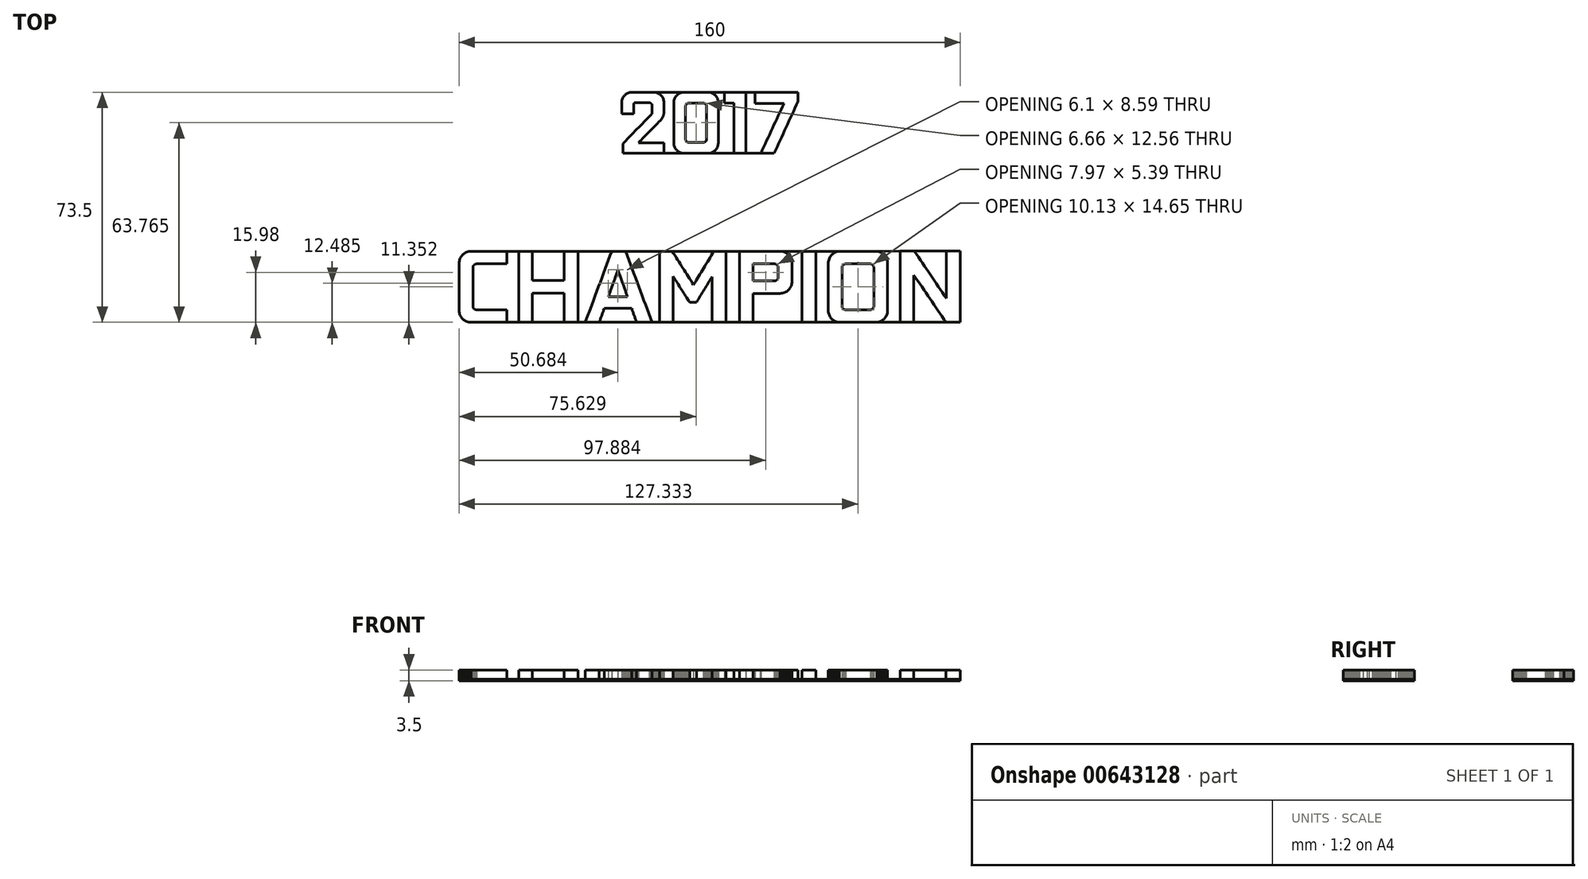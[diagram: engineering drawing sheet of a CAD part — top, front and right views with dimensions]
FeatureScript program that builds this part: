
annotation { "Feature Type Name" : "Feature", "Feature Type Description" : "" }
export const myFeature = defineFeature(function(context is Context, id is Id, definition is map)
    precondition{}
    {
        {
            var Q0;
            Q0=qCreatedBy(makeId("Top.planeOp"),FACE);
            var sketch = newSketch(context, id + "F0", { "sketchPlane" : qUnion([Q0])});
            skLineSegment(sketch, "E0", {"start": v(-76.2, -14.05) * mm, "end": v(-76.59, -14.07) * mm});
            skLineSegment(sketch, "E1", {"start": v(-76.59, -14.07) * mm, "end": v(-76.97, -14.12) * mm});
            skLineSegment(sketch, "E2", {"start": v(-76.97, -14.12) * mm, "end": v(-77.33, -14.22) * mm});
            skLineSegment(sketch, "E3", {"start": v(-77.33, -14.22) * mm, "end": v(-77.68, -14.35) * mm});
            skLineSegment(sketch, "E4", {"start": v(-77.68, -14.35) * mm, "end": v(-78.01, -14.5) * mm});
            skLineSegment(sketch, "E5", {"start": v(-78.01, -14.5) * mm, "end": v(-78.32, -14.7) * mm});
            skLineSegment(sketch, "E6", {"start": v(-78.32, -14.7) * mm, "end": v(-78.62, -14.91) * mm});
            skLineSegment(sketch, "E7", {"start": v(-78.62, -14.91) * mm, "end": v(-78.89, -15.16) * mm});
            skLineSegment(sketch, "E8", {"start": v(-78.89, -15.16) * mm, "end": v(-79.13, -15.43) * mm});
            skLineSegment(sketch, "E9", {"start": v(-79.13, -15.43) * mm, "end": v(-79.35, -15.72) * mm});
            skLineSegment(sketch, "E10", {"start": v(-79.35, -15.72) * mm, "end": v(-79.54, -16.03) * mm});
            skLineSegment(sketch, "E11", {"start": v(-79.54, -16.03) * mm, "end": v(-79.7, -16.36) * mm});
            skLineSegment(sketch, "E12", {"start": v(-79.7, -16.36) * mm, "end": v(-79.83, -16.71) * mm});
            skLineSegment(sketch, "E13", {"start": v(-79.83, -16.71) * mm, "end": v(-79.92, -17.08) * mm});
            skLineSegment(sketch, "E14", {"start": v(-79.92, -17.08) * mm, "end": v(-79.98, -17.45) * mm});
            skLineSegment(sketch, "E15", {"start": v(-79.98, -17.45) * mm, "end": v(-80, -17.84) * mm});
            skLineSegment(sketch, "E16", {"start": v(-80, -17.84) * mm, "end": v(-80, -18.79) * mm});
            skLineSegment(sketch, "E17", {"start": v(-80, -18.79) * mm, "end": v(-80, -19.73) * mm});
            skLineSegment(sketch, "E18", {"start": v(-80, -19.73) * mm, "end": v(-80, -20.68) * mm});
            skLineSegment(sketch, "E19", {"start": v(-80, -20.68) * mm, "end": v(-80, -21.63) * mm});
            skLineSegment(sketch, "E20", {"start": v(-80, -21.63) * mm, "end": v(-80, -22.57) * mm});
            skLineSegment(sketch, "E21", {"start": v(-80, -22.57) * mm, "end": v(-80, -23.52) * mm});
            skLineSegment(sketch, "E22", {"start": v(-80, -23.52) * mm, "end": v(-80, -24.47) * mm});
            skLineSegment(sketch, "E23", {"start": v(-80, -24.47) * mm, "end": v(-80, -25.41) * mm});
            skLineSegment(sketch, "E24", {"start": v(-80, -25.41) * mm, "end": v(-80, -26.36) * mm});
            skLineSegment(sketch, "E25", {"start": v(-80, -26.36) * mm, "end": v(-80, -27.3) * mm});
            skLineSegment(sketch, "E26", {"start": v(-80, -27.3) * mm, "end": v(-80, -28.25) * mm});
            skLineSegment(sketch, "E27", {"start": v(-80, -28.25) * mm, "end": v(-80, -29.2) * mm});
            skLineSegment(sketch, "E28", {"start": v(-80, -29.2) * mm, "end": v(-80, -30.15) * mm});
            skLineSegment(sketch, "E29", {"start": v(-80, -30.15) * mm, "end": v(-80, -31.1) * mm});
            skLineSegment(sketch, "E30", {"start": v(-80, -31.1) * mm, "end": v(-80, -32.04) * mm});
            skLineSegment(sketch, "E31", {"start": v(-80, -32.04) * mm, "end": v(-80, -32.99) * mm});
            skLineSegment(sketch, "E32", {"start": v(-80, -32.99) * mm, "end": v(-79.98, -33.37) * mm});
            skLineSegment(sketch, "E33", {"start": v(-79.98, -33.37) * mm, "end": v(-79.92, -33.74) * mm});
            skLineSegment(sketch, "E34", {"start": v(-79.92, -33.74) * mm, "end": v(-79.83, -34.1) * mm});
            skLineSegment(sketch, "E35", {"start": v(-79.83, -34.1) * mm, "end": v(-79.7, -34.45) * mm});
            skLineSegment(sketch, "E36", {"start": v(-79.7, -34.45) * mm, "end": v(-79.54, -34.77) * mm});
            skLineSegment(sketch, "E37", {"start": v(-79.54, -34.77) * mm, "end": v(-79.35, -35.08) * mm});
            skLineSegment(sketch, "E38", {"start": v(-79.35, -35.08) * mm, "end": v(-79.13, -35.37) * mm});
            skLineSegment(sketch, "E39", {"start": v(-79.13, -35.37) * mm, "end": v(-78.89, -35.64) * mm});
            skLineSegment(sketch, "E40", {"start": v(-78.89, -35.64) * mm, "end": v(-78.62, -35.89) * mm});
            skLineSegment(sketch, "E41", {"start": v(-78.62, -35.89) * mm, "end": v(-78.32, -36.1) * mm});
            skLineSegment(sketch, "E42", {"start": v(-78.32, -36.1) * mm, "end": v(-78.01, -36.3) * mm});
            skLineSegment(sketch, "E43", {"start": v(-78.01, -36.3) * mm, "end": v(-77.68, -36.45) * mm});
            skLineSegment(sketch, "E44", {"start": v(-77.68, -36.45) * mm, "end": v(-77.33, -36.58) * mm});
            skLineSegment(sketch, "E45", {"start": v(-77.33, -36.58) * mm, "end": v(-76.97, -36.67) * mm});
            skLineSegment(sketch, "E46", {"start": v(-76.97, -36.67) * mm, "end": v(-76.59, -36.73) * mm});
            skLineSegment(sketch, "E47", {"start": v(-76.59, -36.73) * mm, "end": v(-76.2, -36.75) * mm});
            skLineSegment(sketch, "E48", {"start": v(-76.2, -36.75) * mm, "end": v(-75.49, -36.75) * mm});
            skLineSegment(sketch, "E49", {"start": v(-75.49, -36.75) * mm, "end": v(-74.78, -36.75) * mm});
            skLineSegment(sketch, "E50", {"start": v(-74.78, -36.75) * mm, "end": v(-74.07, -36.75) * mm});
            skLineSegment(sketch, "E51", {"start": v(-74.07, -36.75) * mm, "end": v(-73.36, -36.75) * mm});
            skLineSegment(sketch, "E52", {"start": v(-73.36, -36.75) * mm, "end": v(-72.65, -36.75) * mm});
            skLineSegment(sketch, "E53", {"start": v(-72.65, -36.75) * mm, "end": v(-71.94, -36.75) * mm});
            skLineSegment(sketch, "E54", {"start": v(-71.94, -36.75) * mm, "end": v(-71.23, -36.75) * mm});
            skLineSegment(sketch, "E55", {"start": v(-71.23, -36.75) * mm, "end": v(-70.52, -36.75) * mm});
            skLineSegment(sketch, "E56", {"start": v(-70.52, -36.75) * mm, "end": v(-69.8, -36.75) * mm});
            skLineSegment(sketch, "E57", {"start": v(-69.8, -36.75) * mm, "end": v(-69.1, -36.75) * mm});
            skLineSegment(sketch, "E58", {"start": v(-69.1, -36.75) * mm, "end": v(-68.39, -36.75) * mm});
            skLineSegment(sketch, "E59", {"start": v(-68.39, -36.75) * mm, "end": v(-67.67, -36.75) * mm});
            skLineSegment(sketch, "E60", {"start": v(-67.67, -36.75) * mm, "end": v(-66.96, -36.75) * mm});
            skLineSegment(sketch, "E61", {"start": v(-66.96, -36.75) * mm, "end": v(-66.25, -36.75) * mm});
            skLineSegment(sketch, "E62", {"start": v(-66.25, -36.75) * mm, "end": v(-65.54, -36.75) * mm});
            skLineSegment(sketch, "E63", {"start": v(-65.54, -36.75) * mm, "end": v(-64.83, -36.75) * mm});
            skLineSegment(sketch, "E64", {"start": v(-64.83, -36.75) * mm, "end": v(-64.83, -36.5) * mm});
            skLineSegment(sketch, "E65", {"start": v(-64.83, -36.5) * mm, "end": v(-64.83, -36.25) * mm});
            skLineSegment(sketch, "E66", {"start": v(-64.83, -36.25) * mm, "end": v(-64.83, -36) * mm});
            skLineSegment(sketch, "E67", {"start": v(-64.83, -36) * mm, "end": v(-64.83, -35.74) * mm});
            skLineSegment(sketch, "E68", {"start": v(-64.83, -35.74) * mm, "end": v(-64.83, -35.5) * mm});
            skLineSegment(sketch, "E69", {"start": v(-64.83, -35.5) * mm, "end": v(-64.83, -35.24) * mm});
            skLineSegment(sketch, "E70", {"start": v(-64.83, -35.24) * mm, "end": v(-64.83, -34.99) * mm});
            skLineSegment(sketch, "E71", {"start": v(-64.83, -34.99) * mm, "end": v(-64.83, -34.74) * mm});
            skLineSegment(sketch, "E72", {"start": v(-64.83, -34.74) * mm, "end": v(-64.83, -34.48) * mm});
            skLineSegment(sketch, "E73", {"start": v(-64.83, -34.48) * mm, "end": v(-64.83, -34.23) * mm});
            skLineSegment(sketch, "E74", {"start": v(-64.83, -34.23) * mm, "end": v(-64.83, -33.98) * mm});
            skLineSegment(sketch, "E75", {"start": v(-64.83, -33.98) * mm, "end": v(-64.83, -33.73) * mm});
            skLineSegment(sketch, "E76", {"start": v(-64.83, -33.73) * mm, "end": v(-64.83, -33.48) * mm});
            skLineSegment(sketch, "E77", {"start": v(-64.83, -33.48) * mm, "end": v(-64.83, -33.22) * mm});
            skLineSegment(sketch, "E78", {"start": v(-64.83, -33.22) * mm, "end": v(-64.83, -32.97) * mm});
            skLineSegment(sketch, "E79", {"start": v(-64.83, -32.97) * mm, "end": v(-64.83, -32.72) * mm});
            skLineSegment(sketch, "E80", {"start": v(-64.83, -32.72) * mm, "end": v(-65.44, -32.72) * mm});
            skLineSegment(sketch, "E81", {"start": v(-65.44, -32.72) * mm, "end": v(-66.04, -32.72) * mm});
            skLineSegment(sketch, "E82", {"start": v(-66.04, -32.72) * mm, "end": v(-66.64, -32.72) * mm});
            skLineSegment(sketch, "E83", {"start": v(-66.64, -32.72) * mm, "end": v(-67.24, -32.72) * mm});
            skLineSegment(sketch, "E84", {"start": v(-67.24, -32.72) * mm, "end": v(-67.84, -32.72) * mm});
            skLineSegment(sketch, "E85", {"start": v(-67.84, -32.72) * mm, "end": v(-68.45, -32.72) * mm});
            skLineSegment(sketch, "E86", {"start": v(-68.45, -32.72) * mm, "end": v(-69.05, -32.72) * mm});
            skLineSegment(sketch, "E87", {"start": v(-69.05, -32.72) * mm, "end": v(-69.65, -32.72) * mm});
            skLineSegment(sketch, "E88", {"start": v(-69.65, -32.72) * mm, "end": v(-70.25, -32.72) * mm});
            skLineSegment(sketch, "E89", {"start": v(-70.25, -32.72) * mm, "end": v(-70.85, -32.72) * mm});
            skLineSegment(sketch, "E90", {"start": v(-70.85, -32.72) * mm, "end": v(-71.46, -32.72) * mm});
            skLineSegment(sketch, "E91", {"start": v(-71.46, -32.72) * mm, "end": v(-72.06, -32.72) * mm});
            skLineSegment(sketch, "E92", {"start": v(-72.06, -32.72) * mm, "end": v(-72.66, -32.72) * mm});
            skLineSegment(sketch, "E93", {"start": v(-72.66, -32.72) * mm, "end": v(-73.26, -32.72) * mm});
            skLineSegment(sketch, "E94", {"start": v(-73.26, -32.72) * mm, "end": v(-73.86, -32.72) * mm});
            skLineSegment(sketch, "E95", {"start": v(-73.86, -32.72) * mm, "end": v(-74.47, -32.72) * mm});
            skLineSegment(sketch, "E96", {"start": v(-74.47, -32.72) * mm, "end": v(-74.58, -32.72) * mm});
            skLineSegment(sketch, "E97", {"start": v(-74.58, -32.72) * mm, "end": v(-74.7, -32.7) * mm});
            skLineSegment(sketch, "E98", {"start": v(-74.7, -32.7) * mm, "end": v(-74.8, -32.67) * mm});
            skLineSegment(sketch, "E99", {"start": v(-74.8, -32.67) * mm, "end": v(-74.91, -32.63) * mm});
            skLineSegment(sketch, "E100", {"start": v(-74.91, -32.63) * mm, "end": v(-75.01, -32.59) * mm});
            skLineSegment(sketch, "E101", {"start": v(-75.01, -32.59) * mm, "end": v(-75.1, -32.53) * mm});
            skLineSegment(sketch, "E102", {"start": v(-75.1, -32.53) * mm, "end": v(-75.2, -32.47) * mm});
            skLineSegment(sketch, "E103", {"start": v(-75.2, -32.47) * mm, "end": v(-75.27, -32.4) * mm});
            skLineSegment(sketch, "E104", {"start": v(-75.27, -32.4) * mm, "end": v(-75.34, -32.31) * mm});
            skLineSegment(sketch, "E105", {"start": v(-75.34, -32.31) * mm, "end": v(-75.4, -32.23) * mm});
            skLineSegment(sketch, "E106", {"start": v(-75.4, -32.23) * mm, "end": v(-75.46, -32.13) * mm});
            skLineSegment(sketch, "E107", {"start": v(-75.46, -32.13) * mm, "end": v(-75.51, -32.03) * mm});
            skLineSegment(sketch, "E108", {"start": v(-75.51, -32.03) * mm, "end": v(-75.55, -31.93) * mm});
            skLineSegment(sketch, "E109", {"start": v(-75.55, -31.93) * mm, "end": v(-75.58, -31.82) * mm});
            skLineSegment(sketch, "E110", {"start": v(-75.58, -31.82) * mm, "end": v(-75.6, -31.7) * mm});
            skLineSegment(sketch, "E111", {"start": v(-75.6, -31.7) * mm, "end": v(-75.6, -31.59) * mm});
            skLineSegment(sketch, "E112", {"start": v(-75.6, -31.59) * mm, "end": v(-75.6, -30.82) * mm});
            skLineSegment(sketch, "E113", {"start": v(-75.6, -30.82) * mm, "end": v(-75.6, -30.04) * mm});
            skLineSegment(sketch, "E114", {"start": v(-75.6, -30.04) * mm, "end": v(-75.6, -29.27) * mm});
            skLineSegment(sketch, "E115", {"start": v(-75.6, -29.27) * mm, "end": v(-75.6, -28.5) * mm});
            skLineSegment(sketch, "E116", {"start": v(-75.6, -28.5) * mm, "end": v(-75.6, -27.72) * mm});
            skLineSegment(sketch, "E117", {"start": v(-75.6, -27.72) * mm, "end": v(-75.6, -26.95) * mm});
            skLineSegment(sketch, "E118", {"start": v(-75.6, -26.95) * mm, "end": v(-75.6, -26.17) * mm});
            skLineSegment(sketch, "E119", {"start": v(-75.6, -26.17) * mm, "end": v(-75.6, -25.4) * mm});
            skLineSegment(sketch, "E120", {"start": v(-75.6, -25.4) * mm, "end": v(-75.6, -24.62) * mm});
            skLineSegment(sketch, "E121", {"start": v(-75.6, -24.62) * mm, "end": v(-75.6, -23.85) * mm});
            skLineSegment(sketch, "E122", {"start": v(-75.6, -23.85) * mm, "end": v(-75.6, -23.08) * mm});
            skLineSegment(sketch, "E123", {"start": v(-75.6, -23.08) * mm, "end": v(-75.6, -22.3) * mm});
            skLineSegment(sketch, "E124", {"start": v(-75.6, -22.3) * mm, "end": v(-75.6, -21.53) * mm});
            skLineSegment(sketch, "E125", {"start": v(-75.6, -21.53) * mm, "end": v(-75.6, -20.75) * mm});
            skLineSegment(sketch, "E126", {"start": v(-75.6, -20.75) * mm, "end": v(-75.6, -19.98) * mm});
            skLineSegment(sketch, "E127", {"start": v(-75.6, -19.98) * mm, "end": v(-75.6, -19.2) * mm});
            skLineSegment(sketch, "E128", {"start": v(-75.6, -19.2) * mm, "end": v(-75.6, -19.1) * mm});
            skLineSegment(sketch, "E129", {"start": v(-75.6, -19.1) * mm, "end": v(-75.58, -18.99) * mm});
            skLineSegment(sketch, "E130", {"start": v(-75.58, -18.99) * mm, "end": v(-75.55, -18.88) * mm});
            skLineSegment(sketch, "E131", {"start": v(-75.55, -18.88) * mm, "end": v(-75.51, -18.78) * mm});
            skLineSegment(sketch, "E132", {"start": v(-75.51, -18.78) * mm, "end": v(-75.46, -18.68) * mm});
            skLineSegment(sketch, "E133", {"start": v(-75.46, -18.68) * mm, "end": v(-75.4, -18.59) * mm});
            skLineSegment(sketch, "E134", {"start": v(-75.4, -18.59) * mm, "end": v(-75.34, -18.5) * mm});
            skLineSegment(sketch, "E135", {"start": v(-75.34, -18.5) * mm, "end": v(-75.27, -18.42) * mm});
            skLineSegment(sketch, "E136", {"start": v(-75.27, -18.42) * mm, "end": v(-75.2, -18.34) * mm});
            skLineSegment(sketch, "E137", {"start": v(-75.2, -18.34) * mm, "end": v(-75.1, -18.27) * mm});
            skLineSegment(sketch, "E138", {"start": v(-75.1, -18.27) * mm, "end": v(-75.01, -18.22) * mm});
            skLineSegment(sketch, "E139", {"start": v(-75.01, -18.22) * mm, "end": v(-74.91, -18.17) * mm});
            skLineSegment(sketch, "E140", {"start": v(-74.91, -18.17) * mm, "end": v(-74.8, -18.13) * mm});
            skLineSegment(sketch, "E141", {"start": v(-74.8, -18.13) * mm, "end": v(-74.7, -18.1) * mm});
            skLineSegment(sketch, "E142", {"start": v(-74.7, -18.1) * mm, "end": v(-74.58, -18.08) * mm});
            skLineSegment(sketch, "E143", {"start": v(-74.58, -18.08) * mm, "end": v(-74.47, -18.07) * mm});
            skLineSegment(sketch, "E144", {"start": v(-74.47, -18.07) * mm, "end": v(-73.86, -18.07) * mm});
            skLineSegment(sketch, "E145", {"start": v(-73.86, -18.07) * mm, "end": v(-73.26, -18.07) * mm});
            skLineSegment(sketch, "E146", {"start": v(-73.26, -18.07) * mm, "end": v(-72.66, -18.07) * mm});
            skLineSegment(sketch, "E147", {"start": v(-72.66, -18.07) * mm, "end": v(-72.06, -18.07) * mm});
            skLineSegment(sketch, "E148", {"start": v(-72.06, -18.07) * mm, "end": v(-71.46, -18.07) * mm});
            skLineSegment(sketch, "E149", {"start": v(-71.46, -18.07) * mm, "end": v(-70.85, -18.07) * mm});
            skLineSegment(sketch, "E150", {"start": v(-70.85, -18.07) * mm, "end": v(-70.25, -18.07) * mm});
            skLineSegment(sketch, "E151", {"start": v(-70.25, -18.07) * mm, "end": v(-69.65, -18.07) * mm});
            skLineSegment(sketch, "E152", {"start": v(-69.65, -18.07) * mm, "end": v(-69.05, -18.07) * mm});
            skLineSegment(sketch, "E153", {"start": v(-69.05, -18.07) * mm, "end": v(-68.45, -18.07) * mm});
            skLineSegment(sketch, "E154", {"start": v(-68.45, -18.07) * mm, "end": v(-67.84, -18.07) * mm});
            skLineSegment(sketch, "E155", {"start": v(-67.84, -18.07) * mm, "end": v(-67.24, -18.07) * mm});
            skLineSegment(sketch, "E156", {"start": v(-67.24, -18.07) * mm, "end": v(-66.64, -18.07) * mm});
            skLineSegment(sketch, "E157", {"start": v(-66.64, -18.07) * mm, "end": v(-66.04, -18.07) * mm});
            skLineSegment(sketch, "E158", {"start": v(-66.04, -18.07) * mm, "end": v(-65.44, -18.07) * mm});
            skLineSegment(sketch, "E159", {"start": v(-65.44, -18.07) * mm, "end": v(-64.83, -18.07) * mm});
            skLineSegment(sketch, "E160", {"start": v(-64.83, -18.07) * mm, "end": v(-64.83, -17.82) * mm});
            skLineSegment(sketch, "E161", {"start": v(-64.83, -17.82) * mm, "end": v(-64.83, -17.57) * mm});
            skLineSegment(sketch, "E162", {"start": v(-64.83, -17.57) * mm, "end": v(-64.83, -17.32) * mm});
            skLineSegment(sketch, "E163", {"start": v(-64.83, -17.32) * mm, "end": v(-64.83, -17.07) * mm});
            skLineSegment(sketch, "E164", {"start": v(-64.83, -17.07) * mm, "end": v(-64.83, -16.82) * mm});
            skLineSegment(sketch, "E165", {"start": v(-64.83, -16.82) * mm, "end": v(-64.83, -16.56) * mm});
            skLineSegment(sketch, "E166", {"start": v(-64.83, -16.56) * mm, "end": v(-64.83, -16.31) * mm});
            skLineSegment(sketch, "E167", {"start": v(-64.83, -16.31) * mm, "end": v(-64.83, -16.06) * mm});
            skLineSegment(sketch, "E168", {"start": v(-64.83, -16.06) * mm, "end": v(-64.83, -15.8) * mm});
            skLineSegment(sketch, "E169", {"start": v(-64.83, -15.8) * mm, "end": v(-64.83, -15.56) * mm});
            skLineSegment(sketch, "E170", {"start": v(-64.83, -15.56) * mm, "end": v(-64.83, -15.3) * mm});
            skLineSegment(sketch, "E171", {"start": v(-64.83, -15.3) * mm, "end": v(-64.83, -15.05) * mm});
            skLineSegment(sketch, "E172", {"start": v(-64.83, -15.05) * mm, "end": v(-64.83, -14.8) * mm});
            skLineSegment(sketch, "E173", {"start": v(-64.83, -14.8) * mm, "end": v(-64.83, -14.55) * mm});
            skLineSegment(sketch, "E174", {"start": v(-64.83, -14.55) * mm, "end": v(-64.83, -14.3) * mm});
            skLineSegment(sketch, "E175", {"start": v(-64.83, -14.3) * mm, "end": v(-64.83, -14.05) * mm});
            skLineSegment(sketch, "E176", {"start": v(-64.83, -14.05) * mm, "end": v(-65.54, -14.05) * mm});
            skLineSegment(sketch, "E177", {"start": v(-65.54, -14.05) * mm, "end": v(-66.25, -14.05) * mm});
            skLineSegment(sketch, "E178", {"start": v(-66.25, -14.05) * mm, "end": v(-66.96, -14.05) * mm});
            skLineSegment(sketch, "E179", {"start": v(-66.96, -14.05) * mm, "end": v(-67.67, -14.05) * mm});
            skLineSegment(sketch, "E180", {"start": v(-67.67, -14.05) * mm, "end": v(-68.39, -14.05) * mm});
            skLineSegment(sketch, "E181", {"start": v(-68.39, -14.05) * mm, "end": v(-69.1, -14.05) * mm});
            skLineSegment(sketch, "E182", {"start": v(-69.1, -14.05) * mm, "end": v(-69.8, -14.05) * mm});
            skLineSegment(sketch, "E183", {"start": v(-69.8, -14.05) * mm, "end": v(-70.52, -14.05) * mm});
            skLineSegment(sketch, "E184", {"start": v(-70.52, -14.05) * mm, "end": v(-71.23, -14.05) * mm});
            skLineSegment(sketch, "E185", {"start": v(-71.23, -14.05) * mm, "end": v(-71.94, -14.05) * mm});
            skLineSegment(sketch, "E186", {"start": v(-71.94, -14.05) * mm, "end": v(-72.65, -14.05) * mm});
            skLineSegment(sketch, "E187", {"start": v(-72.65, -14.05) * mm, "end": v(-73.36, -14.05) * mm});
            skLineSegment(sketch, "E188", {"start": v(-73.36, -14.05) * mm, "end": v(-74.07, -14.05) * mm});
            skLineSegment(sketch, "E189", {"start": v(-74.07, -14.05) * mm, "end": v(-74.78, -14.05) * mm});
            skLineSegment(sketch, "E190", {"start": v(-74.78, -14.05) * mm, "end": v(-75.49, -14.05) * mm});
            skLineSegment(sketch, "E191", {"start": v(-75.49, -14.05) * mm, "end": v(-76.2, -14.05) * mm});
            skLineSegment(sketch, "E192", {"start": v(-46.47, -14.05) * mm, "end": v(-46.47, -14.63) * mm});
            skLineSegment(sketch, "E193", {"start": v(-46.47, -14.63) * mm, "end": v(-46.47, -15.22) * mm});
            skLineSegment(sketch, "E194", {"start": v(-46.47, -15.22) * mm, "end": v(-46.47, -15.8) * mm});
            skLineSegment(sketch, "E195", {"start": v(-46.47, -15.8) * mm, "end": v(-46.47, -16.39) * mm});
            skLineSegment(sketch, "E196", {"start": v(-46.47, -16.39) * mm, "end": v(-46.47, -16.97) * mm});
            skLineSegment(sketch, "E197", {"start": v(-46.47, -16.97) * mm, "end": v(-46.47, -17.55) * mm});
            skLineSegment(sketch, "E198", {"start": v(-46.47, -17.55) * mm, "end": v(-46.47, -18.14) * mm});
            skLineSegment(sketch, "E199", {"start": v(-46.47, -18.14) * mm, "end": v(-46.47, -18.72) * mm});
            skLineSegment(sketch, "E200", {"start": v(-46.47, -18.72) * mm, "end": v(-46.47, -19.3) * mm});
            skLineSegment(sketch, "E201", {"start": v(-46.47, -19.3) * mm, "end": v(-46.47, -19.9) * mm});
            skLineSegment(sketch, "E202", {"start": v(-46.47, -19.9) * mm, "end": v(-46.47, -20.48) * mm});
            skLineSegment(sketch, "E203", {"start": v(-46.47, -20.48) * mm, "end": v(-46.47, -21.06) * mm});
            skLineSegment(sketch, "E204", {"start": v(-46.47, -21.06) * mm, "end": v(-46.47, -21.65) * mm});
            skLineSegment(sketch, "E205", {"start": v(-46.47, -21.65) * mm, "end": v(-46.47, -22.23) * mm});
            skLineSegment(sketch, "E206", {"start": v(-46.47, -22.23) * mm, "end": v(-46.47, -22.82) * mm});
            skLineSegment(sketch, "E207", {"start": v(-46.47, -22.82) * mm, "end": v(-46.47, -23.4) * mm});
            skLineSegment(sketch, "E208", {"start": v(-46.47, -23.4) * mm, "end": v(-47.1, -23.4) * mm});
            skLineSegment(sketch, "E209", {"start": v(-47.1, -23.4) * mm, "end": v(-47.73, -23.4) * mm});
            skLineSegment(sketch, "E210", {"start": v(-47.73, -23.4) * mm, "end": v(-48.37, -23.4) * mm});
            skLineSegment(sketch, "E211", {"start": v(-48.37, -23.4) * mm, "end": v(-49, -23.4) * mm});
            skLineSegment(sketch, "E212", {"start": v(-49, -23.4) * mm, "end": v(-49.63, -23.4) * mm});
            skLineSegment(sketch, "E213", {"start": v(-49.63, -23.4) * mm, "end": v(-50.27, -23.4) * mm});
            skLineSegment(sketch, "E214", {"start": v(-50.27, -23.4) * mm, "end": v(-50.9, -23.4) * mm});
            skLineSegment(sketch, "E215", {"start": v(-50.9, -23.4) * mm, "end": v(-51.53, -23.4) * mm});
            skLineSegment(sketch, "E216", {"start": v(-51.53, -23.4) * mm, "end": v(-52.17, -23.4) * mm});
            skLineSegment(sketch, "E217", {"start": v(-52.17, -23.4) * mm, "end": v(-52.8, -23.4) * mm});
            skLineSegment(sketch, "E218", {"start": v(-52.8, -23.4) * mm, "end": v(-53.43, -23.4) * mm});
            skLineSegment(sketch, "E219", {"start": v(-53.43, -23.4) * mm, "end": v(-54.07, -23.4) * mm});
            skLineSegment(sketch, "E220", {"start": v(-54.07, -23.4) * mm, "end": v(-54.7, -23.4) * mm});
            skLineSegment(sketch, "E221", {"start": v(-54.7, -23.4) * mm, "end": v(-55.33, -23.4) * mm});
            skLineSegment(sketch, "E222", {"start": v(-55.33, -23.4) * mm, "end": v(-55.97, -23.4) * mm});
            skLineSegment(sketch, "E223", {"start": v(-55.97, -23.4) * mm, "end": v(-56.6, -23.4) * mm});
            skLineSegment(sketch, "E224", {"start": v(-56.6, -23.4) * mm, "end": v(-56.6, -22.82) * mm});
            skLineSegment(sketch, "E225", {"start": v(-56.6, -22.82) * mm, "end": v(-56.6, -22.23) * mm});
            skLineSegment(sketch, "E226", {"start": v(-56.6, -22.23) * mm, "end": v(-56.6, -21.65) * mm});
            skLineSegment(sketch, "E227", {"start": v(-56.6, -21.65) * mm, "end": v(-56.6, -21.06) * mm});
            skLineSegment(sketch, "E228", {"start": v(-56.6, -21.06) * mm, "end": v(-56.6, -20.48) * mm});
            skLineSegment(sketch, "E229", {"start": v(-56.6, -20.48) * mm, "end": v(-56.6, -19.9) * mm});
            skLineSegment(sketch, "E230", {"start": v(-56.6, -19.9) * mm, "end": v(-56.6, -19.3) * mm});
            skLineSegment(sketch, "E231", {"start": v(-56.6, -19.3) * mm, "end": v(-56.6, -18.72) * mm});
            skLineSegment(sketch, "E232", {"start": v(-56.6, -18.72) * mm, "end": v(-56.6, -18.14) * mm});
            skLineSegment(sketch, "E233", {"start": v(-56.6, -18.14) * mm, "end": v(-56.6, -17.55) * mm});
            skLineSegment(sketch, "E234", {"start": v(-56.6, -17.55) * mm, "end": v(-56.6, -16.97) * mm});
            skLineSegment(sketch, "E235", {"start": v(-56.6, -16.97) * mm, "end": v(-56.6, -16.39) * mm});
            skLineSegment(sketch, "E236", {"start": v(-56.6, -16.39) * mm, "end": v(-56.6, -15.8) * mm});
            skLineSegment(sketch, "E237", {"start": v(-56.6, -15.8) * mm, "end": v(-56.6, -15.22) * mm});
            skLineSegment(sketch, "E238", {"start": v(-56.6, -15.22) * mm, "end": v(-56.6, -14.63) * mm});
            skLineSegment(sketch, "E239", {"start": v(-56.6, -14.63) * mm, "end": v(-56.6, -14.05) * mm});
            skLineSegment(sketch, "E240", {"start": v(-56.6, -14.05) * mm, "end": v(-56.87, -14.05) * mm});
            skLineSegment(sketch, "E241", {"start": v(-56.87, -14.05) * mm, "end": v(-57.15, -14.05) * mm});
            skLineSegment(sketch, "E242", {"start": v(-57.15, -14.05) * mm, "end": v(-57.42, -14.05) * mm});
            skLineSegment(sketch, "E243", {"start": v(-57.42, -14.05) * mm, "end": v(-57.7, -14.05) * mm});
            skLineSegment(sketch, "E244", {"start": v(-57.7, -14.05) * mm, "end": v(-57.97, -14.05) * mm});
            skLineSegment(sketch, "E245", {"start": v(-57.97, -14.05) * mm, "end": v(-58.25, -14.05) * mm});
            skLineSegment(sketch, "E246", {"start": v(-58.25, -14.05) * mm, "end": v(-58.52, -14.05) * mm});
            skLineSegment(sketch, "E247", {"start": v(-58.52, -14.05) * mm, "end": v(-58.8, -14.05) * mm});
            skLineSegment(sketch, "E248", {"start": v(-58.8, -14.05) * mm, "end": v(-59.07, -14.05) * mm});
            skLineSegment(sketch, "E249", {"start": v(-59.07, -14.05) * mm, "end": v(-59.35, -14.05) * mm});
            skLineSegment(sketch, "E250", {"start": v(-59.35, -14.05) * mm, "end": v(-59.62, -14.05) * mm});
            skLineSegment(sketch, "E251", {"start": v(-59.62, -14.05) * mm, "end": v(-59.9, -14.05) * mm});
            skLineSegment(sketch, "E252", {"start": v(-59.9, -14.05) * mm, "end": v(-60.17, -14.05) * mm});
            skLineSegment(sketch, "E253", {"start": v(-60.17, -14.05) * mm, "end": v(-60.45, -14.05) * mm});
            skLineSegment(sketch, "E254", {"start": v(-60.45, -14.05) * mm, "end": v(-60.72, -14.05) * mm});
            skLineSegment(sketch, "E255", {"start": v(-60.72, -14.05) * mm, "end": v(-61, -14.05) * mm});
            skLineSegment(sketch, "E256", {"start": v(-61, -14.05) * mm, "end": v(-61, -15.47) * mm});
            skLineSegment(sketch, "E257", {"start": v(-61, -15.47) * mm, "end": v(-61, -16.88) * mm});
            skLineSegment(sketch, "E258", {"start": v(-61, -16.88) * mm, "end": v(-61, -18.3) * mm});
            skLineSegment(sketch, "E259", {"start": v(-61, -18.3) * mm, "end": v(-61, -19.72) * mm});
            skLineSegment(sketch, "E260", {"start": v(-61, -19.72) * mm, "end": v(-61, -21.14) * mm});
            skLineSegment(sketch, "E261", {"start": v(-61, -21.14) * mm, "end": v(-61, -22.56) * mm});
            skLineSegment(sketch, "E262", {"start": v(-61, -22.56) * mm, "end": v(-61, -23.98) * mm});
            skLineSegment(sketch, "E263", {"start": v(-61, -23.98) * mm, "end": v(-61, -25.4) * mm});
            skLineSegment(sketch, "E264", {"start": v(-61, -25.4) * mm, "end": v(-61, -26.82) * mm});
            skLineSegment(sketch, "E265", {"start": v(-61, -26.82) * mm, "end": v(-61, -28.24) * mm});
            skLineSegment(sketch, "E266", {"start": v(-61, -28.24) * mm, "end": v(-61, -29.65) * mm});
            skLineSegment(sketch, "E267", {"start": v(-61, -29.65) * mm, "end": v(-61, -31.07) * mm});
            skLineSegment(sketch, "E268", {"start": v(-61, -31.07) * mm, "end": v(-61, -32.5) * mm});
            skLineSegment(sketch, "E269", {"start": v(-61, -32.5) * mm, "end": v(-61, -33.91) * mm});
            skLineSegment(sketch, "E270", {"start": v(-61, -33.91) * mm, "end": v(-61, -35.33) * mm});
            skLineSegment(sketch, "E271", {"start": v(-61, -35.33) * mm, "end": v(-61, -36.75) * mm});
            skLineSegment(sketch, "E272", {"start": v(-61, -36.75) * mm, "end": v(-60.72, -36.75) * mm});
            skLineSegment(sketch, "E273", {"start": v(-60.72, -36.75) * mm, "end": v(-60.45, -36.75) * mm});
            skLineSegment(sketch, "E274", {"start": v(-60.45, -36.75) * mm, "end": v(-60.17, -36.75) * mm});
            skLineSegment(sketch, "E275", {"start": v(-60.17, -36.75) * mm, "end": v(-59.9, -36.75) * mm});
            skLineSegment(sketch, "E276", {"start": v(-59.9, -36.75) * mm, "end": v(-59.62, -36.75) * mm});
            skLineSegment(sketch, "E277", {"start": v(-59.62, -36.75) * mm, "end": v(-59.35, -36.75) * mm});
            skLineSegment(sketch, "E278", {"start": v(-59.35, -36.75) * mm, "end": v(-59.07, -36.75) * mm});
            skLineSegment(sketch, "E279", {"start": v(-59.07, -36.75) * mm, "end": v(-58.8, -36.75) * mm});
            skLineSegment(sketch, "E280", {"start": v(-58.8, -36.75) * mm, "end": v(-58.52, -36.75) * mm});
            skLineSegment(sketch, "E281", {"start": v(-58.52, -36.75) * mm, "end": v(-58.25, -36.75) * mm});
            skLineSegment(sketch, "E282", {"start": v(-58.25, -36.75) * mm, "end": v(-57.97, -36.75) * mm});
            skLineSegment(sketch, "E283", {"start": v(-57.97, -36.75) * mm, "end": v(-57.7, -36.75) * mm});
            skLineSegment(sketch, "E284", {"start": v(-57.7, -36.75) * mm, "end": v(-57.42, -36.75) * mm});
            skLineSegment(sketch, "E285", {"start": v(-57.42, -36.75) * mm, "end": v(-57.15, -36.75) * mm});
            skLineSegment(sketch, "E286", {"start": v(-57.15, -36.75) * mm, "end": v(-56.87, -36.75) * mm});
            skLineSegment(sketch, "E287", {"start": v(-56.87, -36.75) * mm, "end": v(-56.6, -36.75) * mm});
            skLineSegment(sketch, "E288", {"start": v(-56.6, -36.75) * mm, "end": v(-56.6, -36.17) * mm});
            skLineSegment(sketch, "E289", {"start": v(-56.6, -36.17) * mm, "end": v(-56.6, -35.58) * mm});
            skLineSegment(sketch, "E290", {"start": v(-56.6, -35.58) * mm, "end": v(-56.6, -35) * mm});
            skLineSegment(sketch, "E291", {"start": v(-56.6, -35) * mm, "end": v(-56.6, -34.42) * mm});
            skLineSegment(sketch, "E292", {"start": v(-56.6, -34.42) * mm, "end": v(-56.6, -33.84) * mm});
            skLineSegment(sketch, "E293", {"start": v(-56.6, -33.84) * mm, "end": v(-56.6, -33.25) * mm});
            skLineSegment(sketch, "E294", {"start": v(-56.6, -33.25) * mm, "end": v(-56.6, -32.67) * mm});
            skLineSegment(sketch, "E295", {"start": v(-56.6, -32.67) * mm, "end": v(-56.6, -32.09) * mm});
            skLineSegment(sketch, "E296", {"start": v(-56.6, -32.09) * mm, "end": v(-56.6, -31.5) * mm});
            skLineSegment(sketch, "E297", {"start": v(-56.6, -31.5) * mm, "end": v(-56.6, -30.92) * mm});
            skLineSegment(sketch, "E298", {"start": v(-56.6, -30.92) * mm, "end": v(-56.6, -30.34) * mm});
            skLineSegment(sketch, "E299", {"start": v(-56.6, -30.34) * mm, "end": v(-56.6, -29.76) * mm});
            skLineSegment(sketch, "E300", {"start": v(-56.6, -29.76) * mm, "end": v(-56.6, -29.18) * mm});
            skLineSegment(sketch, "E301", {"start": v(-56.6, -29.18) * mm, "end": v(-56.6, -28.6) * mm});
            skLineSegment(sketch, "E302", {"start": v(-56.6, -28.6) * mm, "end": v(-56.6, -28.01) * mm});
            skLineSegment(sketch, "E303", {"start": v(-56.6, -28.01) * mm, "end": v(-56.6, -27.43) * mm});
            skLineSegment(sketch, "E304", {"start": v(-56.6, -27.43) * mm, "end": v(-55.97, -27.43) * mm});
            skLineSegment(sketch, "E305", {"start": v(-55.97, -27.43) * mm, "end": v(-55.33, -27.43) * mm});
            skLineSegment(sketch, "E306", {"start": v(-55.33, -27.43) * mm, "end": v(-54.7, -27.43) * mm});
            skLineSegment(sketch, "E307", {"start": v(-54.7, -27.43) * mm, "end": v(-54.07, -27.43) * mm});
            skLineSegment(sketch, "E308", {"start": v(-54.07, -27.43) * mm, "end": v(-53.43, -27.43) * mm});
            skLineSegment(sketch, "E309", {"start": v(-53.43, -27.43) * mm, "end": v(-52.8, -27.43) * mm});
            skLineSegment(sketch, "E310", {"start": v(-52.8, -27.43) * mm, "end": v(-52.17, -27.43) * mm});
            skLineSegment(sketch, "E311", {"start": v(-52.17, -27.43) * mm, "end": v(-51.53, -27.43) * mm});
            skLineSegment(sketch, "E312", {"start": v(-51.53, -27.43) * mm, "end": v(-50.9, -27.43) * mm});
            skLineSegment(sketch, "E313", {"start": v(-50.9, -27.43) * mm, "end": v(-50.27, -27.43) * mm});
            skLineSegment(sketch, "E314", {"start": v(-50.27, -27.43) * mm, "end": v(-49.63, -27.43) * mm});
            skLineSegment(sketch, "E315", {"start": v(-49.63, -27.43) * mm, "end": v(-49, -27.43) * mm});
            skLineSegment(sketch, "E316", {"start": v(-49, -27.43) * mm, "end": v(-48.37, -27.43) * mm});
            skLineSegment(sketch, "E317", {"start": v(-48.37, -27.43) * mm, "end": v(-47.73, -27.43) * mm});
            skLineSegment(sketch, "E318", {"start": v(-47.73, -27.43) * mm, "end": v(-47.1, -27.43) * mm});
            skLineSegment(sketch, "E319", {"start": v(-47.1, -27.43) * mm, "end": v(-46.47, -27.43) * mm});
            skLineSegment(sketch, "E320", {"start": v(-46.47, -27.43) * mm, "end": v(-46.47, -28.01) * mm});
            skLineSegment(sketch, "E321", {"start": v(-46.47, -28.01) * mm, "end": v(-46.47, -28.6) * mm});
            skLineSegment(sketch, "E322", {"start": v(-46.47, -28.6) * mm, "end": v(-46.47, -29.18) * mm});
            skLineSegment(sketch, "E323", {"start": v(-46.47, -29.18) * mm, "end": v(-46.47, -29.76) * mm});
            skLineSegment(sketch, "E324", {"start": v(-46.47, -29.76) * mm, "end": v(-46.47, -30.34) * mm});
            skLineSegment(sketch, "E325", {"start": v(-46.47, -30.34) * mm, "end": v(-46.47, -30.92) * mm});
            skLineSegment(sketch, "E326", {"start": v(-46.47, -30.92) * mm, "end": v(-46.47, -31.5) * mm});
            skLineSegment(sketch, "E327", {"start": v(-46.47, -31.5) * mm, "end": v(-46.47, -32.09) * mm});
            skLineSegment(sketch, "E328", {"start": v(-46.47, -32.09) * mm, "end": v(-46.47, -32.67) * mm});
            skLineSegment(sketch, "E329", {"start": v(-46.47, -32.67) * mm, "end": v(-46.47, -33.25) * mm});
            skLineSegment(sketch, "E330", {"start": v(-46.47, -33.25) * mm, "end": v(-46.47, -33.84) * mm});
            skLineSegment(sketch, "E331", {"start": v(-46.47, -33.84) * mm, "end": v(-46.47, -34.42) * mm});
            skLineSegment(sketch, "E332", {"start": v(-46.47, -34.42) * mm, "end": v(-46.47, -35) * mm});
            skLineSegment(sketch, "E333", {"start": v(-46.47, -35) * mm, "end": v(-46.47, -35.58) * mm});
            skLineSegment(sketch, "E334", {"start": v(-46.47, -35.58) * mm, "end": v(-46.47, -36.17) * mm});
            skLineSegment(sketch, "E335", {"start": v(-46.47, -36.17) * mm, "end": v(-46.47, -36.75) * mm});
            skLineSegment(sketch, "E336", {"start": v(-46.47, -36.75) * mm, "end": v(-46.2, -36.75) * mm});
            skLineSegment(sketch, "E337", {"start": v(-46.2, -36.75) * mm, "end": v(-45.92, -36.75) * mm});
            skLineSegment(sketch, "E338", {"start": v(-45.92, -36.75) * mm, "end": v(-45.64, -36.75) * mm});
            skLineSegment(sketch, "E339", {"start": v(-45.64, -36.75) * mm, "end": v(-45.37, -36.75) * mm});
            skLineSegment(sketch, "E340", {"start": v(-45.37, -36.75) * mm, "end": v(-45.1, -36.75) * mm});
            skLineSegment(sketch, "E341", {"start": v(-45.1, -36.75) * mm, "end": v(-44.82, -36.75) * mm});
            skLineSegment(sketch, "E342", {"start": v(-44.82, -36.75) * mm, "end": v(-44.54, -36.75) * mm});
            skLineSegment(sketch, "E343", {"start": v(-44.54, -36.75) * mm, "end": v(-44.27, -36.75) * mm});
            skLineSegment(sketch, "E344", {"start": v(-44.27, -36.75) * mm, "end": v(-44, -36.75) * mm});
            skLineSegment(sketch, "E345", {"start": v(-44, -36.75) * mm, "end": v(-43.72, -36.75) * mm});
            skLineSegment(sketch, "E346", {"start": v(-43.72, -36.75) * mm, "end": v(-43.44, -36.75) * mm});
            skLineSegment(sketch, "E347", {"start": v(-43.44, -36.75) * mm, "end": v(-43.17, -36.75) * mm});
            skLineSegment(sketch, "E348", {"start": v(-43.17, -36.75) * mm, "end": v(-42.9, -36.75) * mm});
            skLineSegment(sketch, "E349", {"start": v(-42.9, -36.75) * mm, "end": v(-42.62, -36.75) * mm});
            skLineSegment(sketch, "E350", {"start": v(-42.62, -36.75) * mm, "end": v(-42.34, -36.75) * mm});
            skLineSegment(sketch, "E351", {"start": v(-42.34, -36.75) * mm, "end": v(-42.07, -36.75) * mm});
            skLineSegment(sketch, "E352", {"start": v(-42.07, -36.75) * mm, "end": v(-42.07, -35.33) * mm});
            skLineSegment(sketch, "E353", {"start": v(-42.07, -35.33) * mm, "end": v(-42.07, -33.91) * mm});
            skLineSegment(sketch, "E354", {"start": v(-42.07, -33.91) * mm, "end": v(-42.07, -32.5) * mm});
            skLineSegment(sketch, "E355", {"start": v(-42.07, -32.5) * mm, "end": v(-42.07, -31.07) * mm});
            skLineSegment(sketch, "E356", {"start": v(-42.07, -31.07) * mm, "end": v(-42.07, -29.65) * mm});
            skLineSegment(sketch, "E357", {"start": v(-42.07, -29.65) * mm, "end": v(-42.07, -28.24) * mm});
            skLineSegment(sketch, "E358", {"start": v(-42.07, -28.24) * mm, "end": v(-42.07, -26.82) * mm});
            skLineSegment(sketch, "E359", {"start": v(-42.07, -26.82) * mm, "end": v(-42.07, -25.4) * mm});
            skLineSegment(sketch, "E360", {"start": v(-42.07, -25.4) * mm, "end": v(-42.07, -23.98) * mm});
            skLineSegment(sketch, "E361", {"start": v(-42.07, -23.98) * mm, "end": v(-42.07, -22.56) * mm});
            skLineSegment(sketch, "E362", {"start": v(-42.07, -22.56) * mm, "end": v(-42.07, -21.14) * mm});
            skLineSegment(sketch, "E363", {"start": v(-42.07, -21.14) * mm, "end": v(-42.07, -19.72) * mm});
            skLineSegment(sketch, "E364", {"start": v(-42.07, -19.72) * mm, "end": v(-42.07, -18.3) * mm});
            skLineSegment(sketch, "E365", {"start": v(-42.07, -18.3) * mm, "end": v(-42.07, -16.88) * mm});
            skLineSegment(sketch, "E366", {"start": v(-42.07, -16.88) * mm, "end": v(-42.07, -15.47) * mm});
            skLineSegment(sketch, "E367", {"start": v(-42.07, -15.47) * mm, "end": v(-42.07, -14.05) * mm});
            skLineSegment(sketch, "E368", {"start": v(-42.07, -14.05) * mm, "end": v(-42.34, -14.05) * mm});
            skLineSegment(sketch, "E369", {"start": v(-42.34, -14.05) * mm, "end": v(-42.62, -14.05) * mm});
            skLineSegment(sketch, "E370", {"start": v(-42.62, -14.05) * mm, "end": v(-42.9, -14.05) * mm});
            skLineSegment(sketch, "E371", {"start": v(-42.9, -14.05) * mm, "end": v(-43.17, -14.05) * mm});
            skLineSegment(sketch, "E372", {"start": v(-43.17, -14.05) * mm, "end": v(-43.44, -14.05) * mm});
            skLineSegment(sketch, "E373", {"start": v(-43.44, -14.05) * mm, "end": v(-43.72, -14.05) * mm});
            skLineSegment(sketch, "E374", {"start": v(-43.72, -14.05) * mm, "end": v(-44, -14.05) * mm});
            skLineSegment(sketch, "E375", {"start": v(-44, -14.05) * mm, "end": v(-44.27, -14.05) * mm});
            skLineSegment(sketch, "E376", {"start": v(-44.27, -14.05) * mm, "end": v(-44.54, -14.05) * mm});
            skLineSegment(sketch, "E377", {"start": v(-44.54, -14.05) * mm, "end": v(-44.82, -14.05) * mm});
            skLineSegment(sketch, "E378", {"start": v(-44.82, -14.05) * mm, "end": v(-45.1, -14.05) * mm});
            skLineSegment(sketch, "E379", {"start": v(-45.1, -14.05) * mm, "end": v(-45.37, -14.05) * mm});
            skLineSegment(sketch, "E380", {"start": v(-45.37, -14.05) * mm, "end": v(-45.64, -14.05) * mm});
            skLineSegment(sketch, "E381", {"start": v(-45.64, -14.05) * mm, "end": v(-45.92, -14.05) * mm});
            skLineSegment(sketch, "E382", {"start": v(-45.92, -14.05) * mm, "end": v(-46.2, -14.05) * mm});
            skLineSegment(sketch, "E383", {"start": v(-46.2, -14.05) * mm, "end": v(-46.47, -14.05) * mm});
            skLineSegment(sketch, "E384", {"start": v(1.33, -14.05) * mm, "end": v(0.93, -14.71) * mm});
            skLineSegment(sketch, "E385", {"start": v(0.93, -14.71) * mm, "end": v(0.52, -15.38) * mm});
            skLineSegment(sketch, "E386", {"start": v(0.52, -15.38) * mm, "end": v(0.11, -16.05) * mm});
            skLineSegment(sketch, "E387", {"start": v(0.11, -16.05) * mm, "end": v(-0.3, -16.72) * mm});
            skLineSegment(sketch, "E388", {"start": v(-0.3, -16.72) * mm, "end": v(-0.7, -17.39) * mm});
            skLineSegment(sketch, "E389", {"start": v(-0.7, -17.39) * mm, "end": v(-1.1, -18.05) * mm});
            skLineSegment(sketch, "E390", {"start": v(-1.1, -18.05) * mm, "end": v(-1.51, -18.72) * mm});
            skLineSegment(sketch, "E391", {"start": v(-1.51, -18.72) * mm, "end": v(-1.92, -19.39) * mm});
            skLineSegment(sketch, "E392", {"start": v(-1.92, -19.39) * mm, "end": v(-2.32, -20.06) * mm});
            skLineSegment(sketch, "E393", {"start": v(-2.32, -20.06) * mm, "end": v(-2.73, -20.73) * mm});
            skLineSegment(sketch, "E394", {"start": v(-2.73, -20.73) * mm, "end": v(-3.14, -21.4) * mm});
            skLineSegment(sketch, "E395", {"start": v(-3.14, -21.4) * mm, "end": v(-3.54, -22.06) * mm});
            skLineSegment(sketch, "E396", {"start": v(-3.54, -22.06) * mm, "end": v(-3.95, -22.73) * mm});
            skLineSegment(sketch, "E397", {"start": v(-3.95, -22.73) * mm, "end": v(-4.35, -23.4) * mm});
            skLineSegment(sketch, "E398", {"start": v(-4.35, -23.4) * mm, "end": v(-4.76, -24.06) * mm});
            skLineSegment(sketch, "E399", {"start": v(-4.76, -24.06) * mm, "end": v(-5.17, -24.73) * mm});
            skLineSegment(sketch, "E400", {"start": v(-5.17, -24.73) * mm, "end": v(-5.59, -24.06) * mm});
            skLineSegment(sketch, "E401", {"start": v(-5.59, -24.06) * mm, "end": v(-6.01, -23.4) * mm});
            skLineSegment(sketch, "E402", {"start": v(-6.01, -23.4) * mm, "end": v(-6.43, -22.73) * mm});
            skLineSegment(sketch, "E403", {"start": v(-6.43, -22.73) * mm, "end": v(-6.86, -22.06) * mm});
            skLineSegment(sketch, "E404", {"start": v(-6.86, -22.06) * mm, "end": v(-7.28, -21.4) * mm});
            skLineSegment(sketch, "E405", {"start": v(-7.28, -21.4) * mm, "end": v(-7.7, -20.73) * mm});
            skLineSegment(sketch, "E406", {"start": v(-7.7, -20.73) * mm, "end": v(-8.13, -20.06) * mm});
            skLineSegment(sketch, "E407", {"start": v(-8.13, -20.06) * mm, "end": v(-8.55, -19.39) * mm});
            skLineSegment(sketch, "E408", {"start": v(-8.55, -19.39) * mm, "end": v(-8.97, -18.72) * mm});
            skLineSegment(sketch, "E409", {"start": v(-8.97, -18.72) * mm, "end": v(-9.4, -18.05) * mm});
            skLineSegment(sketch, "E410", {"start": v(-9.4, -18.05) * mm, "end": v(-9.82, -17.39) * mm});
            skLineSegment(sketch, "E411", {"start": v(-9.82, -17.39) * mm, "end": v(-10.24, -16.72) * mm});
            skLineSegment(sketch, "E412", {"start": v(-10.24, -16.72) * mm, "end": v(-10.66, -16.05) * mm});
            skLineSegment(sketch, "E413", {"start": v(-10.66, -16.05) * mm, "end": v(-11.09, -15.38) * mm});
            skLineSegment(sketch, "E414", {"start": v(-11.09, -15.38) * mm, "end": v(-11.5, -14.71) * mm});
            skLineSegment(sketch, "E415", {"start": v(-11.5, -14.71) * mm, "end": v(-11.93, -14.05) * mm});
            skLineSegment(sketch, "E416", {"start": v(-11.93, -14.05) * mm, "end": v(-12.2, -14.05) * mm});
            skLineSegment(sketch, "E417", {"start": v(-12.2, -14.05) * mm, "end": v(-12.45, -14.05) * mm});
            skLineSegment(sketch, "E418", {"start": v(-12.45, -14.05) * mm, "end": v(-12.7, -14.05) * mm});
            skLineSegment(sketch, "E419", {"start": v(-12.7, -14.05) * mm, "end": v(-12.97, -14.05) * mm});
            skLineSegment(sketch, "E420", {"start": v(-12.97, -14.05) * mm, "end": v(-13.22, -14.05) * mm});
            skLineSegment(sketch, "E421", {"start": v(-13.22, -14.05) * mm, "end": v(-13.48, -14.05) * mm});
            skLineSegment(sketch, "E422", {"start": v(-13.48, -14.05) * mm, "end": v(-13.74, -14.05) * mm});
            skLineSegment(sketch, "E423", {"start": v(-13.74, -14.05) * mm, "end": v(-14, -14.05) * mm});
            skLineSegment(sketch, "E424", {"start": v(-14, -14.05) * mm, "end": v(-14.26, -14.05) * mm});
            skLineSegment(sketch, "E425", {"start": v(-14.26, -14.05) * mm, "end": v(-14.52, -14.05) * mm});
            skLineSegment(sketch, "E426", {"start": v(-14.52, -14.05) * mm, "end": v(-14.77, -14.05) * mm});
            skLineSegment(sketch, "E427", {"start": v(-14.77, -14.05) * mm, "end": v(-15.03, -14.05) * mm});
            skLineSegment(sketch, "E428", {"start": v(-15.03, -14.05) * mm, "end": v(-15.3, -14.05) * mm});
            skLineSegment(sketch, "E429", {"start": v(-15.3, -14.05) * mm, "end": v(-15.55, -14.05) * mm});
            skLineSegment(sketch, "E430", {"start": v(-15.55, -14.05) * mm, "end": v(-15.8, -14.05) * mm});
            skLineSegment(sketch, "E431", {"start": v(-15.8, -14.05) * mm, "end": v(-16.07, -14.05) * mm});
            skLineSegment(sketch, "E432", {"start": v(-16.07, -14.05) * mm, "end": v(-16.07, -15.47) * mm});
            skLineSegment(sketch, "E433", {"start": v(-16.07, -15.47) * mm, "end": v(-16.07, -16.88) * mm});
            skLineSegment(sketch, "E434", {"start": v(-16.07, -16.88) * mm, "end": v(-16.07, -18.3) * mm});
            skLineSegment(sketch, "E435", {"start": v(-16.07, -18.3) * mm, "end": v(-16.07, -19.72) * mm});
            skLineSegment(sketch, "E436", {"start": v(-16.07, -19.72) * mm, "end": v(-16.07, -21.14) * mm});
            skLineSegment(sketch, "E437", {"start": v(-16.07, -21.14) * mm, "end": v(-16.07, -22.56) * mm});
            skLineSegment(sketch, "E438", {"start": v(-16.07, -22.56) * mm, "end": v(-16.07, -23.98) * mm});
            skLineSegment(sketch, "E439", {"start": v(-16.07, -23.98) * mm, "end": v(-16.07, -25.4) * mm});
            skLineSegment(sketch, "E440", {"start": v(-16.07, -25.4) * mm, "end": v(-16.07, -26.82) * mm});
            skLineSegment(sketch, "E441", {"start": v(-16.07, -26.82) * mm, "end": v(-16.07, -28.24) * mm});
            skLineSegment(sketch, "E442", {"start": v(-16.07, -28.24) * mm, "end": v(-16.07, -29.65) * mm});
            skLineSegment(sketch, "E443", {"start": v(-16.07, -29.65) * mm, "end": v(-16.07, -31.07) * mm});
            skLineSegment(sketch, "E444", {"start": v(-16.07, -31.07) * mm, "end": v(-16.07, -32.5) * mm});
            skLineSegment(sketch, "E445", {"start": v(-16.07, -32.5) * mm, "end": v(-16.07, -33.91) * mm});
            skLineSegment(sketch, "E446", {"start": v(-16.07, -33.91) * mm, "end": v(-16.07, -35.33) * mm});
            skLineSegment(sketch, "E447", {"start": v(-16.07, -35.33) * mm, "end": v(-16.07, -36.75) * mm});
            skLineSegment(sketch, "E448", {"start": v(-16.07, -36.75) * mm, "end": v(-15.8, -36.75) * mm});
            skLineSegment(sketch, "E449", {"start": v(-15.8, -36.75) * mm, "end": v(-15.52, -36.75) * mm});
            skLineSegment(sketch, "E450", {"start": v(-15.52, -36.75) * mm, "end": v(-15.24, -36.75) * mm});
            skLineSegment(sketch, "E451", {"start": v(-15.24, -36.75) * mm, "end": v(-14.97, -36.75) * mm});
            skLineSegment(sketch, "E452", {"start": v(-14.97, -36.75) * mm, "end": v(-14.7, -36.75) * mm});
            skLineSegment(sketch, "E453", {"start": v(-14.7, -36.75) * mm, "end": v(-14.42, -36.75) * mm});
            skLineSegment(sketch, "E454", {"start": v(-14.42, -36.75) * mm, "end": v(-14.14, -36.75) * mm});
            skLineSegment(sketch, "E455", {"start": v(-14.14, -36.75) * mm, "end": v(-13.87, -36.75) * mm});
            skLineSegment(sketch, "E456", {"start": v(-13.87, -36.75) * mm, "end": v(-13.6, -36.75) * mm});
            skLineSegment(sketch, "E457", {"start": v(-13.6, -36.75) * mm, "end": v(-13.32, -36.75) * mm});
            skLineSegment(sketch, "E458", {"start": v(-13.32, -36.75) * mm, "end": v(-13.04, -36.75) * mm});
            skLineSegment(sketch, "E459", {"start": v(-13.04, -36.75) * mm, "end": v(-12.77, -36.75) * mm});
            skLineSegment(sketch, "E460", {"start": v(-12.77, -36.75) * mm, "end": v(-12.5, -36.75) * mm});
            skLineSegment(sketch, "E461", {"start": v(-12.5, -36.75) * mm, "end": v(-12.22, -36.75) * mm});
            skLineSegment(sketch, "E462", {"start": v(-12.22, -36.75) * mm, "end": v(-11.94, -36.75) * mm});
            skLineSegment(sketch, "E463", {"start": v(-11.94, -36.75) * mm, "end": v(-11.67, -36.75) * mm});
            skLineSegment(sketch, "E464", {"start": v(-11.67, -36.75) * mm, "end": v(-11.67, -35.83) * mm});
            skLineSegment(sketch, "E465", {"start": v(-11.67, -35.83) * mm, "end": v(-11.67, -34.92) * mm});
            skLineSegment(sketch, "E466", {"start": v(-11.67, -34.92) * mm, "end": v(-11.67, -34) * mm});
            skLineSegment(sketch, "E467", {"start": v(-11.67, -34) * mm, "end": v(-11.67, -33.09) * mm});
            skLineSegment(sketch, "E468", {"start": v(-11.67, -33.09) * mm, "end": v(-11.67, -32.17) * mm});
            skLineSegment(sketch, "E469", {"start": v(-11.67, -32.17) * mm, "end": v(-11.67, -31.26) * mm});
            skLineSegment(sketch, "E470", {"start": v(-11.67, -31.26) * mm, "end": v(-11.67, -30.34) * mm});
            skLineSegment(sketch, "E471", {"start": v(-11.67, -30.34) * mm, "end": v(-11.67, -29.42) * mm});
            skLineSegment(sketch, "E472", {"start": v(-11.67, -29.42) * mm, "end": v(-11.67, -28.5) * mm});
            skLineSegment(sketch, "E473", {"start": v(-11.67, -28.5) * mm, "end": v(-11.67, -27.6) * mm});
            skLineSegment(sketch, "E474", {"start": v(-11.67, -27.6) * mm, "end": v(-11.67, -26.68) * mm});
            skLineSegment(sketch, "E475", {"start": v(-11.67, -26.68) * mm, "end": v(-11.67, -25.76) * mm});
            skLineSegment(sketch, "E476", {"start": v(-11.67, -25.76) * mm, "end": v(-11.67, -24.85) * mm});
            skLineSegment(sketch, "E477", {"start": v(-11.67, -24.85) * mm, "end": v(-11.67, -23.93) * mm});
            skLineSegment(sketch, "E478", {"start": v(-11.67, -23.93) * mm, "end": v(-11.67, -23.02) * mm});
            skLineSegment(sketch, "E479", {"start": v(-11.67, -23.02) * mm, "end": v(-11.67, -22.1) * mm});
            skLineSegment(sketch, "E480", {"start": v(-11.67, -22.1) * mm, "end": v(-11.33, -22.62) * mm});
            skLineSegment(sketch, "E481", {"start": v(-11.33, -22.62) * mm, "end": v(-11, -23.13) * mm});
            skLineSegment(sketch, "E482", {"start": v(-11, -23.13) * mm, "end": v(-10.67, -23.65) * mm});
            skLineSegment(sketch, "E483", {"start": v(-10.67, -23.65) * mm, "end": v(-10.34, -24.17) * mm});
            skLineSegment(sketch, "E484", {"start": v(-10.34, -24.17) * mm, "end": v(-10, -24.68) * mm});
            skLineSegment(sketch, "E485", {"start": v(-10, -24.68) * mm, "end": v(-9.68, -25.2) * mm});
            skLineSegment(sketch, "E486", {"start": v(-9.68, -25.2) * mm, "end": v(-9.35, -25.71) * mm});
            skLineSegment(sketch, "E487", {"start": v(-9.35, -25.71) * mm, "end": v(-9.02, -26.23) * mm});
            skLineSegment(sketch, "E488", {"start": v(-9.02, -26.23) * mm, "end": v(-8.68, -26.75) * mm});
            skLineSegment(sketch, "E489", {"start": v(-8.68, -26.75) * mm, "end": v(-8.35, -27.26) * mm});
            skLineSegment(sketch, "E490", {"start": v(-8.35, -27.26) * mm, "end": v(-8.02, -27.78) * mm});
            skLineSegment(sketch, "E491", {"start": v(-8.02, -27.78) * mm, "end": v(-7.7, -28.3) * mm});
            skLineSegment(sketch, "E492", {"start": v(-7.7, -28.3) * mm, "end": v(-7.36, -28.81) * mm});
            skLineSegment(sketch, "E493", {"start": v(-7.36, -28.81) * mm, "end": v(-7.03, -29.33) * mm});
            skLineSegment(sketch, "E494", {"start": v(-7.03, -29.33) * mm, "end": v(-6.7, -29.84) * mm});
            skLineSegment(sketch, "E495", {"start": v(-6.7, -29.84) * mm, "end": v(-6.37, -30.36) * mm});
            skLineSegment(sketch, "E496", {"start": v(-6.37, -30.36) * mm, "end": v(-6.23, -30.36) * mm});
            skLineSegment(sketch, "E497", {"start": v(-6.23, -30.36) * mm, "end": v(-6.1, -30.36) * mm});
            skLineSegment(sketch, "E498", {"start": v(-6.1, -30.36) * mm, "end": v(-5.97, -30.36) * mm});
            skLineSegment(sketch, "E499", {"start": v(-5.97, -30.36) * mm, "end": v(-5.83, -30.36) * mm});
            skLineSegment(sketch, "E500", {"start": v(-5.83, -30.36) * mm, "end": v(-5.7, -30.36) * mm});
            skLineSegment(sketch, "E501", {"start": v(-5.7, -30.36) * mm, "end": v(-5.57, -30.36) * mm});
            skLineSegment(sketch, "E502", {"start": v(-5.57, -30.36) * mm, "end": v(-5.43, -30.36) * mm});
            skLineSegment(sketch, "E503", {"start": v(-5.43, -30.36) * mm, "end": v(-5.3, -30.36) * mm});
            skLineSegment(sketch, "E504", {"start": v(-5.3, -30.36) * mm, "end": v(-5.17, -30.36) * mm});
            skLineSegment(sketch, "E505", {"start": v(-5.17, -30.36) * mm, "end": v(-5.03, -30.36) * mm});
            skLineSegment(sketch, "E506", {"start": v(-5.03, -30.36) * mm, "end": v(-4.9, -30.36) * mm});
            skLineSegment(sketch, "E507", {"start": v(-4.9, -30.36) * mm, "end": v(-4.77, -30.36) * mm});
            skLineSegment(sketch, "E508", {"start": v(-4.77, -30.36) * mm, "end": v(-4.63, -30.36) * mm});
            skLineSegment(sketch, "E509", {"start": v(-4.63, -30.36) * mm, "end": v(-4.5, -30.36) * mm});
            skLineSegment(sketch, "E510", {"start": v(-4.5, -30.36) * mm, "end": v(-4.37, -30.36) * mm});
            skLineSegment(sketch, "E511", {"start": v(-4.37, -30.36) * mm, "end": v(-4.23, -30.36) * mm});
            skLineSegment(sketch, "E512", {"start": v(-4.23, -30.36) * mm, "end": v(-3.92, -29.85) * mm});
            skLineSegment(sketch, "E513", {"start": v(-3.92, -29.85) * mm, "end": v(-3.61, -29.34) * mm});
            skLineSegment(sketch, "E514", {"start": v(-3.61, -29.34) * mm, "end": v(-3.3, -28.83) * mm});
            skLineSegment(sketch, "E515", {"start": v(-3.3, -28.83) * mm, "end": v(-3, -28.32) * mm});
            skLineSegment(sketch, "E516", {"start": v(-3, -28.32) * mm, "end": v(-2.68, -27.8) * mm});
            skLineSegment(sketch, "E517", {"start": v(-2.68, -27.8) * mm, "end": v(-2.37, -27.3) * mm});
            skLineSegment(sketch, "E518", {"start": v(-2.37, -27.3) * mm, "end": v(-2.06, -26.79) * mm});
            skLineSegment(sketch, "E519", {"start": v(-2.06, -26.79) * mm, "end": v(-1.75, -26.28) * mm});
            skLineSegment(sketch, "E520", {"start": v(-1.75, -26.28) * mm, "end": v(-1.44, -25.77) * mm});
            skLineSegment(sketch, "E521", {"start": v(-1.44, -25.77) * mm, "end": v(-1.13, -25.26) * mm});
            skLineSegment(sketch, "E522", {"start": v(-1.13, -25.26) * mm, "end": v(-0.82, -24.75) * mm});
            skLineSegment(sketch, "E523", {"start": v(-0.82, -24.75) * mm, "end": v(-0.5, -24.24) * mm});
            skLineSegment(sketch, "E524", {"start": v(-0.5, -24.24) * mm, "end": v(-0.2, -23.73) * mm});
            skLineSegment(sketch, "E525", {"start": v(-0.2, -23.73) * mm, "end": v(0.11, -23.22) * mm});
            skLineSegment(sketch, "E526", {"start": v(0.11, -23.22) * mm, "end": v(0.42, -22.71) * mm});
            skLineSegment(sketch, "E527", {"start": v(0.42, -22.71) * mm, "end": v(0.73, -22.2) * mm});
            skLineSegment(sketch, "E528", {"start": v(0.73, -22.2) * mm, "end": v(0.73, -23.11) * mm});
            skLineSegment(sketch, "E529", {"start": v(0.73, -23.11) * mm, "end": v(0.73, -24.02) * mm});
            skLineSegment(sketch, "E530", {"start": v(0.73, -24.02) * mm, "end": v(0.73, -24.93) * mm});
            skLineSegment(sketch, "E531", {"start": v(0.73, -24.93) * mm, "end": v(0.73, -25.84) * mm});
            skLineSegment(sketch, "E532", {"start": v(0.73, -25.84) * mm, "end": v(0.73, -26.75) * mm});
            skLineSegment(sketch, "E533", {"start": v(0.73, -26.75) * mm, "end": v(0.73, -27.66) * mm});
            skLineSegment(sketch, "E534", {"start": v(0.73, -27.66) * mm, "end": v(0.73, -28.57) * mm});
            skLineSegment(sketch, "E535", {"start": v(0.73, -28.57) * mm, "end": v(0.73, -29.48) * mm});
            skLineSegment(sketch, "E536", {"start": v(0.73, -29.48) * mm, "end": v(0.73, -30.38) * mm});
            skLineSegment(sketch, "E537", {"start": v(0.73, -30.38) * mm, "end": v(0.73, -31.3) * mm});
            skLineSegment(sketch, "E538", {"start": v(0.73, -31.3) * mm, "end": v(0.73, -32.2) * mm});
            skLineSegment(sketch, "E539", {"start": v(0.73, -32.2) * mm, "end": v(0.73, -33.11) * mm});
            skLineSegment(sketch, "E540", {"start": v(0.73, -33.11) * mm, "end": v(0.73, -34.02) * mm});
            skLineSegment(sketch, "E541", {"start": v(0.73, -34.02) * mm, "end": v(0.73, -34.93) * mm});
            skLineSegment(sketch, "E542", {"start": v(0.73, -34.93) * mm, "end": v(0.73, -35.84) * mm});
            skLineSegment(sketch, "E543", {"start": v(0.73, -35.84) * mm, "end": v(0.73, -36.75) * mm});
            skLineSegment(sketch, "E544", {"start": v(0.73, -36.75) * mm, "end": v(1.01, -36.75) * mm});
            skLineSegment(sketch, "E545", {"start": v(1.01, -36.75) * mm, "end": v(1.29, -36.75) * mm});
            skLineSegment(sketch, "E546", {"start": v(1.29, -36.75) * mm, "end": v(1.57, -36.75) * mm});
            skLineSegment(sketch, "E547", {"start": v(1.57, -36.75) * mm, "end": v(1.84, -36.75) * mm});
            skLineSegment(sketch, "E548", {"start": v(1.84, -36.75) * mm, "end": v(2.12, -36.75) * mm});
            skLineSegment(sketch, "E549", {"start": v(2.12, -36.75) * mm, "end": v(2.4, -36.75) * mm});
            skLineSegment(sketch, "E550", {"start": v(2.4, -36.75) * mm, "end": v(2.67, -36.75) * mm});
            skLineSegment(sketch, "E551", {"start": v(2.67, -36.75) * mm, "end": v(2.95, -36.75) * mm});
            skLineSegment(sketch, "E552", {"start": v(2.95, -36.75) * mm, "end": v(3.23, -36.75) * mm});
            skLineSegment(sketch, "E553", {"start": v(3.23, -36.75) * mm, "end": v(3.5, -36.75) * mm});
            skLineSegment(sketch, "E554", {"start": v(3.5, -36.75) * mm, "end": v(3.78, -36.75) * mm});
            skLineSegment(sketch, "E555", {"start": v(3.78, -36.75) * mm, "end": v(4.06, -36.75) * mm});
            skLineSegment(sketch, "E556", {"start": v(4.06, -36.75) * mm, "end": v(4.34, -36.75) * mm});
            skLineSegment(sketch, "E557", {"start": v(4.34, -36.75) * mm, "end": v(4.61, -36.75) * mm});
            skLineSegment(sketch, "E558", {"start": v(4.61, -36.75) * mm, "end": v(4.89, -36.75) * mm});
            skLineSegment(sketch, "E559", {"start": v(4.89, -36.75) * mm, "end": v(5.17, -36.75) * mm});
            skLineSegment(sketch, "E560", {"start": v(5.17, -36.75) * mm, "end": v(5.17, -35.33) * mm});
            skLineSegment(sketch, "E561", {"start": v(5.17, -35.33) * mm, "end": v(5.17, -33.91) * mm});
            skLineSegment(sketch, "E562", {"start": v(5.17, -33.91) * mm, "end": v(5.17, -32.5) * mm});
            skLineSegment(sketch, "E563", {"start": v(5.17, -32.5) * mm, "end": v(5.17, -31.07) * mm});
            skLineSegment(sketch, "E564", {"start": v(5.17, -31.07) * mm, "end": v(5.17, -29.65) * mm});
            skLineSegment(sketch, "E565", {"start": v(5.17, -29.65) * mm, "end": v(5.17, -28.24) * mm});
            skLineSegment(sketch, "E566", {"start": v(5.17, -28.24) * mm, "end": v(5.17, -26.82) * mm});
            skLineSegment(sketch, "E567", {"start": v(5.17, -26.82) * mm, "end": v(5.17, -25.4) * mm});
            skLineSegment(sketch, "E568", {"start": v(5.17, -25.4) * mm, "end": v(5.17, -23.98) * mm});
            skLineSegment(sketch, "E569", {"start": v(5.17, -23.98) * mm, "end": v(5.17, -22.56) * mm});
            skLineSegment(sketch, "E570", {"start": v(5.17, -22.56) * mm, "end": v(5.17, -21.14) * mm});
            skLineSegment(sketch, "E571", {"start": v(5.17, -21.14) * mm, "end": v(5.17, -19.72) * mm});
            skLineSegment(sketch, "E572", {"start": v(5.17, -19.72) * mm, "end": v(5.17, -18.3) * mm});
            skLineSegment(sketch, "E573", {"start": v(5.17, -18.3) * mm, "end": v(5.17, -16.88) * mm});
            skLineSegment(sketch, "E574", {"start": v(5.17, -16.88) * mm, "end": v(5.17, -15.47) * mm});
            skLineSegment(sketch, "E575", {"start": v(5.17, -15.47) * mm, "end": v(5.17, -14.05) * mm});
            skLineSegment(sketch, "E576", {"start": v(5.17, -14.05) * mm, "end": v(4.93, -14.05) * mm});
            skLineSegment(sketch, "E577", {"start": v(4.93, -14.05) * mm, "end": v(4.69, -14.05) * mm});
            skLineSegment(sketch, "E578", {"start": v(4.69, -14.05) * mm, "end": v(4.45, -14.05) * mm});
            skLineSegment(sketch, "E579", {"start": v(4.45, -14.05) * mm, "end": v(4.2, -14.05) * mm});
            skLineSegment(sketch, "E580", {"start": v(4.2, -14.05) * mm, "end": v(3.97, -14.05) * mm});
            skLineSegment(sketch, "E581", {"start": v(3.97, -14.05) * mm, "end": v(3.73, -14.05) * mm});
            skLineSegment(sketch, "E582", {"start": v(3.73, -14.05) * mm, "end": v(3.49, -14.05) * mm});
            skLineSegment(sketch, "E583", {"start": v(3.49, -14.05) * mm, "end": v(3.25, -14.05) * mm});
            skLineSegment(sketch, "E584", {"start": v(3.25, -14.05) * mm, "end": v(3.01, -14.05) * mm});
            skLineSegment(sketch, "E585", {"start": v(3.01, -14.05) * mm, "end": v(2.77, -14.05) * mm});
            skLineSegment(sketch, "E586", {"start": v(2.77, -14.05) * mm, "end": v(2.53, -14.05) * mm});
            skLineSegment(sketch, "E587", {"start": v(2.53, -14.05) * mm, "end": v(2.3, -14.05) * mm});
            skLineSegment(sketch, "E588", {"start": v(2.3, -14.05) * mm, "end": v(2.05, -14.05) * mm});
            skLineSegment(sketch, "E589", {"start": v(2.05, -14.05) * mm, "end": v(1.81, -14.05) * mm});
            skLineSegment(sketch, "E590", {"start": v(1.81, -14.05) * mm, "end": v(1.57, -14.05) * mm});
            skLineSegment(sketch, "E591", {"start": v(1.57, -14.05) * mm, "end": v(1.33, -14.05) * mm});
            skLineSegment(sketch, "E592", {"start": v(13.9, -18.07) * mm, "end": v(14.33, -18.07) * mm});
            skLineSegment(sketch, "E593", {"start": v(14.33, -18.07) * mm, "end": v(14.75, -18.07) * mm});
            skLineSegment(sketch, "E594", {"start": v(14.75, -18.07) * mm, "end": v(15.18, -18.07) * mm});
            skLineSegment(sketch, "E595", {"start": v(15.18, -18.07) * mm, "end": v(15.6, -18.07) * mm});
            skLineSegment(sketch, "E596", {"start": v(15.6, -18.07) * mm, "end": v(16.04, -18.07) * mm});
            skLineSegment(sketch, "E597", {"start": v(16.04, -18.07) * mm, "end": v(16.46, -18.07) * mm});
            skLineSegment(sketch, "E598", {"start": v(16.46, -18.07) * mm, "end": v(16.89, -18.07) * mm});
            skLineSegment(sketch, "E599", {"start": v(16.89, -18.07) * mm, "end": v(17.32, -18.07) * mm});
            skLineSegment(sketch, "E600", {"start": v(17.32, -18.07) * mm, "end": v(17.74, -18.07) * mm});
            skLineSegment(sketch, "E601", {"start": v(17.74, -18.07) * mm, "end": v(18.17, -18.07) * mm});
            skLineSegment(sketch, "E602", {"start": v(18.17, -18.07) * mm, "end": v(18.6, -18.07) * mm});
            skLineSegment(sketch, "E603", {"start": v(18.6, -18.07) * mm, "end": v(19.03, -18.07) * mm});
            skLineSegment(sketch, "E604", {"start": v(19.03, -18.07) * mm, "end": v(19.45, -18.07) * mm});
            skLineSegment(sketch, "E605", {"start": v(19.45, -18.07) * mm, "end": v(19.88, -18.07) * mm});
            skLineSegment(sketch, "E606", {"start": v(19.88, -18.07) * mm, "end": v(20.3, -18.07) * mm});
            skLineSegment(sketch, "E607", {"start": v(20.3, -18.07) * mm, "end": v(20.73, -18.07) * mm});
            skLineSegment(sketch, "E608", {"start": v(20.73, -18.07) * mm, "end": v(20.85, -18.08) * mm});
            skLineSegment(sketch, "E609", {"start": v(20.85, -18.08) * mm, "end": v(20.96, -18.1) * mm});
            skLineSegment(sketch, "E610", {"start": v(20.96, -18.1) * mm, "end": v(21.07, -18.13) * mm});
            skLineSegment(sketch, "E611", {"start": v(21.07, -18.13) * mm, "end": v(21.18, -18.17) * mm});
            skLineSegment(sketch, "E612", {"start": v(21.18, -18.17) * mm, "end": v(21.28, -18.22) * mm});
            skLineSegment(sketch, "E613", {"start": v(21.28, -18.22) * mm, "end": v(21.37, -18.28) * mm});
            skLineSegment(sketch, "E614", {"start": v(21.37, -18.28) * mm, "end": v(21.46, -18.34) * mm});
            skLineSegment(sketch, "E615", {"start": v(21.46, -18.34) * mm, "end": v(21.54, -18.42) * mm});
            skLineSegment(sketch, "E616", {"start": v(21.54, -18.42) * mm, "end": v(21.61, -18.5) * mm});
            skLineSegment(sketch, "E617", {"start": v(21.61, -18.5) * mm, "end": v(21.68, -18.6) * mm});
            skLineSegment(sketch, "E618", {"start": v(21.68, -18.6) * mm, "end": v(21.73, -18.69) * mm});
            skLineSegment(sketch, "E619", {"start": v(21.73, -18.69) * mm, "end": v(21.78, -18.8) * mm});
            skLineSegment(sketch, "E620", {"start": v(21.78, -18.8) * mm, "end": v(21.82, -18.9) * mm});
            skLineSegment(sketch, "E621", {"start": v(21.82, -18.9) * mm, "end": v(21.84, -19) * mm});
            skLineSegment(sketch, "E622", {"start": v(21.84, -19) * mm, "end": v(21.86, -19.12) * mm});
            skLineSegment(sketch, "E623", {"start": v(21.86, -19.12) * mm, "end": v(21.87, -19.24) * mm});
            skLineSegment(sketch, "E624", {"start": v(21.87, -19.24) * mm, "end": v(21.87, -19.43) * mm});
            skLineSegment(sketch, "E625", {"start": v(21.87, -19.43) * mm, "end": v(21.87, -19.63) * mm});
            skLineSegment(sketch, "E626", {"start": v(21.87, -19.63) * mm, "end": v(21.87, -19.82) * mm});
            skLineSegment(sketch, "E627", {"start": v(21.87, -19.82) * mm, "end": v(21.87, -20.01) * mm});
            skLineSegment(sketch, "E628", {"start": v(21.87, -20.01) * mm, "end": v(21.87, -20.2) * mm});
            skLineSegment(sketch, "E629", {"start": v(21.87, -20.2) * mm, "end": v(21.87, -20.4) * mm});
            skLineSegment(sketch, "E630", {"start": v(21.87, -20.4) * mm, "end": v(21.87, -20.6) * mm});
            skLineSegment(sketch, "E631", {"start": v(21.87, -20.6) * mm, "end": v(21.87, -20.79) * mm});
            skLineSegment(sketch, "E632", {"start": v(21.87, -20.79) * mm, "end": v(21.87, -20.98) * mm});
            skLineSegment(sketch, "E633", {"start": v(21.87, -20.98) * mm, "end": v(21.87, -21.17) * mm});
            skLineSegment(sketch, "E634", {"start": v(21.87, -21.17) * mm, "end": v(21.87, -21.37) * mm});
            skLineSegment(sketch, "E635", {"start": v(21.87, -21.37) * mm, "end": v(21.87, -21.56) * mm});
            skLineSegment(sketch, "E636", {"start": v(21.87, -21.56) * mm, "end": v(21.87, -21.75) * mm});
            skLineSegment(sketch, "E637", {"start": v(21.87, -21.75) * mm, "end": v(21.87, -21.95) * mm});
            skLineSegment(sketch, "E638", {"start": v(21.87, -21.95) * mm, "end": v(21.87, -22.14) * mm});
            skLineSegment(sketch, "E639", {"start": v(21.87, -22.14) * mm, "end": v(21.87, -22.34) * mm});
            skLineSegment(sketch, "E640", {"start": v(21.87, -22.34) * mm, "end": v(21.86, -22.45) * mm});
            skLineSegment(sketch, "E641", {"start": v(21.86, -22.45) * mm, "end": v(21.84, -22.57) * mm});
            skLineSegment(sketch, "E642", {"start": v(21.84, -22.57) * mm, "end": v(21.82, -22.67) * mm});
            skLineSegment(sketch, "E643", {"start": v(21.82, -22.67) * mm, "end": v(21.78, -22.78) * mm});
            skLineSegment(sketch, "E644", {"start": v(21.78, -22.78) * mm, "end": v(21.73, -22.88) * mm});
            skLineSegment(sketch, "E645", {"start": v(21.73, -22.88) * mm, "end": v(21.68, -22.97) * mm});
            skLineSegment(sketch, "E646", {"start": v(21.68, -22.97) * mm, "end": v(21.61, -23.06) * mm});
            skLineSegment(sketch, "E647", {"start": v(21.61, -23.06) * mm, "end": v(21.54, -23.14) * mm});
            skLineSegment(sketch, "E648", {"start": v(21.54, -23.14) * mm, "end": v(21.46, -23.21) * mm});
            skLineSegment(sketch, "E649", {"start": v(21.46, -23.21) * mm, "end": v(21.37, -23.28) * mm});
            skLineSegment(sketch, "E650", {"start": v(21.37, -23.28) * mm, "end": v(21.28, -23.33) * mm});
            skLineSegment(sketch, "E651", {"start": v(21.28, -23.33) * mm, "end": v(21.18, -23.38) * mm});
            skLineSegment(sketch, "E652", {"start": v(21.18, -23.38) * mm, "end": v(21.07, -23.42) * mm});
            skLineSegment(sketch, "E653", {"start": v(21.07, -23.42) * mm, "end": v(20.96, -23.44) * mm});
            skLineSegment(sketch, "E654", {"start": v(20.96, -23.44) * mm, "end": v(20.85, -23.46) * mm});
            skLineSegment(sketch, "E655", {"start": v(20.85, -23.46) * mm, "end": v(20.73, -23.47) * mm});
            skLineSegment(sketch, "E656", {"start": v(20.73, -23.47) * mm, "end": v(20.3, -23.47) * mm});
            skLineSegment(sketch, "E657", {"start": v(20.3, -23.47) * mm, "end": v(19.88, -23.47) * mm});
            skLineSegment(sketch, "E658", {"start": v(19.88, -23.47) * mm, "end": v(19.45, -23.47) * mm});
            skLineSegment(sketch, "E659", {"start": v(19.45, -23.47) * mm, "end": v(19.03, -23.47) * mm});
            skLineSegment(sketch, "E660", {"start": v(19.03, -23.47) * mm, "end": v(18.6, -23.47) * mm});
            skLineSegment(sketch, "E661", {"start": v(18.6, -23.47) * mm, "end": v(18.17, -23.47) * mm});
            skLineSegment(sketch, "E662", {"start": v(18.17, -23.47) * mm, "end": v(17.74, -23.47) * mm});
            skLineSegment(sketch, "E663", {"start": v(17.74, -23.47) * mm, "end": v(17.32, -23.47) * mm});
            skLineSegment(sketch, "E664", {"start": v(17.32, -23.47) * mm, "end": v(16.89, -23.47) * mm});
            skLineSegment(sketch, "E665", {"start": v(16.89, -23.47) * mm, "end": v(16.46, -23.47) * mm});
            skLineSegment(sketch, "E666", {"start": v(16.46, -23.47) * mm, "end": v(16.04, -23.47) * mm});
            skLineSegment(sketch, "E667", {"start": v(16.04, -23.47) * mm, "end": v(15.6, -23.47) * mm});
            skLineSegment(sketch, "E668", {"start": v(15.6, -23.47) * mm, "end": v(15.18, -23.47) * mm});
            skLineSegment(sketch, "E669", {"start": v(15.18, -23.47) * mm, "end": v(14.75, -23.47) * mm});
            skLineSegment(sketch, "E670", {"start": v(14.75, -23.47) * mm, "end": v(14.33, -23.47) * mm});
            skLineSegment(sketch, "E671", {"start": v(14.33, -23.47) * mm, "end": v(13.9, -23.47) * mm});
            skLineSegment(sketch, "E672", {"start": v(13.9, -23.47) * mm, "end": v(13.9, -23.13) * mm});
            skLineSegment(sketch, "E673", {"start": v(13.9, -23.13) * mm, "end": v(13.9, -22.8) * mm});
            skLineSegment(sketch, "E674", {"start": v(13.9, -22.8) * mm, "end": v(13.9, -22.46) * mm});
            skLineSegment(sketch, "E675", {"start": v(13.9, -22.46) * mm, "end": v(13.9, -22.12) * mm});
            skLineSegment(sketch, "E676", {"start": v(13.9, -22.12) * mm, "end": v(13.9, -21.78) * mm});
            skLineSegment(sketch, "E677", {"start": v(13.9, -21.78) * mm, "end": v(13.9, -21.44) * mm});
            skLineSegment(sketch, "E678", {"start": v(13.9, -21.44) * mm, "end": v(13.9, -21.1) * mm});
            skLineSegment(sketch, "E679", {"start": v(13.9, -21.1) * mm, "end": v(13.9, -20.77) * mm});
            skLineSegment(sketch, "E680", {"start": v(13.9, -20.77) * mm, "end": v(13.9, -20.43) * mm});
            skLineSegment(sketch, "E681", {"start": v(13.9, -20.43) * mm, "end": v(13.9, -20.1) * mm});
            skLineSegment(sketch, "E682", {"start": v(13.9, -20.1) * mm, "end": v(13.9, -19.76) * mm});
            skLineSegment(sketch, "E683", {"start": v(13.9, -19.76) * mm, "end": v(13.9, -19.42) * mm});
            skLineSegment(sketch, "E684", {"start": v(13.9, -19.42) * mm, "end": v(13.9, -19.09) * mm});
            skLineSegment(sketch, "E685", {"start": v(13.9, -19.09) * mm, "end": v(13.9, -18.75) * mm});
            skLineSegment(sketch, "E686", {"start": v(13.9, -18.75) * mm, "end": v(13.9, -18.41) * mm});
            skLineSegment(sketch, "E687", {"start": v(13.9, -18.41) * mm, "end": v(13.9, -18.07) * mm});
            skLineSegment(sketch, "E688", {"start": v(9.5, -14.05) * mm, "end": v(9.5, -15.47) * mm});
            skLineSegment(sketch, "E689", {"start": v(9.5, -15.47) * mm, "end": v(9.5, -16.88) * mm});
            skLineSegment(sketch, "E690", {"start": v(9.5, -16.88) * mm, "end": v(9.5, -18.3) * mm});
            skLineSegment(sketch, "E691", {"start": v(9.5, -18.3) * mm, "end": v(9.5, -19.72) * mm});
            skLineSegment(sketch, "E692", {"start": v(9.5, -19.72) * mm, "end": v(9.5, -21.14) * mm});
            skLineSegment(sketch, "E693", {"start": v(9.5, -21.14) * mm, "end": v(9.5, -22.56) * mm});
            skLineSegment(sketch, "E694", {"start": v(9.5, -22.56) * mm, "end": v(9.5, -23.98) * mm});
            skLineSegment(sketch, "E695", {"start": v(9.5, -23.98) * mm, "end": v(9.5, -25.4) * mm});
            skLineSegment(sketch, "E696", {"start": v(9.5, -25.4) * mm, "end": v(9.5, -26.82) * mm});
            skLineSegment(sketch, "E697", {"start": v(9.5, -26.82) * mm, "end": v(9.5, -28.24) * mm});
            skLineSegment(sketch, "E698", {"start": v(9.5, -28.24) * mm, "end": v(9.5, -29.65) * mm});
            skLineSegment(sketch, "E699", {"start": v(9.5, -29.65) * mm, "end": v(9.5, -31.07) * mm});
            skLineSegment(sketch, "E700", {"start": v(9.5, -31.07) * mm, "end": v(9.5, -32.5) * mm});
            skLineSegment(sketch, "E701", {"start": v(9.5, -32.5) * mm, "end": v(9.5, -33.91) * mm});
            skLineSegment(sketch, "E702", {"start": v(9.5, -33.91) * mm, "end": v(9.5, -35.33) * mm});
            skLineSegment(sketch, "E703", {"start": v(9.5, -35.33) * mm, "end": v(9.5, -36.75) * mm});
            skLineSegment(sketch, "E704", {"start": v(9.5, -36.75) * mm, "end": v(9.78, -36.75) * mm});
            skLineSegment(sketch, "E705", {"start": v(9.78, -36.75) * mm, "end": v(10.05, -36.75) * mm});
            skLineSegment(sketch, "E706", {"start": v(10.05, -36.75) * mm, "end": v(10.33, -36.75) * mm});
            skLineSegment(sketch, "E707", {"start": v(10.33, -36.75) * mm, "end": v(10.6, -36.75) * mm});
            skLineSegment(sketch, "E708", {"start": v(10.6, -36.75) * mm, "end": v(10.88, -36.75) * mm});
            skLineSegment(sketch, "E709", {"start": v(10.88, -36.75) * mm, "end": v(11.15, -36.75) * mm});
            skLineSegment(sketch, "E710", {"start": v(11.15, -36.75) * mm, "end": v(11.43, -36.75) * mm});
            skLineSegment(sketch, "E711", {"start": v(11.43, -36.75) * mm, "end": v(11.7, -36.75) * mm});
            skLineSegment(sketch, "E712", {"start": v(11.7, -36.75) * mm, "end": v(11.98, -36.75) * mm});
            skLineSegment(sketch, "E713", {"start": v(11.98, -36.75) * mm, "end": v(12.25, -36.75) * mm});
            skLineSegment(sketch, "E714", {"start": v(12.25, -36.75) * mm, "end": v(12.53, -36.75) * mm});
            skLineSegment(sketch, "E715", {"start": v(12.53, -36.75) * mm, "end": v(12.8, -36.75) * mm});
            skLineSegment(sketch, "E716", {"start": v(12.8, -36.75) * mm, "end": v(13.08, -36.75) * mm});
            skLineSegment(sketch, "E717", {"start": v(13.08, -36.75) * mm, "end": v(13.35, -36.75) * mm});
            skLineSegment(sketch, "E718", {"start": v(13.35, -36.75) * mm, "end": v(13.63, -36.75) * mm});
            skLineSegment(sketch, "E719", {"start": v(13.63, -36.75) * mm, "end": v(13.9, -36.75) * mm});
            skLineSegment(sketch, "E720", {"start": v(13.9, -36.75) * mm, "end": v(13.9, -36.17) * mm});
            skLineSegment(sketch, "E721", {"start": v(13.9, -36.17) * mm, "end": v(13.9, -35.6) * mm});
            skLineSegment(sketch, "E722", {"start": v(13.9, -35.6) * mm, "end": v(13.9, -35.01) * mm});
            skLineSegment(sketch, "E723", {"start": v(13.9, -35.01) * mm, "end": v(13.9, -34.44) * mm});
            skLineSegment(sketch, "E724", {"start": v(13.9, -34.44) * mm, "end": v(13.9, -33.86) * mm});
            skLineSegment(sketch, "E725", {"start": v(13.9, -33.86) * mm, "end": v(13.9, -33.28) * mm});
            skLineSegment(sketch, "E726", {"start": v(13.9, -33.28) * mm, "end": v(13.9, -32.7) * mm});
            skLineSegment(sketch, "E727", {"start": v(13.9, -32.7) * mm, "end": v(13.9, -32.12) * mm});
            skLineSegment(sketch, "E728", {"start": v(13.9, -32.12) * mm, "end": v(13.9, -31.54) * mm});
            skLineSegment(sketch, "E729", {"start": v(13.9, -31.54) * mm, "end": v(13.9, -30.96) * mm});
            skLineSegment(sketch, "E730", {"start": v(13.9, -30.96) * mm, "end": v(13.9, -30.39) * mm});
            skLineSegment(sketch, "E731", {"start": v(13.9, -30.39) * mm, "end": v(13.9, -29.8) * mm});
            skLineSegment(sketch, "E732", {"start": v(13.9, -29.8) * mm, "end": v(13.9, -29.23) * mm});
            skLineSegment(sketch, "E733", {"start": v(13.9, -29.23) * mm, "end": v(13.9, -28.65) * mm});
            skLineSegment(sketch, "E734", {"start": v(13.9, -28.65) * mm, "end": v(13.9, -28.07) * mm});
            skLineSegment(sketch, "E735", {"start": v(13.9, -28.07) * mm, "end": v(13.9, -27.5) * mm});
            skLineSegment(sketch, "E736", {"start": v(13.9, -27.5) * mm, "end": v(14.44, -27.5) * mm});
            skLineSegment(sketch, "E737", {"start": v(14.44, -27.5) * mm, "end": v(14.97, -27.5) * mm});
            skLineSegment(sketch, "E738", {"start": v(14.97, -27.5) * mm, "end": v(15.5, -27.5) * mm});
            skLineSegment(sketch, "E739", {"start": v(15.5, -27.5) * mm, "end": v(16.04, -27.5) * mm});
            skLineSegment(sketch, "E740", {"start": v(16.04, -27.5) * mm, "end": v(16.58, -27.5) * mm});
            skLineSegment(sketch, "E741", {"start": v(16.58, -27.5) * mm, "end": v(17.11, -27.5) * mm});
            skLineSegment(sketch, "E742", {"start": v(17.11, -27.5) * mm, "end": v(17.65, -27.5) * mm});
            skLineSegment(sketch, "E743", {"start": v(17.65, -27.5) * mm, "end": v(18.18, -27.5) * mm});
            skLineSegment(sketch, "E744", {"start": v(18.18, -27.5) * mm, "end": v(18.72, -27.5) * mm});
            skLineSegment(sketch, "E745", {"start": v(18.72, -27.5) * mm, "end": v(19.26, -27.5) * mm});
            skLineSegment(sketch, "E746", {"start": v(19.26, -27.5) * mm, "end": v(19.8, -27.5) * mm});
            skLineSegment(sketch, "E747", {"start": v(19.8, -27.5) * mm, "end": v(20.33, -27.5) * mm});
            skLineSegment(sketch, "E748", {"start": v(20.33, -27.5) * mm, "end": v(20.86, -27.5) * mm});
            skLineSegment(sketch, "E749", {"start": v(20.86, -27.5) * mm, "end": v(21.4, -27.5) * mm});
            skLineSegment(sketch, "E750", {"start": v(21.4, -27.5) * mm, "end": v(21.93, -27.5) * mm});
            skLineSegment(sketch, "E751", {"start": v(21.93, -27.5) * mm, "end": v(22.47, -27.5) * mm});
            skLineSegment(sketch, "E752", {"start": v(22.47, -27.5) * mm, "end": v(22.86, -27.48) * mm});
            skLineSegment(sketch, "E753", {"start": v(22.86, -27.48) * mm, "end": v(23.23, -27.42) * mm});
            skLineSegment(sketch, "E754", {"start": v(23.23, -27.42) * mm, "end": v(23.6, -27.32) * mm});
            skLineSegment(sketch, "E755", {"start": v(23.6, -27.32) * mm, "end": v(23.95, -27.2) * mm});
            skLineSegment(sketch, "E756", {"start": v(23.95, -27.2) * mm, "end": v(24.28, -27.04) * mm});
            skLineSegment(sketch, "E757", {"start": v(24.28, -27.04) * mm, "end": v(24.6, -26.85) * mm});
            skLineSegment(sketch, "E758", {"start": v(24.6, -26.85) * mm, "end": v(24.88, -26.63) * mm});
            skLineSegment(sketch, "E759", {"start": v(24.88, -26.63) * mm, "end": v(25.15, -26.38) * mm});
            skLineSegment(sketch, "E760", {"start": v(25.15, -26.38) * mm, "end": v(25.4, -26.11) * mm});
            skLineSegment(sketch, "E761", {"start": v(25.4, -26.11) * mm, "end": v(25.62, -25.82) * mm});
            skLineSegment(sketch, "E762", {"start": v(25.62, -25.82) * mm, "end": v(25.8, -25.5) * mm});
            skLineSegment(sketch, "E763", {"start": v(25.8, -25.5) * mm, "end": v(25.97, -25.18) * mm});
            skLineSegment(sketch, "E764", {"start": v(25.97, -25.18) * mm, "end": v(26.1, -24.83) * mm});
            skLineSegment(sketch, "E765", {"start": v(26.1, -24.83) * mm, "end": v(26.19, -24.47) * mm});
            skLineSegment(sketch, "E766", {"start": v(26.19, -24.47) * mm, "end": v(26.25, -24.09) * mm});
            skLineSegment(sketch, "E767", {"start": v(26.25, -24.09) * mm, "end": v(26.27, -23.7) * mm});
            skLineSegment(sketch, "E768", {"start": v(26.27, -23.7) * mm, "end": v(26.27, -23.33) * mm});
            skLineSegment(sketch, "E769", {"start": v(26.27, -23.33) * mm, "end": v(26.27, -22.97) * mm});
            skLineSegment(sketch, "E770", {"start": v(26.27, -22.97) * mm, "end": v(26.27, -22.6) * mm});
            skLineSegment(sketch, "E771", {"start": v(26.27, -22.6) * mm, "end": v(26.27, -22.24) * mm});
            skLineSegment(sketch, "E772", {"start": v(26.27, -22.24) * mm, "end": v(26.27, -21.87) * mm});
            skLineSegment(sketch, "E773", {"start": v(26.27, -21.87) * mm, "end": v(26.27, -21.5) * mm});
            skLineSegment(sketch, "E774", {"start": v(26.27, -21.5) * mm, "end": v(26.27, -21.14) * mm});
            skLineSegment(sketch, "E775", {"start": v(26.27, -21.14) * mm, "end": v(26.27, -20.77) * mm});
            skLineSegment(sketch, "E776", {"start": v(26.27, -20.77) * mm, "end": v(26.27, -20.4) * mm});
            skLineSegment(sketch, "E777", {"start": v(26.27, -20.4) * mm, "end": v(26.27, -20.04) * mm});
            skLineSegment(sketch, "E778", {"start": v(26.27, -20.04) * mm, "end": v(26.27, -19.67) * mm});
            skLineSegment(sketch, "E779", {"start": v(26.27, -19.67) * mm, "end": v(26.27, -19.3) * mm});
            skLineSegment(sketch, "E780", {"start": v(26.27, -19.3) * mm, "end": v(26.27, -18.94) * mm});
            skLineSegment(sketch, "E781", {"start": v(26.27, -18.94) * mm, "end": v(26.27, -18.57) * mm});
            skLineSegment(sketch, "E782", {"start": v(26.27, -18.57) * mm, "end": v(26.27, -18.2) * mm});
            skLineSegment(sketch, "E783", {"start": v(26.27, -18.2) * mm, "end": v(26.27, -17.84) * mm});
            skLineSegment(sketch, "E784", {"start": v(26.27, -17.84) * mm, "end": v(26.25, -17.45) * mm});
            skLineSegment(sketch, "E785", {"start": v(26.25, -17.45) * mm, "end": v(26.19, -17.08) * mm});
            skLineSegment(sketch, "E786", {"start": v(26.19, -17.08) * mm, "end": v(26.1, -16.71) * mm});
            skLineSegment(sketch, "E787", {"start": v(26.1, -16.71) * mm, "end": v(25.97, -16.36) * mm});
            skLineSegment(sketch, "E788", {"start": v(25.97, -16.36) * mm, "end": v(25.8, -16.03) * mm});
            skLineSegment(sketch, "E789", {"start": v(25.8, -16.03) * mm, "end": v(25.62, -15.72) * mm});
            skLineSegment(sketch, "E790", {"start": v(25.62, -15.72) * mm, "end": v(25.4, -15.43) * mm});
            skLineSegment(sketch, "E791", {"start": v(25.4, -15.43) * mm, "end": v(25.15, -15.16) * mm});
            skLineSegment(sketch, "E792", {"start": v(25.15, -15.16) * mm, "end": v(24.88, -14.91) * mm});
            skLineSegment(sketch, "E793", {"start": v(24.88, -14.91) * mm, "end": v(24.6, -14.7) * mm});
            skLineSegment(sketch, "E794", {"start": v(24.6, -14.7) * mm, "end": v(24.28, -14.5) * mm});
            skLineSegment(sketch, "E795", {"start": v(24.28, -14.5) * mm, "end": v(23.95, -14.35) * mm});
            skLineSegment(sketch, "E796", {"start": v(23.95, -14.35) * mm, "end": v(23.6, -14.22) * mm});
            skLineSegment(sketch, "E797", {"start": v(23.6, -14.22) * mm, "end": v(23.23, -14.12) * mm});
            skLineSegment(sketch, "E798", {"start": v(23.23, -14.12) * mm, "end": v(22.86, -14.07) * mm});
            skLineSegment(sketch, "E799", {"start": v(22.86, -14.07) * mm, "end": v(22.47, -14.05) * mm});
            skLineSegment(sketch, "E800", {"start": v(22.47, -14.05) * mm, "end": v(21.66, -14.05) * mm});
            skLineSegment(sketch, "E801", {"start": v(21.66, -14.05) * mm, "end": v(20.85, -14.05) * mm});
            skLineSegment(sketch, "E802", {"start": v(20.85, -14.05) * mm, "end": v(20.04, -14.05) * mm});
            skLineSegment(sketch, "E803", {"start": v(20.04, -14.05) * mm, "end": v(19.23, -14.05) * mm});
            skLineSegment(sketch, "E804", {"start": v(19.23, -14.05) * mm, "end": v(18.42, -14.05) * mm});
            skLineSegment(sketch, "E805", {"start": v(18.42, -14.05) * mm, "end": v(17.6, -14.05) * mm});
            skLineSegment(sketch, "E806", {"start": v(17.6, -14.05) * mm, "end": v(16.8, -14.05) * mm});
            skLineSegment(sketch, "E807", {"start": v(16.8, -14.05) * mm, "end": v(15.98, -14.05) * mm});
            skLineSegment(sketch, "E808", {"start": v(15.98, -14.05) * mm, "end": v(15.17, -14.05) * mm});
            skLineSegment(sketch, "E809", {"start": v(15.17, -14.05) * mm, "end": v(14.36, -14.05) * mm});
            skLineSegment(sketch, "E810", {"start": v(14.36, -14.05) * mm, "end": v(13.55, -14.05) * mm});
            skLineSegment(sketch, "E811", {"start": v(13.55, -14.05) * mm, "end": v(12.74, -14.05) * mm});
            skLineSegment(sketch, "E812", {"start": v(12.74, -14.05) * mm, "end": v(11.93, -14.05) * mm});
            skLineSegment(sketch, "E813", {"start": v(11.93, -14.05) * mm, "end": v(11.12, -14.05) * mm});
            skLineSegment(sketch, "E814", {"start": v(11.12, -14.05) * mm, "end": v(10.31, -14.05) * mm});
            skLineSegment(sketch, "E815", {"start": v(10.31, -14.05) * mm, "end": v(9.5, -14.05) * mm});
            skLineSegment(sketch, "E816", {"start": v(29.43, -36.75) * mm, "end": v(29.71, -36.75) * mm});
            skLineSegment(sketch, "E817", {"start": v(29.71, -36.75) * mm, "end": v(29.99, -36.75) * mm});
            skLineSegment(sketch, "E818", {"start": v(29.99, -36.75) * mm, "end": v(30.27, -36.75) * mm});
            skLineSegment(sketch, "E819", {"start": v(30.27, -36.75) * mm, "end": v(30.54, -36.75) * mm});
            skLineSegment(sketch, "E820", {"start": v(30.54, -36.75) * mm, "end": v(30.82, -36.75) * mm});
            skLineSegment(sketch, "E821", {"start": v(30.82, -36.75) * mm, "end": v(31.1, -36.75) * mm});
            skLineSegment(sketch, "E822", {"start": v(31.1, -36.75) * mm, "end": v(31.37, -36.75) * mm});
            skLineSegment(sketch, "E823", {"start": v(31.37, -36.75) * mm, "end": v(31.65, -36.75) * mm});
            skLineSegment(sketch, "E824", {"start": v(31.65, -36.75) * mm, "end": v(31.93, -36.75) * mm});
            skLineSegment(sketch, "E825", {"start": v(31.93, -36.75) * mm, "end": v(32.2, -36.75) * mm});
            skLineSegment(sketch, "E826", {"start": v(32.2, -36.75) * mm, "end": v(32.48, -36.75) * mm});
            skLineSegment(sketch, "E827", {"start": v(32.48, -36.75) * mm, "end": v(32.76, -36.75) * mm});
            skLineSegment(sketch, "E828", {"start": v(32.76, -36.75) * mm, "end": v(33.04, -36.75) * mm});
            skLineSegment(sketch, "E829", {"start": v(33.04, -36.75) * mm, "end": v(33.31, -36.75) * mm});
            skLineSegment(sketch, "E830", {"start": v(33.31, -36.75) * mm, "end": v(33.6, -36.75) * mm});
            skLineSegment(sketch, "E831", {"start": v(33.6, -36.75) * mm, "end": v(33.87, -36.75) * mm});
            skLineSegment(sketch, "E832", {"start": v(33.87, -36.75) * mm, "end": v(33.87, -35.33) * mm});
            skLineSegment(sketch, "E833", {"start": v(33.87, -35.33) * mm, "end": v(33.87, -33.91) * mm});
            skLineSegment(sketch, "E834", {"start": v(33.87, -33.91) * mm, "end": v(33.87, -32.5) * mm});
            skLineSegment(sketch, "E835", {"start": v(33.87, -32.5) * mm, "end": v(33.87, -31.07) * mm});
            skLineSegment(sketch, "E836", {"start": v(33.87, -31.07) * mm, "end": v(33.87, -29.65) * mm});
            skLineSegment(sketch, "E837", {"start": v(33.87, -29.65) * mm, "end": v(33.87, -28.24) * mm});
            skLineSegment(sketch, "E838", {"start": v(33.87, -28.24) * mm, "end": v(33.87, -26.82) * mm});
            skLineSegment(sketch, "E839", {"start": v(33.87, -26.82) * mm, "end": v(33.87, -25.4) * mm});
            skLineSegment(sketch, "E840", {"start": v(33.87, -25.4) * mm, "end": v(33.87, -23.98) * mm});
            skLineSegment(sketch, "E841", {"start": v(33.87, -23.98) * mm, "end": v(33.87, -22.56) * mm});
            skLineSegment(sketch, "E842", {"start": v(33.87, -22.56) * mm, "end": v(33.87, -21.14) * mm});
            skLineSegment(sketch, "E843", {"start": v(33.87, -21.14) * mm, "end": v(33.87, -19.72) * mm});
            skLineSegment(sketch, "E844", {"start": v(33.87, -19.72) * mm, "end": v(33.87, -18.3) * mm});
            skLineSegment(sketch, "E845", {"start": v(33.87, -18.3) * mm, "end": v(33.87, -16.88) * mm});
            skLineSegment(sketch, "E846", {"start": v(33.87, -16.88) * mm, "end": v(33.87, -15.47) * mm});
            skLineSegment(sketch, "E847", {"start": v(33.87, -15.47) * mm, "end": v(33.87, -14.05) * mm});
            skLineSegment(sketch, "E848", {"start": v(33.87, -14.05) * mm, "end": v(33.6, -14.05) * mm});
            skLineSegment(sketch, "E849", {"start": v(33.6, -14.05) * mm, "end": v(33.31, -14.05) * mm});
            skLineSegment(sketch, "E850", {"start": v(33.31, -14.05) * mm, "end": v(33.04, -14.05) * mm});
            skLineSegment(sketch, "E851", {"start": v(33.04, -14.05) * mm, "end": v(32.76, -14.05) * mm});
            skLineSegment(sketch, "E852", {"start": v(32.76, -14.05) * mm, "end": v(32.48, -14.05) * mm});
            skLineSegment(sketch, "E853", {"start": v(32.48, -14.05) * mm, "end": v(32.2, -14.05) * mm});
            skLineSegment(sketch, "E854", {"start": v(32.2, -14.05) * mm, "end": v(31.93, -14.05) * mm});
            skLineSegment(sketch, "E855", {"start": v(31.93, -14.05) * mm, "end": v(31.65, -14.05) * mm});
            skLineSegment(sketch, "E856", {"start": v(31.65, -14.05) * mm, "end": v(31.37, -14.05) * mm});
            skLineSegment(sketch, "E857", {"start": v(31.37, -14.05) * mm, "end": v(31.1, -14.05) * mm});
            skLineSegment(sketch, "E858", {"start": v(31.1, -14.05) * mm, "end": v(30.82, -14.05) * mm});
            skLineSegment(sketch, "E859", {"start": v(30.82, -14.05) * mm, "end": v(30.54, -14.05) * mm});
            skLineSegment(sketch, "E860", {"start": v(30.54, -14.05) * mm, "end": v(30.27, -14.05) * mm});
            skLineSegment(sketch, "E861", {"start": v(30.27, -14.05) * mm, "end": v(29.99, -14.05) * mm});
            skLineSegment(sketch, "E862", {"start": v(29.99, -14.05) * mm, "end": v(29.71, -14.05) * mm});
            skLineSegment(sketch, "E863", {"start": v(29.71, -14.05) * mm, "end": v(29.43, -14.05) * mm});
            skLineSegment(sketch, "E864", {"start": v(29.43, -14.05) * mm, "end": v(29.43, -15.47) * mm});
            skLineSegment(sketch, "E865", {"start": v(29.43, -15.47) * mm, "end": v(29.43, -16.88) * mm});
            skLineSegment(sketch, "E866", {"start": v(29.43, -16.88) * mm, "end": v(29.43, -18.3) * mm});
            skLineSegment(sketch, "E867", {"start": v(29.43, -18.3) * mm, "end": v(29.43, -19.72) * mm});
            skLineSegment(sketch, "E868", {"start": v(29.43, -19.72) * mm, "end": v(29.43, -21.14) * mm});
            skLineSegment(sketch, "E869", {"start": v(29.43, -21.14) * mm, "end": v(29.43, -22.56) * mm});
            skLineSegment(sketch, "E870", {"start": v(29.43, -22.56) * mm, "end": v(29.43, -23.98) * mm});
            skLineSegment(sketch, "E871", {"start": v(29.43, -23.98) * mm, "end": v(29.43, -25.4) * mm});
            skLineSegment(sketch, "E872", {"start": v(29.43, -25.4) * mm, "end": v(29.43, -26.82) * mm});
            skLineSegment(sketch, "E873", {"start": v(29.43, -26.82) * mm, "end": v(29.43, -28.24) * mm});
            skLineSegment(sketch, "E874", {"start": v(29.43, -28.24) * mm, "end": v(29.43, -29.65) * mm});
            skLineSegment(sketch, "E875", {"start": v(29.43, -29.65) * mm, "end": v(29.43, -31.07) * mm});
            skLineSegment(sketch, "E876", {"start": v(29.43, -31.07) * mm, "end": v(29.43, -32.5) * mm});
            skLineSegment(sketch, "E877", {"start": v(29.43, -32.5) * mm, "end": v(29.43, -33.91) * mm});
            skLineSegment(sketch, "E878", {"start": v(29.43, -33.91) * mm, "end": v(29.43, -35.33) * mm});
            skLineSegment(sketch, "E879", {"start": v(29.43, -35.33) * mm, "end": v(29.43, -36.75) * mm});
            skLineSegment(sketch, "E880", {"start": v(42.27, -31.59) * mm, "end": v(42.27, -30.82) * mm});
            skLineSegment(sketch, "E881", {"start": v(42.27, -30.82) * mm, "end": v(42.27, -30.05) * mm});
            skLineSegment(sketch, "E882", {"start": v(42.27, -30.05) * mm, "end": v(42.27, -29.27) * mm});
            skLineSegment(sketch, "E883", {"start": v(42.27, -29.27) * mm, "end": v(42.27, -28.5) * mm});
            skLineSegment(sketch, "E884", {"start": v(42.27, -28.5) * mm, "end": v(42.27, -27.73) * mm});
            skLineSegment(sketch, "E885", {"start": v(42.27, -27.73) * mm, "end": v(42.27, -26.96) * mm});
            skLineSegment(sketch, "E886", {"start": v(42.27, -26.96) * mm, "end": v(42.27, -26.19) * mm});
            skLineSegment(sketch, "E887", {"start": v(42.27, -26.19) * mm, "end": v(42.27, -25.41) * mm});
            skLineSegment(sketch, "E888", {"start": v(42.27, -25.41) * mm, "end": v(42.27, -24.64) * mm});
            skLineSegment(sketch, "E889", {"start": v(42.27, -24.64) * mm, "end": v(42.27, -23.87) * mm});
            skLineSegment(sketch, "E890", {"start": v(42.27, -23.87) * mm, "end": v(42.27, -23.1) * mm});
            skLineSegment(sketch, "E891", {"start": v(42.27, -23.1) * mm, "end": v(42.27, -22.33) * mm});
            skLineSegment(sketch, "E892", {"start": v(42.27, -22.33) * mm, "end": v(42.27, -21.55) * mm});
            skLineSegment(sketch, "E893", {"start": v(42.27, -21.55) * mm, "end": v(42.27, -20.78) * mm});
            skLineSegment(sketch, "E894", {"start": v(42.27, -20.78) * mm, "end": v(42.27, -20.01) * mm});
            skLineSegment(sketch, "E895", {"start": v(42.27, -20.01) * mm, "end": v(42.27, -19.24) * mm});
            skLineSegment(sketch, "E896", {"start": v(42.27, -19.24) * mm, "end": v(42.27, -19.12) * mm});
            skLineSegment(sketch, "E897", {"start": v(42.27, -19.12) * mm, "end": v(42.29, -19) * mm});
            skLineSegment(sketch, "E898", {"start": v(42.29, -19) * mm, "end": v(42.32, -18.9) * mm});
            skLineSegment(sketch, "E899", {"start": v(42.32, -18.9) * mm, "end": v(42.35, -18.8) * mm});
            skLineSegment(sketch, "E900", {"start": v(42.35, -18.8) * mm, "end": v(42.4, -18.69) * mm});
            skLineSegment(sketch, "E901", {"start": v(42.4, -18.69) * mm, "end": v(42.46, -18.6) * mm});
            skLineSegment(sketch, "E902", {"start": v(42.46, -18.6) * mm, "end": v(42.52, -18.5) * mm});
            skLineSegment(sketch, "E903", {"start": v(42.52, -18.5) * mm, "end": v(42.6, -18.42) * mm});
            skLineSegment(sketch, "E904", {"start": v(42.6, -18.42) * mm, "end": v(42.68, -18.34) * mm});
            skLineSegment(sketch, "E905", {"start": v(42.68, -18.34) * mm, "end": v(42.76, -18.28) * mm});
            skLineSegment(sketch, "E906", {"start": v(42.76, -18.28) * mm, "end": v(42.86, -18.22) * mm});
            skLineSegment(sketch, "E907", {"start": v(42.86, -18.22) * mm, "end": v(42.96, -18.17) * mm});
            skLineSegment(sketch, "E908", {"start": v(42.96, -18.17) * mm, "end": v(43.06, -18.13) * mm});
            skLineSegment(sketch, "E909", {"start": v(43.06, -18.13) * mm, "end": v(43.17, -18.1) * mm});
            skLineSegment(sketch, "E910", {"start": v(43.17, -18.1) * mm, "end": v(43.28, -18.08) * mm});
            skLineSegment(sketch, "E911", {"start": v(43.28, -18.08) * mm, "end": v(43.4, -18.07) * mm});
            skLineSegment(sketch, "E912", {"start": v(43.4, -18.07) * mm, "end": v(43.9, -18.07) * mm});
            skLineSegment(sketch, "E913", {"start": v(43.9, -18.07) * mm, "end": v(44.38, -18.07) * mm});
            skLineSegment(sketch, "E914", {"start": v(44.38, -18.07) * mm, "end": v(44.88, -18.07) * mm});
            skLineSegment(sketch, "E915", {"start": v(44.88, -18.07) * mm, "end": v(45.37, -18.07) * mm});
            skLineSegment(sketch, "E916", {"start": v(45.37, -18.07) * mm, "end": v(45.86, -18.07) * mm});
            skLineSegment(sketch, "E917", {"start": v(45.86, -18.07) * mm, "end": v(46.35, -18.07) * mm});
            skLineSegment(sketch, "E918", {"start": v(46.35, -18.07) * mm, "end": v(46.84, -18.07) * mm});
            skLineSegment(sketch, "E919", {"start": v(46.84, -18.07) * mm, "end": v(47.33, -18.07) * mm});
            skLineSegment(sketch, "E920", {"start": v(47.33, -18.07) * mm, "end": v(47.82, -18.07) * mm});
            skLineSegment(sketch, "E921", {"start": v(47.82, -18.07) * mm, "end": v(48.32, -18.07) * mm});
            skLineSegment(sketch, "E922", {"start": v(48.32, -18.07) * mm, "end": v(48.8, -18.07) * mm});
            skLineSegment(sketch, "E923", {"start": v(48.8, -18.07) * mm, "end": v(49.3, -18.07) * mm});
            skLineSegment(sketch, "E924", {"start": v(49.3, -18.07) * mm, "end": v(49.8, -18.07) * mm});
            skLineSegment(sketch, "E925", {"start": v(49.8, -18.07) * mm, "end": v(50.28, -18.07) * mm});
            skLineSegment(sketch, "E926", {"start": v(50.28, -18.07) * mm, "end": v(50.77, -18.07) * mm});
            skLineSegment(sketch, "E927", {"start": v(50.77, -18.07) * mm, "end": v(51.27, -18.07) * mm});
            skLineSegment(sketch, "E928", {"start": v(51.27, -18.07) * mm, "end": v(51.38, -18.08) * mm});
            skLineSegment(sketch, "E929", {"start": v(51.38, -18.08) * mm, "end": v(51.5, -18.1) * mm});
            skLineSegment(sketch, "E930", {"start": v(51.5, -18.1) * mm, "end": v(51.6, -18.13) * mm});
            skLineSegment(sketch, "E931", {"start": v(51.6, -18.13) * mm, "end": v(51.71, -18.17) * mm});
            skLineSegment(sketch, "E932", {"start": v(51.71, -18.17) * mm, "end": v(51.81, -18.22) * mm});
            skLineSegment(sketch, "E933", {"start": v(51.81, -18.22) * mm, "end": v(51.9, -18.28) * mm});
            skLineSegment(sketch, "E934", {"start": v(51.9, -18.28) * mm, "end": v(52, -18.34) * mm});
            skLineSegment(sketch, "E935", {"start": v(52, -18.34) * mm, "end": v(52.07, -18.42) * mm});
            skLineSegment(sketch, "E936", {"start": v(52.07, -18.42) * mm, "end": v(52.14, -18.5) * mm});
            skLineSegment(sketch, "E937", {"start": v(52.14, -18.5) * mm, "end": v(52.2, -18.6) * mm});
            skLineSegment(sketch, "E938", {"start": v(52.2, -18.6) * mm, "end": v(52.26, -18.69) * mm});
            skLineSegment(sketch, "E939", {"start": v(52.26, -18.69) * mm, "end": v(52.31, -18.8) * mm});
            skLineSegment(sketch, "E940", {"start": v(52.31, -18.8) * mm, "end": v(52.35, -18.9) * mm});
            skLineSegment(sketch, "E941", {"start": v(52.35, -18.9) * mm, "end": v(52.38, -19) * mm});
            skLineSegment(sketch, "E942", {"start": v(52.38, -19) * mm, "end": v(52.4, -19.12) * mm});
            skLineSegment(sketch, "E943", {"start": v(52.4, -19.12) * mm, "end": v(52.4, -19.24) * mm});
            skLineSegment(sketch, "E944", {"start": v(52.4, -19.24) * mm, "end": v(52.4, -20.01) * mm});
            skLineSegment(sketch, "E945", {"start": v(52.4, -20.01) * mm, "end": v(52.4, -20.78) * mm});
            skLineSegment(sketch, "E946", {"start": v(52.4, -20.78) * mm, "end": v(52.4, -21.55) * mm});
            skLineSegment(sketch, "E947", {"start": v(52.4, -21.55) * mm, "end": v(52.4, -22.33) * mm});
            skLineSegment(sketch, "E948", {"start": v(52.4, -22.33) * mm, "end": v(52.4, -23.1) * mm});
            skLineSegment(sketch, "E949", {"start": v(52.4, -23.1) * mm, "end": v(52.4, -23.87) * mm});
            skLineSegment(sketch, "E950", {"start": v(52.4, -23.87) * mm, "end": v(52.4, -24.64) * mm});
            skLineSegment(sketch, "E951", {"start": v(52.4, -24.64) * mm, "end": v(52.4, -25.41) * mm});
            skLineSegment(sketch, "E952", {"start": v(52.4, -25.41) * mm, "end": v(52.4, -26.19) * mm});
            skLineSegment(sketch, "E953", {"start": v(52.4, -26.19) * mm, "end": v(52.4, -26.96) * mm});
            skLineSegment(sketch, "E954", {"start": v(52.4, -26.96) * mm, "end": v(52.4, -27.73) * mm});
            skLineSegment(sketch, "E955", {"start": v(52.4, -27.73) * mm, "end": v(52.4, -28.5) * mm});
            skLineSegment(sketch, "E956", {"start": v(52.4, -28.5) * mm, "end": v(52.4, -29.27) * mm});
            skLineSegment(sketch, "E957", {"start": v(52.4, -29.27) * mm, "end": v(52.4, -30.05) * mm});
            skLineSegment(sketch, "E958", {"start": v(52.4, -30.05) * mm, "end": v(52.4, -30.82) * mm});
            skLineSegment(sketch, "E959", {"start": v(52.4, -30.82) * mm, "end": v(52.4, -31.59) * mm});
            skLineSegment(sketch, "E960", {"start": v(52.4, -31.59) * mm, "end": v(52.4, -31.7) * mm});
            skLineSegment(sketch, "E961", {"start": v(52.4, -31.7) * mm, "end": v(52.38, -31.82) * mm});
            skLineSegment(sketch, "E962", {"start": v(52.38, -31.82) * mm, "end": v(52.35, -31.93) * mm});
            skLineSegment(sketch, "E963", {"start": v(52.35, -31.93) * mm, "end": v(52.31, -32.03) * mm});
            skLineSegment(sketch, "E964", {"start": v(52.31, -32.03) * mm, "end": v(52.26, -32.13) * mm});
            skLineSegment(sketch, "E965", {"start": v(52.26, -32.13) * mm, "end": v(52.2, -32.23) * mm});
            skLineSegment(sketch, "E966", {"start": v(52.2, -32.23) * mm, "end": v(52.14, -32.31) * mm});
            skLineSegment(sketch, "E967", {"start": v(52.14, -32.31) * mm, "end": v(52.07, -32.4) * mm});
            skLineSegment(sketch, "E968", {"start": v(52.07, -32.4) * mm, "end": v(52, -32.47) * mm});
            skLineSegment(sketch, "E969", {"start": v(52, -32.47) * mm, "end": v(51.9, -32.53) * mm});
            skLineSegment(sketch, "E970", {"start": v(51.9, -32.53) * mm, "end": v(51.81, -32.59) * mm});
            skLineSegment(sketch, "E971", {"start": v(51.81, -32.59) * mm, "end": v(51.71, -32.63) * mm});
            skLineSegment(sketch, "E972", {"start": v(51.71, -32.63) * mm, "end": v(51.6, -32.67) * mm});
            skLineSegment(sketch, "E973", {"start": v(51.6, -32.67) * mm, "end": v(51.5, -32.7) * mm});
            skLineSegment(sketch, "E974", {"start": v(51.5, -32.7) * mm, "end": v(51.38, -32.72) * mm});
            skLineSegment(sketch, "E975", {"start": v(51.38, -32.72) * mm, "end": v(51.27, -32.72) * mm});
            skLineSegment(sketch, "E976", {"start": v(51.27, -32.72) * mm, "end": v(50.77, -32.72) * mm});
            skLineSegment(sketch, "E977", {"start": v(50.77, -32.72) * mm, "end": v(50.28, -32.72) * mm});
            skLineSegment(sketch, "E978", {"start": v(50.28, -32.72) * mm, "end": v(49.8, -32.72) * mm});
            skLineSegment(sketch, "E979", {"start": v(49.8, -32.72) * mm, "end": v(49.3, -32.72) * mm});
            skLineSegment(sketch, "E980", {"start": v(49.3, -32.72) * mm, "end": v(48.8, -32.72) * mm});
            skLineSegment(sketch, "E981", {"start": v(48.8, -32.72) * mm, "end": v(48.32, -32.72) * mm});
            skLineSegment(sketch, "E982", {"start": v(48.32, -32.72) * mm, "end": v(47.82, -32.72) * mm});
            skLineSegment(sketch, "E983", {"start": v(47.82, -32.72) * mm, "end": v(47.33, -32.72) * mm});
            skLineSegment(sketch, "E984", {"start": v(47.33, -32.72) * mm, "end": v(46.84, -32.72) * mm});
            skLineSegment(sketch, "E985", {"start": v(46.84, -32.72) * mm, "end": v(46.35, -32.72) * mm});
            skLineSegment(sketch, "E986", {"start": v(46.35, -32.72) * mm, "end": v(45.86, -32.72) * mm});
            skLineSegment(sketch, "E987", {"start": v(45.86, -32.72) * mm, "end": v(45.37, -32.72) * mm});
            skLineSegment(sketch, "E988", {"start": v(45.37, -32.72) * mm, "end": v(44.88, -32.72) * mm});
            skLineSegment(sketch, "E989", {"start": v(44.88, -32.72) * mm, "end": v(44.38, -32.72) * mm});
            skLineSegment(sketch, "E990", {"start": v(44.38, -32.72) * mm, "end": v(43.9, -32.72) * mm});
            skLineSegment(sketch, "E991", {"start": v(43.9, -32.72) * mm, "end": v(43.4, -32.72) * mm});
            skLineSegment(sketch, "E992", {"start": v(43.4, -32.72) * mm, "end": v(43.28, -32.72) * mm});
            skLineSegment(sketch, "E993", {"start": v(43.28, -32.72) * mm, "end": v(43.17, -32.7) * mm});
            skLineSegment(sketch, "E994", {"start": v(43.17, -32.7) * mm, "end": v(43.06, -32.67) * mm});
            skLineSegment(sketch, "E995", {"start": v(43.06, -32.67) * mm, "end": v(42.96, -32.63) * mm});
            skLineSegment(sketch, "E996", {"start": v(42.96, -32.63) * mm, "end": v(42.86, -32.59) * mm});
            skLineSegment(sketch, "E997", {"start": v(42.86, -32.59) * mm, "end": v(42.76, -32.53) * mm});
            skLineSegment(sketch, "E998", {"start": v(42.76, -32.53) * mm, "end": v(42.68, -32.47) * mm});
            skLineSegment(sketch, "E999", {"start": v(42.68, -32.47) * mm, "end": v(42.6, -32.4) * mm});
            skLineSegment(sketch, "E1000", {"start": v(42.6, -32.4) * mm, "end": v(42.52, -32.31) * mm});
            skLineSegment(sketch, "E1001", {"start": v(42.52, -32.31) * mm, "end": v(42.46, -32.23) * mm});
            skLineSegment(sketch, "E1002", {"start": v(42.46, -32.23) * mm, "end": v(42.4, -32.13) * mm});
            skLineSegment(sketch, "E1003", {"start": v(42.4, -32.13) * mm, "end": v(42.35, -32.03) * mm});
            skLineSegment(sketch, "E1004", {"start": v(42.35, -32.03) * mm, "end": v(42.32, -31.93) * mm});
            skLineSegment(sketch, "E1005", {"start": v(42.32, -31.93) * mm, "end": v(42.29, -31.82) * mm});
            skLineSegment(sketch, "E1006", {"start": v(42.29, -31.82) * mm, "end": v(42.27, -31.7) * mm});
            skLineSegment(sketch, "E1007", {"start": v(42.27, -31.7) * mm, "end": v(42.27, -31.59) * mm});
            skLineSegment(sketch, "E1008", {"start": v(41.63, -14.05) * mm, "end": v(41.25, -14.07) * mm});
            skLineSegment(sketch, "E1009", {"start": v(41.25, -14.07) * mm, "end": v(40.88, -14.12) * mm});
            skLineSegment(sketch, "E1010", {"start": v(40.88, -14.12) * mm, "end": v(40.52, -14.22) * mm});
            skLineSegment(sketch, "E1011", {"start": v(40.52, -14.22) * mm, "end": v(40.17, -14.35) * mm});
            skLineSegment(sketch, "E1012", {"start": v(40.17, -14.35) * mm, "end": v(39.84, -14.5) * mm});
            skLineSegment(sketch, "E1013", {"start": v(39.84, -14.5) * mm, "end": v(39.53, -14.7) * mm});
            skLineSegment(sketch, "E1014", {"start": v(39.53, -14.7) * mm, "end": v(39.24, -14.91) * mm});
            skLineSegment(sketch, "E1015", {"start": v(39.24, -14.91) * mm, "end": v(38.98, -15.16) * mm});
            skLineSegment(sketch, "E1016", {"start": v(38.98, -15.16) * mm, "end": v(38.73, -15.43) * mm});
            skLineSegment(sketch, "E1017", {"start": v(38.73, -15.43) * mm, "end": v(38.51, -15.72) * mm});
            skLineSegment(sketch, "E1018", {"start": v(38.51, -15.72) * mm, "end": v(38.32, -16.03) * mm});
            skLineSegment(sketch, "E1019", {"start": v(38.32, -16.03) * mm, "end": v(38.16, -16.36) * mm});
            skLineSegment(sketch, "E1020", {"start": v(38.16, -16.36) * mm, "end": v(38.04, -16.71) * mm});
            skLineSegment(sketch, "E1021", {"start": v(38.04, -16.71) * mm, "end": v(37.94, -17.08) * mm});
            skLineSegment(sketch, "E1022", {"start": v(37.94, -17.08) * mm, "end": v(37.89, -17.45) * mm});
            skLineSegment(sketch, "E1023", {"start": v(37.89, -17.45) * mm, "end": v(37.87, -17.84) * mm});
            skLineSegment(sketch, "E1024", {"start": v(37.87, -17.84) * mm, "end": v(37.87, -18.79) * mm});
            skLineSegment(sketch, "E1025", {"start": v(37.87, -18.79) * mm, "end": v(37.87, -19.73) * mm});
            skLineSegment(sketch, "E1026", {"start": v(37.87, -19.73) * mm, "end": v(37.87, -20.68) * mm});
            skLineSegment(sketch, "E1027", {"start": v(37.87, -20.68) * mm, "end": v(37.87, -21.63) * mm});
            skLineSegment(sketch, "E1028", {"start": v(37.87, -21.63) * mm, "end": v(37.87, -22.57) * mm});
            skLineSegment(sketch, "E1029", {"start": v(37.87, -22.57) * mm, "end": v(37.87, -23.52) * mm});
            skLineSegment(sketch, "E1030", {"start": v(37.87, -23.52) * mm, "end": v(37.87, -24.47) * mm});
            skLineSegment(sketch, "E1031", {"start": v(37.87, -24.47) * mm, "end": v(37.87, -25.41) * mm});
            skLineSegment(sketch, "E1032", {"start": v(37.87, -25.41) * mm, "end": v(37.87, -26.36) * mm});
            skLineSegment(sketch, "E1033", {"start": v(37.87, -26.36) * mm, "end": v(37.87, -27.3) * mm});
            skLineSegment(sketch, "E1034", {"start": v(37.87, -27.3) * mm, "end": v(37.87, -28.25) * mm});
            skLineSegment(sketch, "E1035", {"start": v(37.87, -28.25) * mm, "end": v(37.87, -29.2) * mm});
            skLineSegment(sketch, "E1036", {"start": v(37.87, -29.2) * mm, "end": v(37.87, -30.15) * mm});
            skLineSegment(sketch, "E1037", {"start": v(37.87, -30.15) * mm, "end": v(37.87, -31.1) * mm});
            skLineSegment(sketch, "E1038", {"start": v(37.87, -31.1) * mm, "end": v(37.87, -32.04) * mm});
            skLineSegment(sketch, "E1039", {"start": v(37.87, -32.04) * mm, "end": v(37.87, -32.99) * mm});
            skLineSegment(sketch, "E1040", {"start": v(37.87, -32.99) * mm, "end": v(37.89, -33.38) * mm});
            skLineSegment(sketch, "E1041", {"start": v(37.89, -33.38) * mm, "end": v(37.94, -33.75) * mm});
            skLineSegment(sketch, "E1042", {"start": v(37.94, -33.75) * mm, "end": v(38.04, -34.11) * mm});
            skLineSegment(sketch, "E1043", {"start": v(38.04, -34.11) * mm, "end": v(38.16, -34.46) * mm});
            skLineSegment(sketch, "E1044", {"start": v(38.16, -34.46) * mm, "end": v(38.32, -34.79) * mm});
            skLineSegment(sketch, "E1045", {"start": v(38.32, -34.79) * mm, "end": v(38.51, -35.1) * mm});
            skLineSegment(sketch, "E1046", {"start": v(38.51, -35.1) * mm, "end": v(38.73, -35.39) * mm});
            skLineSegment(sketch, "E1047", {"start": v(38.73, -35.39) * mm, "end": v(38.98, -35.65) * mm});
            skLineSegment(sketch, "E1048", {"start": v(38.98, -35.65) * mm, "end": v(39.24, -35.9) * mm});
            skLineSegment(sketch, "E1049", {"start": v(39.24, -35.9) * mm, "end": v(39.53, -36.11) * mm});
            skLineSegment(sketch, "E1050", {"start": v(39.53, -36.11) * mm, "end": v(39.84, -36.3) * mm});
            skLineSegment(sketch, "E1051", {"start": v(39.84, -36.3) * mm, "end": v(40.17, -36.46) * mm});
            skLineSegment(sketch, "E1052", {"start": v(40.17, -36.46) * mm, "end": v(40.52, -36.58) * mm});
            skLineSegment(sketch, "E1053", {"start": v(40.52, -36.58) * mm, "end": v(40.88, -36.67) * mm});
            skLineSegment(sketch, "E1054", {"start": v(40.88, -36.67) * mm, "end": v(41.25, -36.73) * mm});
            skLineSegment(sketch, "E1055", {"start": v(41.25, -36.73) * mm, "end": v(41.63, -36.75) * mm});
            skLineSegment(sketch, "E1056", {"start": v(41.63, -36.75) * mm, "end": v(42.35, -36.75) * mm});
            skLineSegment(sketch, "E1057", {"start": v(42.35, -36.75) * mm, "end": v(43.06, -36.75) * mm});
            skLineSegment(sketch, "E1058", {"start": v(43.06, -36.75) * mm, "end": v(43.77, -36.75) * mm});
            skLineSegment(sketch, "E1059", {"start": v(43.77, -36.75) * mm, "end": v(44.48, -36.75) * mm});
            skLineSegment(sketch, "E1060", {"start": v(44.48, -36.75) * mm, "end": v(45.2, -36.75) * mm});
            skLineSegment(sketch, "E1061", {"start": v(45.2, -36.75) * mm, "end": v(45.9, -36.75) * mm});
            skLineSegment(sketch, "E1062", {"start": v(45.9, -36.75) * mm, "end": v(46.62, -36.75) * mm});
            skLineSegment(sketch, "E1063", {"start": v(46.62, -36.75) * mm, "end": v(47.33, -36.75) * mm});
            skLineSegment(sketch, "E1064", {"start": v(47.33, -36.75) * mm, "end": v(48.05, -36.75) * mm});
            skLineSegment(sketch, "E1065", {"start": v(48.05, -36.75) * mm, "end": v(48.76, -36.75) * mm});
            skLineSegment(sketch, "E1066", {"start": v(48.76, -36.75) * mm, "end": v(49.47, -36.75) * mm});
            skLineSegment(sketch, "E1067", {"start": v(49.47, -36.75) * mm, "end": v(50.18, -36.75) * mm});
            skLineSegment(sketch, "E1068", {"start": v(50.18, -36.75) * mm, "end": v(50.9, -36.75) * mm});
            skLineSegment(sketch, "E1069", {"start": v(50.9, -36.75) * mm, "end": v(51.6, -36.75) * mm});
            skLineSegment(sketch, "E1070", {"start": v(51.6, -36.75) * mm, "end": v(52.32, -36.75) * mm});
            skLineSegment(sketch, "E1071", {"start": v(52.32, -36.75) * mm, "end": v(53.03, -36.75) * mm});
            skLineSegment(sketch, "E1072", {"start": v(53.03, -36.75) * mm, "end": v(53.42, -36.73) * mm});
            skLineSegment(sketch, "E1073", {"start": v(53.42, -36.73) * mm, "end": v(53.79, -36.67) * mm});
            skLineSegment(sketch, "E1074", {"start": v(53.79, -36.67) * mm, "end": v(54.15, -36.58) * mm});
            skLineSegment(sketch, "E1075", {"start": v(54.15, -36.58) * mm, "end": v(54.5, -36.46) * mm});
            skLineSegment(sketch, "E1076", {"start": v(54.5, -36.46) * mm, "end": v(54.82, -36.3) * mm});
            skLineSegment(sketch, "E1077", {"start": v(54.82, -36.3) * mm, "end": v(55.13, -36.11) * mm});
            skLineSegment(sketch, "E1078", {"start": v(55.13, -36.11) * mm, "end": v(55.42, -35.9) * mm});
            skLineSegment(sketch, "E1079", {"start": v(55.42, -35.9) * mm, "end": v(55.7, -35.65) * mm});
            skLineSegment(sketch, "E1080", {"start": v(55.7, -35.65) * mm, "end": v(55.93, -35.39) * mm});
            skLineSegment(sketch, "E1081", {"start": v(55.93, -35.39) * mm, "end": v(56.15, -35.1) * mm});
            skLineSegment(sketch, "E1082", {"start": v(56.15, -35.1) * mm, "end": v(56.34, -34.79) * mm});
            skLineSegment(sketch, "E1083", {"start": v(56.34, -34.79) * mm, "end": v(56.5, -34.46) * mm});
            skLineSegment(sketch, "E1084", {"start": v(56.5, -34.46) * mm, "end": v(56.63, -34.11) * mm});
            skLineSegment(sketch, "E1085", {"start": v(56.63, -34.11) * mm, "end": v(56.72, -33.75) * mm});
            skLineSegment(sketch, "E1086", {"start": v(56.72, -33.75) * mm, "end": v(56.78, -33.38) * mm});
            skLineSegment(sketch, "E1087", {"start": v(56.78, -33.38) * mm, "end": v(56.8, -32.99) * mm});
            skLineSegment(sketch, "E1088", {"start": v(56.8, -32.99) * mm, "end": v(56.8, -32.04) * mm});
            skLineSegment(sketch, "E1089", {"start": v(56.8, -32.04) * mm, "end": v(56.8, -31.1) * mm});
            skLineSegment(sketch, "E1090", {"start": v(56.8, -31.1) * mm, "end": v(56.8, -30.15) * mm});
            skLineSegment(sketch, "E1091", {"start": v(56.8, -30.15) * mm, "end": v(56.8, -29.2) * mm});
            skLineSegment(sketch, "E1092", {"start": v(56.8, -29.2) * mm, "end": v(56.8, -28.25) * mm});
            skLineSegment(sketch, "E1093", {"start": v(56.8, -28.25) * mm, "end": v(56.8, -27.3) * mm});
            skLineSegment(sketch, "E1094", {"start": v(56.8, -27.3) * mm, "end": v(56.8, -26.36) * mm});
            skLineSegment(sketch, "E1095", {"start": v(56.8, -26.36) * mm, "end": v(56.8, -25.41) * mm});
            skLineSegment(sketch, "E1096", {"start": v(56.8, -25.41) * mm, "end": v(56.8, -24.47) * mm});
            skLineSegment(sketch, "E1097", {"start": v(56.8, -24.47) * mm, "end": v(56.8, -23.52) * mm});
            skLineSegment(sketch, "E1098", {"start": v(56.8, -23.52) * mm, "end": v(56.8, -22.57) * mm});
            skLineSegment(sketch, "E1099", {"start": v(56.8, -22.57) * mm, "end": v(56.8, -21.63) * mm});
            skLineSegment(sketch, "E1100", {"start": v(56.8, -21.63) * mm, "end": v(56.8, -20.68) * mm});
            skLineSegment(sketch, "E1101", {"start": v(56.8, -20.68) * mm, "end": v(56.8, -19.73) * mm});
            skLineSegment(sketch, "E1102", {"start": v(56.8, -19.73) * mm, "end": v(56.8, -18.79) * mm});
            skLineSegment(sketch, "E1103", {"start": v(56.8, -18.79) * mm, "end": v(56.8, -17.84) * mm});
            skLineSegment(sketch, "E1104", {"start": v(56.8, -17.84) * mm, "end": v(56.78, -17.45) * mm});
            skLineSegment(sketch, "E1105", {"start": v(56.78, -17.45) * mm, "end": v(56.72, -17.08) * mm});
            skLineSegment(sketch, "E1106", {"start": v(56.72, -17.08) * mm, "end": v(56.63, -16.71) * mm});
            skLineSegment(sketch, "E1107", {"start": v(56.63, -16.71) * mm, "end": v(56.5, -16.36) * mm});
            skLineSegment(sketch, "E1108", {"start": v(56.5, -16.36) * mm, "end": v(56.34, -16.03) * mm});
            skLineSegment(sketch, "E1109", {"start": v(56.34, -16.03) * mm, "end": v(56.15, -15.72) * mm});
            skLineSegment(sketch, "E1110", {"start": v(56.15, -15.72) * mm, "end": v(55.93, -15.43) * mm});
            skLineSegment(sketch, "E1111", {"start": v(55.93, -15.43) * mm, "end": v(55.7, -15.16) * mm});
            skLineSegment(sketch, "E1112", {"start": v(55.7, -15.16) * mm, "end": v(55.42, -14.91) * mm});
            skLineSegment(sketch, "E1113", {"start": v(55.42, -14.91) * mm, "end": v(55.13, -14.7) * mm});
            skLineSegment(sketch, "E1114", {"start": v(55.13, -14.7) * mm, "end": v(54.82, -14.5) * mm});
            skLineSegment(sketch, "E1115", {"start": v(54.82, -14.5) * mm, "end": v(54.5, -14.35) * mm});
            skLineSegment(sketch, "E1116", {"start": v(54.5, -14.35) * mm, "end": v(54.15, -14.22) * mm});
            skLineSegment(sketch, "E1117", {"start": v(54.15, -14.22) * mm, "end": v(53.79, -14.12) * mm});
            skLineSegment(sketch, "E1118", {"start": v(53.79, -14.12) * mm, "end": v(53.42, -14.07) * mm});
            skLineSegment(sketch, "E1119", {"start": v(53.42, -14.07) * mm, "end": v(53.03, -14.05) * mm});
            skLineSegment(sketch, "E1120", {"start": v(53.03, -14.05) * mm, "end": v(52.32, -14.05) * mm});
            skLineSegment(sketch, "E1121", {"start": v(52.32, -14.05) * mm, "end": v(51.6, -14.05) * mm});
            skLineSegment(sketch, "E1122", {"start": v(51.6, -14.05) * mm, "end": v(50.9, -14.05) * mm});
            skLineSegment(sketch, "E1123", {"start": v(50.9, -14.05) * mm, "end": v(50.18, -14.05) * mm});
            skLineSegment(sketch, "E1124", {"start": v(50.18, -14.05) * mm, "end": v(49.47, -14.05) * mm});
            skLineSegment(sketch, "E1125", {"start": v(49.47, -14.05) * mm, "end": v(48.76, -14.05) * mm});
            skLineSegment(sketch, "E1126", {"start": v(48.76, -14.05) * mm, "end": v(48.05, -14.05) * mm});
            skLineSegment(sketch, "E1127", {"start": v(48.05, -14.05) * mm, "end": v(47.33, -14.05) * mm});
            skLineSegment(sketch, "E1128", {"start": v(47.33, -14.05) * mm, "end": v(46.62, -14.05) * mm});
            skLineSegment(sketch, "E1129", {"start": v(46.62, -14.05) * mm, "end": v(45.9, -14.05) * mm});
            skLineSegment(sketch, "E1130", {"start": v(45.9, -14.05) * mm, "end": v(45.2, -14.05) * mm});
            skLineSegment(sketch, "E1131", {"start": v(45.2, -14.05) * mm, "end": v(44.48, -14.05) * mm});
            skLineSegment(sketch, "E1132", {"start": v(44.48, -14.05) * mm, "end": v(43.77, -14.05) * mm});
            skLineSegment(sketch, "E1133", {"start": v(43.77, -14.05) * mm, "end": v(43.06, -14.05) * mm});
            skLineSegment(sketch, "E1134", {"start": v(43.06, -14.05) * mm, "end": v(42.35, -14.05) * mm});
            skLineSegment(sketch, "E1135", {"start": v(42.35, -14.05) * mm, "end": v(41.63, -14.05) * mm});
            skLineSegment(sketch, "E1136", {"start": v(-29.33, -19.97) * mm, "end": v(-29.14, -20.5) * mm});
            skLineSegment(sketch, "E1137", {"start": v(-29.14, -20.5) * mm, "end": v(-28.95, -21.05) * mm});
            skLineSegment(sketch, "E1138", {"start": v(-28.95, -21.05) * mm, "end": v(-28.76, -21.58) * mm});
            skLineSegment(sketch, "E1139", {"start": v(-28.76, -21.58) * mm, "end": v(-28.57, -22.12) * mm});
            skLineSegment(sketch, "E1140", {"start": v(-28.57, -22.12) * mm, "end": v(-28.37, -22.66) * mm});
            skLineSegment(sketch, "E1141", {"start": v(-28.37, -22.66) * mm, "end": v(-28.18, -23.2) * mm});
            skLineSegment(sketch, "E1142", {"start": v(-28.18, -23.2) * mm, "end": v(-28, -23.73) * mm});
            skLineSegment(sketch, "E1143", {"start": v(-28, -23.73) * mm, "end": v(-27.8, -24.27) * mm});
            skLineSegment(sketch, "E1144", {"start": v(-27.8, -24.27) * mm, "end": v(-27.6, -24.8) * mm});
            skLineSegment(sketch, "E1145", {"start": v(-27.6, -24.8) * mm, "end": v(-27.42, -25.34) * mm});
            skLineSegment(sketch, "E1146", {"start": v(-27.42, -25.34) * mm, "end": v(-27.22, -25.88) * mm});
            skLineSegment(sketch, "E1147", {"start": v(-27.22, -25.88) * mm, "end": v(-27.03, -26.41) * mm});
            skLineSegment(sketch, "E1148", {"start": v(-27.03, -26.41) * mm, "end": v(-26.84, -26.95) * mm});
            skLineSegment(sketch, "E1149", {"start": v(-26.84, -26.95) * mm, "end": v(-26.65, -27.49) * mm});
            skLineSegment(sketch, "E1150", {"start": v(-26.65, -27.49) * mm, "end": v(-26.46, -28.02) * mm});
            skLineSegment(sketch, "E1151", {"start": v(-26.46, -28.02) * mm, "end": v(-26.27, -28.56) * mm});
            skLineSegment(sketch, "E1152", {"start": v(-26.27, -28.56) * mm, "end": v(-26.65, -28.56) * mm});
            skLineSegment(sketch, "E1153", {"start": v(-26.65, -28.56) * mm, "end": v(-27.03, -28.56) * mm});
            skLineSegment(sketch, "E1154", {"start": v(-27.03, -28.56) * mm, "end": v(-27.41, -28.56) * mm});
            skLineSegment(sketch, "E1155", {"start": v(-27.41, -28.56) * mm, "end": v(-27.8, -28.56) * mm});
            skLineSegment(sketch, "E1156", {"start": v(-27.8, -28.56) * mm, "end": v(-28.17, -28.56) * mm});
            skLineSegment(sketch, "E1157", {"start": v(-28.17, -28.56) * mm, "end": v(-28.55, -28.56) * mm});
            skLineSegment(sketch, "E1158", {"start": v(-28.55, -28.56) * mm, "end": v(-28.94, -28.56) * mm});
            skLineSegment(sketch, "E1159", {"start": v(-28.94, -28.56) * mm, "end": v(-29.32, -28.56) * mm});
            skLineSegment(sketch, "E1160", {"start": v(-29.32, -28.56) * mm, "end": v(-29.7, -28.56) * mm});
            skLineSegment(sketch, "E1161", {"start": v(-29.7, -28.56) * mm, "end": v(-30.08, -28.56) * mm});
            skLineSegment(sketch, "E1162", {"start": v(-30.08, -28.56) * mm, "end": v(-30.46, -28.56) * mm});
            skLineSegment(sketch, "E1163", {"start": v(-30.46, -28.56) * mm, "end": v(-30.84, -28.56) * mm});
            skLineSegment(sketch, "E1164", {"start": v(-30.84, -28.56) * mm, "end": v(-31.22, -28.56) * mm});
            skLineSegment(sketch, "E1165", {"start": v(-31.22, -28.56) * mm, "end": v(-31.6, -28.56) * mm});
            skLineSegment(sketch, "E1166", {"start": v(-31.6, -28.56) * mm, "end": v(-31.99, -28.56) * mm});
            skLineSegment(sketch, "E1167", {"start": v(-31.99, -28.56) * mm, "end": v(-32.37, -28.56) * mm});
            skLineSegment(sketch, "E1168", {"start": v(-32.37, -28.56) * mm, "end": v(-32.18, -28.02) * mm});
            skLineSegment(sketch, "E1169", {"start": v(-32.18, -28.02) * mm, "end": v(-31.99, -27.49) * mm});
            skLineSegment(sketch, "E1170", {"start": v(-31.99, -27.49) * mm, "end": v(-31.8, -26.95) * mm});
            skLineSegment(sketch, "E1171", {"start": v(-31.8, -26.95) * mm, "end": v(-31.6, -26.41) * mm});
            skLineSegment(sketch, "E1172", {"start": v(-31.6, -26.41) * mm, "end": v(-31.42, -25.88) * mm});
            skLineSegment(sketch, "E1173", {"start": v(-31.42, -25.88) * mm, "end": v(-31.23, -25.34) * mm});
            skLineSegment(sketch, "E1174", {"start": v(-31.23, -25.34) * mm, "end": v(-31.04, -24.8) * mm});
            skLineSegment(sketch, "E1175", {"start": v(-31.04, -24.8) * mm, "end": v(-30.85, -24.27) * mm});
            skLineSegment(sketch, "E1176", {"start": v(-30.85, -24.27) * mm, "end": v(-30.66, -23.73) * mm});
            skLineSegment(sketch, "E1177", {"start": v(-30.66, -23.73) * mm, "end": v(-30.47, -23.2) * mm});
            skLineSegment(sketch, "E1178", {"start": v(-30.47, -23.2) * mm, "end": v(-30.28, -22.66) * mm});
            skLineSegment(sketch, "E1179", {"start": v(-30.28, -22.66) * mm, "end": v(-30.1, -22.12) * mm});
            skLineSegment(sketch, "E1180", {"start": v(-30.1, -22.12) * mm, "end": v(-29.9, -21.58) * mm});
            skLineSegment(sketch, "E1181", {"start": v(-29.9, -21.58) * mm, "end": v(-29.71, -21.05) * mm});
            skLineSegment(sketch, "E1182", {"start": v(-29.71, -21.05) * mm, "end": v(-29.52, -20.5) * mm});
            skLineSegment(sketch, "E1183", {"start": v(-29.52, -20.5) * mm, "end": v(-29.33, -19.97) * mm});
            skLineSegment(sketch, "E1184", {"start": v(-31.3, -14.01) * mm, "end": v(-31.83, -15.43) * mm});
            skLineSegment(sketch, "E1185", {"start": v(-31.83, -15.43) * mm, "end": v(-32.35, -16.85) * mm});
            skLineSegment(sketch, "E1186", {"start": v(-32.35, -16.85) * mm, "end": v(-32.88, -18.27) * mm});
            skLineSegment(sketch, "E1187", {"start": v(-32.88, -18.27) * mm, "end": v(-33.4, -19.7) * mm});
            skLineSegment(sketch, "E1188", {"start": v(-33.4, -19.7) * mm, "end": v(-33.93, -21.12) * mm});
            skLineSegment(sketch, "E1189", {"start": v(-33.93, -21.12) * mm, "end": v(-34.46, -22.54) * mm});
            skLineSegment(sketch, "E1190", {"start": v(-34.46, -22.54) * mm, "end": v(-34.99, -23.96) * mm});
            skLineSegment(sketch, "E1191", {"start": v(-34.99, -23.96) * mm, "end": v(-35.52, -25.38) * mm});
            skLineSegment(sketch, "E1192", {"start": v(-35.52, -25.38) * mm, "end": v(-36.04, -26.8) * mm});
            skLineSegment(sketch, "E1193", {"start": v(-36.04, -26.8) * mm, "end": v(-36.57, -28.22) * mm});
            skLineSegment(sketch, "E1194", {"start": v(-36.57, -28.22) * mm, "end": v(-37.1, -29.64) * mm});
            skLineSegment(sketch, "E1195", {"start": v(-37.1, -29.64) * mm, "end": v(-37.62, -31.06) * mm});
            skLineSegment(sketch, "E1196", {"start": v(-37.62, -31.06) * mm, "end": v(-38.15, -32.49) * mm});
            skLineSegment(sketch, "E1197", {"start": v(-38.15, -32.49) * mm, "end": v(-38.68, -33.9) * mm});
            skLineSegment(sketch, "E1198", {"start": v(-38.68, -33.9) * mm, "end": v(-39.2, -35.33) * mm});
            skLineSegment(sketch, "E1199", {"start": v(-39.2, -35.33) * mm, "end": v(-39.73, -36.75) * mm});
            skLineSegment(sketch, "E1200", {"start": v(-39.73, -36.75) * mm, "end": v(-39.45, -36.75) * mm});
            skLineSegment(sketch, "E1201", {"start": v(-39.45, -36.75) * mm, "end": v(-39.17, -36.75) * mm});
            skLineSegment(sketch, "E1202", {"start": v(-39.17, -36.75) * mm, "end": v(-38.9, -36.75) * mm});
            skLineSegment(sketch, "E1203", {"start": v(-38.9, -36.75) * mm, "end": v(-38.62, -36.75) * mm});
            skLineSegment(sketch, "E1204", {"start": v(-38.62, -36.75) * mm, "end": v(-38.34, -36.75) * mm});
            skLineSegment(sketch, "E1205", {"start": v(-38.34, -36.75) * mm, "end": v(-38.06, -36.75) * mm});
            skLineSegment(sketch, "E1206", {"start": v(-38.06, -36.75) * mm, "end": v(-37.78, -36.75) * mm});
            skLineSegment(sketch, "E1207", {"start": v(-37.78, -36.75) * mm, "end": v(-37.5, -36.75) * mm});
            skLineSegment(sketch, "E1208", {"start": v(-37.5, -36.75) * mm, "end": v(-37.22, -36.75) * mm});
            skLineSegment(sketch, "E1209", {"start": v(-37.22, -36.75) * mm, "end": v(-36.94, -36.75) * mm});
            skLineSegment(sketch, "E1210", {"start": v(-36.94, -36.75) * mm, "end": v(-36.66, -36.75) * mm});
            skLineSegment(sketch, "E1211", {"start": v(-36.66, -36.75) * mm, "end": v(-36.38, -36.75) * mm});
            skLineSegment(sketch, "E1212", {"start": v(-36.38, -36.75) * mm, "end": v(-36.1, -36.75) * mm});
            skLineSegment(sketch, "E1213", {"start": v(-36.1, -36.75) * mm, "end": v(-35.82, -36.75) * mm});
            skLineSegment(sketch, "E1214", {"start": v(-35.82, -36.75) * mm, "end": v(-35.55, -36.75) * mm});
            skLineSegment(sketch, "E1215", {"start": v(-35.55, -36.75) * mm, "end": v(-35.27, -36.75) * mm});
            skLineSegment(sketch, "E1216", {"start": v(-35.27, -36.75) * mm, "end": v(-35.17, -36.47) * mm});
            skLineSegment(sketch, "E1217", {"start": v(-35.17, -36.47) * mm, "end": v(-35.07, -36.19) * mm});
            skLineSegment(sketch, "E1218", {"start": v(-35.07, -36.19) * mm, "end": v(-34.97, -35.9) * mm});
            skLineSegment(sketch, "E1219", {"start": v(-34.97, -35.9) * mm, "end": v(-34.87, -35.63) * mm});
            skLineSegment(sketch, "E1220", {"start": v(-34.87, -35.63) * mm, "end": v(-34.77, -35.34) * mm});
            skLineSegment(sketch, "E1221", {"start": v(-34.77, -35.34) * mm, "end": v(-34.67, -35.06) * mm});
            skLineSegment(sketch, "E1222", {"start": v(-34.67, -35.06) * mm, "end": v(-34.57, -34.78) * mm});
            skLineSegment(sketch, "E1223", {"start": v(-34.57, -34.78) * mm, "end": v(-34.47, -34.5) * mm});
            skLineSegment(sketch, "E1224", {"start": v(-34.47, -34.5) * mm, "end": v(-34.37, -34.22) * mm});
            skLineSegment(sketch, "E1225", {"start": v(-34.37, -34.22) * mm, "end": v(-34.27, -33.94) * mm});
            skLineSegment(sketch, "E1226", {"start": v(-34.27, -33.94) * mm, "end": v(-34.17, -33.66) * mm});
            skLineSegment(sketch, "E1227", {"start": v(-34.17, -33.66) * mm, "end": v(-34.07, -33.38) * mm});
            skLineSegment(sketch, "E1228", {"start": v(-34.07, -33.38) * mm, "end": v(-33.97, -33.1) * mm});
            skLineSegment(sketch, "E1229", {"start": v(-33.97, -33.1) * mm, "end": v(-33.87, -32.82) * mm});
            skLineSegment(sketch, "E1230", {"start": v(-33.87, -32.82) * mm, "end": v(-33.77, -32.54) * mm});
            skLineSegment(sketch, "E1231", {"start": v(-33.77, -32.54) * mm, "end": v(-33.67, -32.25) * mm});
            skLineSegment(sketch, "E1232", {"start": v(-33.67, -32.25) * mm, "end": v(-33.12, -32.25) * mm});
            skLineSegment(sketch, "E1233", {"start": v(-33.12, -32.25) * mm, "end": v(-32.57, -32.25) * mm});
            skLineSegment(sketch, "E1234", {"start": v(-32.57, -32.25) * mm, "end": v(-32.03, -32.25) * mm});
            skLineSegment(sketch, "E1235", {"start": v(-32.03, -32.25) * mm, "end": v(-31.48, -32.25) * mm});
            skLineSegment(sketch, "E1236", {"start": v(-31.48, -32.25) * mm, "end": v(-30.94, -32.25) * mm});
            skLineSegment(sketch, "E1237", {"start": v(-30.94, -32.25) * mm, "end": v(-30.4, -32.25) * mm});
            skLineSegment(sketch, "E1238", {"start": v(-30.4, -32.25) * mm, "end": v(-29.85, -32.25) * mm});
            skLineSegment(sketch, "E1239", {"start": v(-29.85, -32.25) * mm, "end": v(-29.3, -32.25) * mm});
            skLineSegment(sketch, "E1240", {"start": v(-29.3, -32.25) * mm, "end": v(-28.75, -32.25) * mm});
            skLineSegment(sketch, "E1241", {"start": v(-28.75, -32.25) * mm, "end": v(-28.2, -32.25) * mm});
            skLineSegment(sketch, "E1242", {"start": v(-28.2, -32.25) * mm, "end": v(-27.66, -32.25) * mm});
            skLineSegment(sketch, "E1243", {"start": v(-27.66, -32.25) * mm, "end": v(-27.12, -32.25) * mm});
            skLineSegment(sketch, "E1244", {"start": v(-27.12, -32.25) * mm, "end": v(-26.57, -32.25) * mm});
            skLineSegment(sketch, "E1245", {"start": v(-26.57, -32.25) * mm, "end": v(-26.02, -32.25) * mm});
            skLineSegment(sketch, "E1246", {"start": v(-26.02, -32.25) * mm, "end": v(-25.48, -32.25) * mm});
            skLineSegment(sketch, "E1247", {"start": v(-25.48, -32.25) * mm, "end": v(-24.93, -32.25) * mm});
            skLineSegment(sketch, "E1248", {"start": v(-24.93, -32.25) * mm, "end": v(-24.83, -32.54) * mm});
            skLineSegment(sketch, "E1249", {"start": v(-24.83, -32.54) * mm, "end": v(-24.73, -32.82) * mm});
            skLineSegment(sketch, "E1250", {"start": v(-24.73, -32.82) * mm, "end": v(-24.63, -33.1) * mm});
            skLineSegment(sketch, "E1251", {"start": v(-24.63, -33.1) * mm, "end": v(-24.53, -33.38) * mm});
            skLineSegment(sketch, "E1252", {"start": v(-24.53, -33.38) * mm, "end": v(-24.43, -33.66) * mm});
            skLineSegment(sketch, "E1253", {"start": v(-24.43, -33.66) * mm, "end": v(-24.33, -33.94) * mm});
            skLineSegment(sketch, "E1254", {"start": v(-24.33, -33.94) * mm, "end": v(-24.23, -34.22) * mm});
            skLineSegment(sketch, "E1255", {"start": v(-24.23, -34.22) * mm, "end": v(-24.13, -34.5) * mm});
            skLineSegment(sketch, "E1256", {"start": v(-24.13, -34.5) * mm, "end": v(-24.03, -34.78) * mm});
            skLineSegment(sketch, "E1257", {"start": v(-24.03, -34.78) * mm, "end": v(-23.93, -35.06) * mm});
            skLineSegment(sketch, "E1258", {"start": v(-23.93, -35.06) * mm, "end": v(-23.83, -35.34) * mm});
            skLineSegment(sketch, "E1259", {"start": v(-23.83, -35.34) * mm, "end": v(-23.73, -35.63) * mm});
            skLineSegment(sketch, "E1260", {"start": v(-23.73, -35.63) * mm, "end": v(-23.63, -35.9) * mm});
            skLineSegment(sketch, "E1261", {"start": v(-23.63, -35.9) * mm, "end": v(-23.53, -36.19) * mm});
            skLineSegment(sketch, "E1262", {"start": v(-23.53, -36.19) * mm, "end": v(-23.43, -36.47) * mm});
            skLineSegment(sketch, "E1263", {"start": v(-23.43, -36.47) * mm, "end": v(-23.33, -36.75) * mm});
            skLineSegment(sketch, "E1264", {"start": v(-23.33, -36.75) * mm, "end": v(-23.03, -36.75) * mm});
            skLineSegment(sketch, "E1265", {"start": v(-23.03, -36.75) * mm, "end": v(-22.72, -36.75) * mm});
            skLineSegment(sketch, "E1266", {"start": v(-22.72, -36.75) * mm, "end": v(-22.4, -36.75) * mm});
            skLineSegment(sketch, "E1267", {"start": v(-22.4, -36.75) * mm, "end": v(-22.1, -36.75) * mm});
            skLineSegment(sketch, "E1268", {"start": v(-22.1, -36.75) * mm, "end": v(-21.8, -36.75) * mm});
            skLineSegment(sketch, "E1269", {"start": v(-21.8, -36.75) * mm, "end": v(-21.48, -36.75) * mm});
            skLineSegment(sketch, "E1270", {"start": v(-21.48, -36.75) * mm, "end": v(-21.17, -36.75) * mm});
            skLineSegment(sketch, "E1271", {"start": v(-21.17, -36.75) * mm, "end": v(-20.87, -36.75) * mm});
            skLineSegment(sketch, "E1272", {"start": v(-20.87, -36.75) * mm, "end": v(-20.56, -36.75) * mm});
            skLineSegment(sketch, "E1273", {"start": v(-20.56, -36.75) * mm, "end": v(-20.25, -36.75) * mm});
            skLineSegment(sketch, "E1274", {"start": v(-20.25, -36.75) * mm, "end": v(-19.94, -36.75) * mm});
            skLineSegment(sketch, "E1275", {"start": v(-19.94, -36.75) * mm, "end": v(-19.63, -36.75) * mm});
            skLineSegment(sketch, "E1276", {"start": v(-19.63, -36.75) * mm, "end": v(-19.32, -36.75) * mm});
            skLineSegment(sketch, "E1277", {"start": v(-19.32, -36.75) * mm, "end": v(-19.02, -36.75) * mm});
            skLineSegment(sketch, "E1278", {"start": v(-19.02, -36.75) * mm, "end": v(-18.7, -36.75) * mm});
            skLineSegment(sketch, "E1279", {"start": v(-18.7, -36.75) * mm, "end": v(-18.4, -36.75) * mm});
            skLineSegment(sketch, "E1280", {"start": v(-18.4, -36.75) * mm, "end": v(-18.93, -35.33) * mm});
            skLineSegment(sketch, "E1281", {"start": v(-18.93, -35.33) * mm, "end": v(-19.45, -33.9) * mm});
            skLineSegment(sketch, "E1282", {"start": v(-19.45, -33.9) * mm, "end": v(-19.98, -32.49) * mm});
            skLineSegment(sketch, "E1283", {"start": v(-19.98, -32.49) * mm, "end": v(-20.5, -31.06) * mm});
            skLineSegment(sketch, "E1284", {"start": v(-20.5, -31.06) * mm, "end": v(-21.03, -29.64) * mm});
            skLineSegment(sketch, "E1285", {"start": v(-21.03, -29.64) * mm, "end": v(-21.56, -28.22) * mm});
            skLineSegment(sketch, "E1286", {"start": v(-21.56, -28.22) * mm, "end": v(-22.09, -26.8) * mm});
            skLineSegment(sketch, "E1287", {"start": v(-22.09, -26.8) * mm, "end": v(-22.62, -25.38) * mm});
            skLineSegment(sketch, "E1288", {"start": v(-22.62, -25.38) * mm, "end": v(-23.14, -23.96) * mm});
            skLineSegment(sketch, "E1289", {"start": v(-23.14, -23.96) * mm, "end": v(-23.67, -22.54) * mm});
            skLineSegment(sketch, "E1290", {"start": v(-23.67, -22.54) * mm, "end": v(-24.2, -21.12) * mm});
            skLineSegment(sketch, "E1291", {"start": v(-24.2, -21.12) * mm, "end": v(-24.72, -19.7) * mm});
            skLineSegment(sketch, "E1292", {"start": v(-24.72, -19.7) * mm, "end": v(-25.25, -18.27) * mm});
            skLineSegment(sketch, "E1293", {"start": v(-25.25, -18.27) * mm, "end": v(-25.78, -16.85) * mm});
            skLineSegment(sketch, "E1294", {"start": v(-25.78, -16.85) * mm, "end": v(-26.3, -15.43) * mm});
            skLineSegment(sketch, "E1295", {"start": v(-26.3, -15.43) * mm, "end": v(-26.83, -14.01) * mm});
            skLineSegment(sketch, "E1296", {"start": v(-26.83, -14.01) * mm, "end": v(-27.11, -14.01) * mm});
            skLineSegment(sketch, "E1297", {"start": v(-27.11, -14.01) * mm, "end": v(-27.4, -14.01) * mm});
            skLineSegment(sketch, "E1298", {"start": v(-27.4, -14.01) * mm, "end": v(-27.67, -14.01) * mm});
            skLineSegment(sketch, "E1299", {"start": v(-27.67, -14.01) * mm, "end": v(-27.95, -14.01) * mm});
            skLineSegment(sketch, "E1300", {"start": v(-27.95, -14.01) * mm, "end": v(-28.23, -14.01) * mm});
            skLineSegment(sketch, "E1301", {"start": v(-28.23, -14.01) * mm, "end": v(-28.5, -14.01) * mm});
            skLineSegment(sketch, "E1302", {"start": v(-28.5, -14.01) * mm, "end": v(-28.79, -14.01) * mm});
            skLineSegment(sketch, "E1303", {"start": v(-28.79, -14.01) * mm, "end": v(-29.07, -14.01) * mm});
            skLineSegment(sketch, "E1304", {"start": v(-29.07, -14.01) * mm, "end": v(-29.35, -14.01) * mm});
            skLineSegment(sketch, "E1305", {"start": v(-29.35, -14.01) * mm, "end": v(-29.62, -14.01) * mm});
            skLineSegment(sketch, "E1306", {"start": v(-29.62, -14.01) * mm, "end": v(-29.9, -14.01) * mm});
            skLineSegment(sketch, "E1307", {"start": v(-29.9, -14.01) * mm, "end": v(-30.18, -14.01) * mm});
            skLineSegment(sketch, "E1308", {"start": v(-30.18, -14.01) * mm, "end": v(-30.46, -14.01) * mm});
            skLineSegment(sketch, "E1309", {"start": v(-30.46, -14.01) * mm, "end": v(-30.74, -14.01) * mm});
            skLineSegment(sketch, "E1310", {"start": v(-30.74, -14.01) * mm, "end": v(-31.02, -14.01) * mm});
            skLineSegment(sketch, "E1311", {"start": v(-31.02, -14.01) * mm, "end": v(-31.3, -14.01) * mm});
            skLineSegment(sketch, "E1312", {"start": v(75.6, -14.01) * mm, "end": v(75.6, -14.95) * mm});
            skLineSegment(sketch, "E1313", {"start": v(75.6, -14.95) * mm, "end": v(75.6, -15.9) * mm});
            skLineSegment(sketch, "E1314", {"start": v(75.6, -15.9) * mm, "end": v(75.6, -16.84) * mm});
            skLineSegment(sketch, "E1315", {"start": v(75.6, -16.84) * mm, "end": v(75.6, -17.78) * mm});
            skLineSegment(sketch, "E1316", {"start": v(75.6, -17.78) * mm, "end": v(75.6, -18.72) * mm});
            skLineSegment(sketch, "E1317", {"start": v(75.6, -18.72) * mm, "end": v(75.6, -19.67) * mm});
            skLineSegment(sketch, "E1318", {"start": v(75.6, -19.67) * mm, "end": v(75.6, -20.6) * mm});
            skLineSegment(sketch, "E1319", {"start": v(75.6, -20.6) * mm, "end": v(75.6, -21.55) * mm});
            skLineSegment(sketch, "E1320", {"start": v(75.6, -21.55) * mm, "end": v(75.6, -22.5) * mm});
            skLineSegment(sketch, "E1321", {"start": v(75.6, -22.5) * mm, "end": v(75.6, -23.44) * mm});
            skLineSegment(sketch, "E1322", {"start": v(75.6, -23.44) * mm, "end": v(75.6, -24.38) * mm});
            skLineSegment(sketch, "E1323", {"start": v(75.6, -24.38) * mm, "end": v(75.6, -25.32) * mm});
            skLineSegment(sketch, "E1324", {"start": v(75.6, -25.32) * mm, "end": v(75.6, -26.26) * mm});
            skLineSegment(sketch, "E1325", {"start": v(75.6, -26.26) * mm, "end": v(75.6, -27.2) * mm});
            skLineSegment(sketch, "E1326", {"start": v(75.6, -27.2) * mm, "end": v(75.6, -28.15) * mm});
            skLineSegment(sketch, "E1327", {"start": v(75.6, -28.15) * mm, "end": v(75.6, -29.1) * mm});
            skLineSegment(sketch, "E1328", {"start": v(75.6, -29.1) * mm, "end": v(74.96, -28.15) * mm});
            skLineSegment(sketch, "E1329", {"start": v(74.96, -28.15) * mm, "end": v(74.32, -27.2) * mm});
            skLineSegment(sketch, "E1330", {"start": v(74.32, -27.2) * mm, "end": v(73.67, -26.26) * mm});
            skLineSegment(sketch, "E1331", {"start": v(73.67, -26.26) * mm, "end": v(73.03, -25.32) * mm});
            skLineSegment(sketch, "E1332", {"start": v(73.03, -25.32) * mm, "end": v(72.4, -24.38) * mm});
            skLineSegment(sketch, "E1333", {"start": v(72.4, -24.38) * mm, "end": v(71.75, -23.44) * mm});
            skLineSegment(sketch, "E1334", {"start": v(71.75, -23.44) * mm, "end": v(71.1, -22.5) * mm});
            skLineSegment(sketch, "E1335", {"start": v(71.1, -22.5) * mm, "end": v(70.47, -21.55) * mm});
            skLineSegment(sketch, "E1336", {"start": v(70.47, -21.55) * mm, "end": v(69.82, -20.6) * mm});
            skLineSegment(sketch, "E1337", {"start": v(69.82, -20.6) * mm, "end": v(69.18, -19.67) * mm});
            skLineSegment(sketch, "E1338", {"start": v(69.18, -19.67) * mm, "end": v(68.54, -18.72) * mm});
            skLineSegment(sketch, "E1339", {"start": v(68.54, -18.72) * mm, "end": v(67.9, -17.78) * mm});
            skLineSegment(sketch, "E1340", {"start": v(67.9, -17.78) * mm, "end": v(67.26, -16.84) * mm});
            skLineSegment(sketch, "E1341", {"start": v(67.26, -16.84) * mm, "end": v(66.62, -15.9) * mm});
            skLineSegment(sketch, "E1342", {"start": v(66.62, -15.9) * mm, "end": v(65.97, -14.95) * mm});
            skLineSegment(sketch, "E1343", {"start": v(65.97, -14.95) * mm, "end": v(65.33, -14.01) * mm});
            skLineSegment(sketch, "E1344", {"start": v(65.33, -14.01) * mm, "end": v(65.05, -14.01) * mm});
            skLineSegment(sketch, "E1345", {"start": v(65.05, -14.01) * mm, "end": v(64.77, -14.01) * mm});
            skLineSegment(sketch, "E1346", {"start": v(64.77, -14.01) * mm, "end": v(64.48, -14.01) * mm});
            skLineSegment(sketch, "E1347", {"start": v(64.48, -14.01) * mm, "end": v(64.2, -14.01) * mm});
            skLineSegment(sketch, "E1348", {"start": v(64.2, -14.01) * mm, "end": v(63.92, -14.01) * mm});
            skLineSegment(sketch, "E1349", {"start": v(63.92, -14.01) * mm, "end": v(63.63, -14.01) * mm});
            skLineSegment(sketch, "E1350", {"start": v(63.63, -14.01) * mm, "end": v(63.35, -14.01) * mm});
            skLineSegment(sketch, "E1351", {"start": v(63.35, -14.01) * mm, "end": v(63.07, -14.01) * mm});
            skLineSegment(sketch, "E1352", {"start": v(63.07, -14.01) * mm, "end": v(62.78, -14.01) * mm});
            skLineSegment(sketch, "E1353", {"start": v(62.78, -14.01) * mm, "end": v(62.5, -14.01) * mm});
            skLineSegment(sketch, "E1354", {"start": v(62.5, -14.01) * mm, "end": v(62.22, -14.01) * mm});
            skLineSegment(sketch, "E1355", {"start": v(62.22, -14.01) * mm, "end": v(61.93, -14.01) * mm});
            skLineSegment(sketch, "E1356", {"start": v(61.93, -14.01) * mm, "end": v(61.65, -14.01) * mm});
            skLineSegment(sketch, "E1357", {"start": v(61.65, -14.01) * mm, "end": v(61.37, -14.01) * mm});
            skLineSegment(sketch, "E1358", {"start": v(61.37, -14.01) * mm, "end": v(61.08, -14.01) * mm});
            skLineSegment(sketch, "E1359", {"start": v(61.08, -14.01) * mm, "end": v(60.8, -14.01) * mm});
            skLineSegment(sketch, "E1360", {"start": v(60.8, -14.01) * mm, "end": v(60.8, -15.43) * mm});
            skLineSegment(sketch, "E1361", {"start": v(60.8, -15.43) * mm, "end": v(60.8, -16.85) * mm});
            skLineSegment(sketch, "E1362", {"start": v(60.8, -16.85) * mm, "end": v(60.8, -18.27) * mm});
            skLineSegment(sketch, "E1363", {"start": v(60.8, -18.27) * mm, "end": v(60.8, -19.69) * mm});
            skLineSegment(sketch, "E1364", {"start": v(60.8, -19.69) * mm, "end": v(60.8, -21.1) * mm});
            skLineSegment(sketch, "E1365", {"start": v(60.8, -21.1) * mm, "end": v(60.8, -22.53) * mm});
            skLineSegment(sketch, "E1366", {"start": v(60.8, -22.53) * mm, "end": v(60.8, -23.94) * mm});
            skLineSegment(sketch, "E1367", {"start": v(60.8, -23.94) * mm, "end": v(60.8, -25.36) * mm});
            skLineSegment(sketch, "E1368", {"start": v(60.8, -25.36) * mm, "end": v(60.8, -26.78) * mm});
            skLineSegment(sketch, "E1369", {"start": v(60.8, -26.78) * mm, "end": v(60.8, -28.2) * mm});
            skLineSegment(sketch, "E1370", {"start": v(60.8, -28.2) * mm, "end": v(60.8, -29.62) * mm});
            skLineSegment(sketch, "E1371", {"start": v(60.8, -29.62) * mm, "end": v(60.8, -31.04) * mm});
            skLineSegment(sketch, "E1372", {"start": v(60.8, -31.04) * mm, "end": v(60.8, -32.46) * mm});
            skLineSegment(sketch, "E1373", {"start": v(60.8, -32.46) * mm, "end": v(60.8, -33.88) * mm});
            skLineSegment(sketch, "E1374", {"start": v(60.8, -33.88) * mm, "end": v(60.8, -35.3) * mm});
            skLineSegment(sketch, "E1375", {"start": v(60.8, -35.3) * mm, "end": v(60.8, -36.72) * mm});
            skLineSegment(sketch, "E1376", {"start": v(60.8, -36.72) * mm, "end": v(61.08, -36.72) * mm});
            skLineSegment(sketch, "E1377", {"start": v(61.08, -36.72) * mm, "end": v(61.35, -36.72) * mm});
            skLineSegment(sketch, "E1378", {"start": v(61.35, -36.72) * mm, "end": v(61.63, -36.72) * mm});
            skLineSegment(sketch, "E1379", {"start": v(61.63, -36.72) * mm, "end": v(61.9, -36.72) * mm});
            skLineSegment(sketch, "E1380", {"start": v(61.9, -36.72) * mm, "end": v(62.18, -36.72) * mm});
            skLineSegment(sketch, "E1381", {"start": v(62.18, -36.72) * mm, "end": v(62.45, -36.72) * mm});
            skLineSegment(sketch, "E1382", {"start": v(62.45, -36.72) * mm, "end": v(62.73, -36.72) * mm});
            skLineSegment(sketch, "E1383", {"start": v(62.73, -36.72) * mm, "end": v(63, -36.72) * mm});
            skLineSegment(sketch, "E1384", {"start": v(63, -36.72) * mm, "end": v(63.28, -36.72) * mm});
            skLineSegment(sketch, "E1385", {"start": v(63.28, -36.72) * mm, "end": v(63.55, -36.72) * mm});
            skLineSegment(sketch, "E1386", {"start": v(63.55, -36.72) * mm, "end": v(63.83, -36.72) * mm});
            skLineSegment(sketch, "E1387", {"start": v(63.83, -36.72) * mm, "end": v(64.1, -36.72) * mm});
            skLineSegment(sketch, "E1388", {"start": v(64.1, -36.72) * mm, "end": v(64.38, -36.72) * mm});
            skLineSegment(sketch, "E1389", {"start": v(64.38, -36.72) * mm, "end": v(64.65, -36.72) * mm});
            skLineSegment(sketch, "E1390", {"start": v(64.65, -36.72) * mm, "end": v(64.93, -36.72) * mm});
            skLineSegment(sketch, "E1391", {"start": v(64.93, -36.72) * mm, "end": v(65.2, -36.72) * mm});
            skLineSegment(sketch, "E1392", {"start": v(65.2, -36.72) * mm, "end": v(65.2, -35.78) * mm});
            skLineSegment(sketch, "E1393", {"start": v(65.2, -35.78) * mm, "end": v(65.2, -34.84) * mm});
            skLineSegment(sketch, "E1394", {"start": v(65.2, -34.84) * mm, "end": v(65.2, -33.9) * mm});
            skLineSegment(sketch, "E1395", {"start": v(65.2, -33.9) * mm, "end": v(65.2, -32.95) * mm});
            skLineSegment(sketch, "E1396", {"start": v(65.2, -32.95) * mm, "end": v(65.2, -32.01) * mm});
            skLineSegment(sketch, "E1397", {"start": v(65.2, -32.01) * mm, "end": v(65.2, -31.07) * mm});
            skLineSegment(sketch, "E1398", {"start": v(65.2, -31.07) * mm, "end": v(65.2, -30.13) * mm});
            skLineSegment(sketch, "E1399", {"start": v(65.2, -30.13) * mm, "end": v(65.2, -29.2) * mm});
            skLineSegment(sketch, "E1400", {"start": v(65.2, -29.2) * mm, "end": v(65.2, -28.25) * mm});
            skLineSegment(sketch, "E1401", {"start": v(65.2, -28.25) * mm, "end": v(65.2, -27.31) * mm});
            skLineSegment(sketch, "E1402", {"start": v(65.2, -27.31) * mm, "end": v(65.2, -26.37) * mm});
            skLineSegment(sketch, "E1403", {"start": v(65.2, -26.37) * mm, "end": v(65.2, -25.43) * mm});
            skLineSegment(sketch, "E1404", {"start": v(65.2, -25.43) * mm, "end": v(65.2, -24.5) * mm});
            skLineSegment(sketch, "E1405", {"start": v(65.2, -24.5) * mm, "end": v(65.2, -23.55) * mm});
            skLineSegment(sketch, "E1406", {"start": v(65.2, -23.55) * mm, "end": v(65.2, -22.61) * mm});
            skLineSegment(sketch, "E1407", {"start": v(65.2, -22.61) * mm, "end": v(65.2, -21.67) * mm});
            skLineSegment(sketch, "E1408", {"start": v(65.2, -21.67) * mm, "end": v(65.84, -22.61) * mm});
            skLineSegment(sketch, "E1409", {"start": v(65.84, -22.61) * mm, "end": v(66.48, -23.55) * mm});
            skLineSegment(sketch, "E1410", {"start": v(66.48, -23.55) * mm, "end": v(67.12, -24.5) * mm});
            skLineSegment(sketch, "E1411", {"start": v(67.12, -24.5) * mm, "end": v(67.77, -25.43) * mm});
            skLineSegment(sketch, "E1412", {"start": v(67.77, -25.43) * mm, "end": v(68.4, -26.37) * mm});
            skLineSegment(sketch, "E1413", {"start": v(68.4, -26.37) * mm, "end": v(69.05, -27.31) * mm});
            skLineSegment(sketch, "E1414", {"start": v(69.05, -27.31) * mm, "end": v(69.7, -28.25) * mm});
            skLineSegment(sketch, "E1415", {"start": v(69.7, -28.25) * mm, "end": v(70.33, -29.2) * mm});
            skLineSegment(sketch, "E1416", {"start": v(70.33, -29.2) * mm, "end": v(70.97, -30.13) * mm});
            skLineSegment(sketch, "E1417", {"start": v(70.97, -30.13) * mm, "end": v(71.62, -31.07) * mm});
            skLineSegment(sketch, "E1418", {"start": v(71.62, -31.07) * mm, "end": v(72.26, -32.01) * mm});
            skLineSegment(sketch, "E1419", {"start": v(72.26, -32.01) * mm, "end": v(72.9, -32.95) * mm});
            skLineSegment(sketch, "E1420", {"start": v(72.9, -32.95) * mm, "end": v(73.54, -33.9) * mm});
            skLineSegment(sketch, "E1421", {"start": v(73.54, -33.9) * mm, "end": v(74.18, -34.84) * mm});
            skLineSegment(sketch, "E1422", {"start": v(74.18, -34.84) * mm, "end": v(74.82, -35.78) * mm});
            skLineSegment(sketch, "E1423", {"start": v(74.82, -35.78) * mm, "end": v(75.47, -36.72) * mm});
            skLineSegment(sketch, "E1424", {"start": v(75.47, -36.72) * mm, "end": v(75.75, -36.72) * mm});
            skLineSegment(sketch, "E1425", {"start": v(75.75, -36.72) * mm, "end": v(76.03, -36.72) * mm});
            skLineSegment(sketch, "E1426", {"start": v(76.03, -36.72) * mm, "end": v(76.32, -36.72) * mm});
            skLineSegment(sketch, "E1427", {"start": v(76.32, -36.72) * mm, "end": v(76.6, -36.72) * mm});
            skLineSegment(sketch, "E1428", {"start": v(76.6, -36.72) * mm, "end": v(76.88, -36.72) * mm});
            skLineSegment(sketch, "E1429", {"start": v(76.88, -36.72) * mm, "end": v(77.17, -36.72) * mm});
            skLineSegment(sketch, "E1430", {"start": v(77.17, -36.72) * mm, "end": v(77.45, -36.72) * mm});
            skLineSegment(sketch, "E1431", {"start": v(77.45, -36.72) * mm, "end": v(77.73, -36.72) * mm});
            skLineSegment(sketch, "E1432", {"start": v(77.73, -36.72) * mm, "end": v(78.02, -36.72) * mm});
            skLineSegment(sketch, "E1433", {"start": v(78.02, -36.72) * mm, "end": v(78.3, -36.72) * mm});
            skLineSegment(sketch, "E1434", {"start": v(78.3, -36.72) * mm, "end": v(78.58, -36.72) * mm});
            skLineSegment(sketch, "E1435", {"start": v(78.58, -36.72) * mm, "end": v(78.87, -36.72) * mm});
            skLineSegment(sketch, "E1436", {"start": v(78.87, -36.72) * mm, "end": v(79.15, -36.72) * mm});
            skLineSegment(sketch, "E1437", {"start": v(79.15, -36.72) * mm, "end": v(79.43, -36.72) * mm});
            skLineSegment(sketch, "E1438", {"start": v(79.43, -36.72) * mm, "end": v(79.72, -36.72) * mm});
            skLineSegment(sketch, "E1439", {"start": v(79.72, -36.72) * mm, "end": v(80, -36.72) * mm});
            skLineSegment(sketch, "E1440", {"start": v(80, -36.72) * mm, "end": v(80, -35.3) * mm});
            skLineSegment(sketch, "E1441", {"start": v(80, -35.3) * mm, "end": v(80, -33.88) * mm});
            skLineSegment(sketch, "E1442", {"start": v(80, -33.88) * mm, "end": v(80, -32.46) * mm});
            skLineSegment(sketch, "E1443", {"start": v(80, -32.46) * mm, "end": v(80, -31.04) * mm});
            skLineSegment(sketch, "E1444", {"start": v(80, -31.04) * mm, "end": v(80, -29.62) * mm});
            skLineSegment(sketch, "E1445", {"start": v(80, -29.62) * mm, "end": v(80, -28.2) * mm});
            skLineSegment(sketch, "E1446", {"start": v(80, -28.2) * mm, "end": v(80, -26.78) * mm});
            skLineSegment(sketch, "E1447", {"start": v(80, -26.78) * mm, "end": v(80, -25.36) * mm});
            skLineSegment(sketch, "E1448", {"start": v(80, -25.36) * mm, "end": v(80, -23.94) * mm});
            skLineSegment(sketch, "E1449", {"start": v(80, -23.94) * mm, "end": v(80, -22.53) * mm});
            skLineSegment(sketch, "E1450", {"start": v(80, -22.53) * mm, "end": v(80, -21.1) * mm});
            skLineSegment(sketch, "E1451", {"start": v(80, -21.1) * mm, "end": v(80, -19.69) * mm});
            skLineSegment(sketch, "E1452", {"start": v(80, -19.69) * mm, "end": v(80, -18.27) * mm});
            skLineSegment(sketch, "E1453", {"start": v(80, -18.27) * mm, "end": v(80, -16.85) * mm});
            skLineSegment(sketch, "E1454", {"start": v(80, -16.85) * mm, "end": v(80, -15.43) * mm});
            skLineSegment(sketch, "E1455", {"start": v(80, -15.43) * mm, "end": v(80, -14.01) * mm});
            skLineSegment(sketch, "E1456", {"start": v(80, -14.01) * mm, "end": v(79.73, -14.01) * mm});
            skLineSegment(sketch, "E1457", {"start": v(79.73, -14.01) * mm, "end": v(79.45, -14.01) * mm});
            skLineSegment(sketch, "E1458", {"start": v(79.45, -14.01) * mm, "end": v(79.18, -14.01) * mm});
            skLineSegment(sketch, "E1459", {"start": v(79.18, -14.01) * mm, "end": v(78.9, -14.01) * mm});
            skLineSegment(sketch, "E1460", {"start": v(78.9, -14.01) * mm, "end": v(78.63, -14.01) * mm});
            skLineSegment(sketch, "E1461", {"start": v(78.63, -14.01) * mm, "end": v(78.35, -14.01) * mm});
            skLineSegment(sketch, "E1462", {"start": v(78.35, -14.01) * mm, "end": v(78.08, -14.01) * mm});
            skLineSegment(sketch, "E1463", {"start": v(78.08, -14.01) * mm, "end": v(77.8, -14.01) * mm});
            skLineSegment(sketch, "E1464", {"start": v(77.8, -14.01) * mm, "end": v(77.53, -14.01) * mm});
            skLineSegment(sketch, "E1465", {"start": v(77.53, -14.01) * mm, "end": v(77.25, -14.01) * mm});
            skLineSegment(sketch, "E1466", {"start": v(77.25, -14.01) * mm, "end": v(76.98, -14.01) * mm});
            skLineSegment(sketch, "E1467", {"start": v(76.98, -14.01) * mm, "end": v(76.7, -14.01) * mm});
            skLineSegment(sketch, "E1468", {"start": v(76.7, -14.01) * mm, "end": v(76.43, -14.01) * mm});
            skLineSegment(sketch, "E1469", {"start": v(76.43, -14.01) * mm, "end": v(76.15, -14.01) * mm});
            skLineSegment(sketch, "E1470", {"start": v(76.15, -14.01) * mm, "end": v(75.88, -14.01) * mm});
            skLineSegment(sketch, "E1471", {"start": v(75.88, -14.01) * mm, "end": v(75.6, -14.01) * mm});
            skLineSegment(sketch, "E1472", {"start": v(-24.83, 36.75) * mm, "end": v(-25.16, 36.73) * mm});
            skLineSegment(sketch, "E1473", {"start": v(-25.16, 36.73) * mm, "end": v(-25.49, 36.68) * mm});
            skLineSegment(sketch, "E1474", {"start": v(-25.49, 36.68) * mm, "end": v(-25.8, 36.6) * mm});
            skLineSegment(sketch, "E1475", {"start": v(-25.8, 36.6) * mm, "end": v(-26.1, 36.5) * mm});
            skLineSegment(sketch, "E1476", {"start": v(-26.1, 36.5) * mm, "end": v(-26.38, 36.36) * mm});
            skLineSegment(sketch, "E1477", {"start": v(-26.38, 36.36) * mm, "end": v(-26.65, 36.2) * mm});
            skLineSegment(sketch, "E1478", {"start": v(-26.65, 36.2) * mm, "end": v(-26.9, 36) * mm});
            skLineSegment(sketch, "E1479", {"start": v(-26.9, 36) * mm, "end": v(-27.13, 35.8) * mm});
            skLineSegment(sketch, "E1480", {"start": v(-27.13, 35.8) * mm, "end": v(-27.34, 35.56) * mm});
            skLineSegment(sketch, "E1481", {"start": v(-27.34, 35.56) * mm, "end": v(-27.53, 35.31) * mm});
            skLineSegment(sketch, "E1482", {"start": v(-27.53, 35.31) * mm, "end": v(-27.7, 35.05) * mm});
            skLineSegment(sketch, "E1483", {"start": v(-27.7, 35.05) * mm, "end": v(-27.83, 34.76) * mm});
            skLineSegment(sketch, "E1484", {"start": v(-27.83, 34.76) * mm, "end": v(-27.94, 34.46) * mm});
            skLineSegment(sketch, "E1485", {"start": v(-27.94, 34.46) * mm, "end": v(-28.02, 34.15) * mm});
            skLineSegment(sketch, "E1486", {"start": v(-28.02, 34.15) * mm, "end": v(-28.07, 33.83) * mm});
            skLineSegment(sketch, "E1487", {"start": v(-28.07, 33.83) * mm, "end": v(-28.09, 33.5) * mm});
            skLineSegment(sketch, "E1488", {"start": v(-28.09, 33.5) * mm, "end": v(-28.09, 33.27) * mm});
            skLineSegment(sketch, "E1489", {"start": v(-28.09, 33.27) * mm, "end": v(-28.09, 33.04) * mm});
            skLineSegment(sketch, "E1490", {"start": v(-28.09, 33.04) * mm, "end": v(-28.09, 32.8) * mm});
            skLineSegment(sketch, "E1491", {"start": v(-28.09, 32.8) * mm, "end": v(-28.09, 32.58) * mm});
            skLineSegment(sketch, "E1492", {"start": v(-28.09, 32.58) * mm, "end": v(-28.09, 32.35) * mm});
            skLineSegment(sketch, "E1493", {"start": v(-28.09, 32.35) * mm, "end": v(-28.09, 32.12) * mm});
            skLineSegment(sketch, "E1494", {"start": v(-28.09, 32.12) * mm, "end": v(-28.09, 31.9) * mm});
            skLineSegment(sketch, "E1495", {"start": v(-28.09, 31.9) * mm, "end": v(-28.09, 31.67) * mm});
            skLineSegment(sketch, "E1496", {"start": v(-28.09, 31.67) * mm, "end": v(-28.09, 31.44) * mm});
            skLineSegment(sketch, "E1497", {"start": v(-28.09, 31.44) * mm, "end": v(-28.09, 31.21) * mm});
            skLineSegment(sketch, "E1498", {"start": v(-28.09, 31.21) * mm, "end": v(-28.09, 30.98) * mm});
            skLineSegment(sketch, "E1499", {"start": v(-28.09, 30.98) * mm, "end": v(-28.09, 30.75) * mm});
            skLineSegment(sketch, "E1500", {"start": v(-28.09, 30.75) * mm, "end": v(-28.09, 30.53) * mm});
            skLineSegment(sketch, "E1501", {"start": v(-28.09, 30.53) * mm, "end": v(-28.09, 30.3) * mm});
            skLineSegment(sketch, "E1502", {"start": v(-28.09, 30.3) * mm, "end": v(-28.09, 30.07) * mm});
            skLineSegment(sketch, "E1503", {"start": v(-28.09, 30.07) * mm, "end": v(-28.09, 29.84) * mm});
            skLineSegment(sketch, "E1504", {"start": v(-28.09, 29.84) * mm, "end": v(-27.85, 29.84) * mm});
            skLineSegment(sketch, "E1505", {"start": v(-27.85, 29.84) * mm, "end": v(-27.62, 29.84) * mm});
            skLineSegment(sketch, "E1506", {"start": v(-27.62, 29.84) * mm, "end": v(-27.38, 29.84) * mm});
            skLineSegment(sketch, "E1507", {"start": v(-27.38, 29.84) * mm, "end": v(-27.15, 29.84) * mm});
            skLineSegment(sketch, "E1508", {"start": v(-27.15, 29.84) * mm, "end": v(-26.9, 29.84) * mm});
            skLineSegment(sketch, "E1509", {"start": v(-26.9, 29.84) * mm, "end": v(-26.67, 29.84) * mm});
            skLineSegment(sketch, "E1510", {"start": v(-26.67, 29.84) * mm, "end": v(-26.44, 29.84) * mm});
            skLineSegment(sketch, "E1511", {"start": v(-26.44, 29.84) * mm, "end": v(-26.2, 29.84) * mm});
            skLineSegment(sketch, "E1512", {"start": v(-26.2, 29.84) * mm, "end": v(-25.97, 29.84) * mm});
            skLineSegment(sketch, "E1513", {"start": v(-25.97, 29.84) * mm, "end": v(-25.73, 29.84) * mm});
            skLineSegment(sketch, "E1514", {"start": v(-25.73, 29.84) * mm, "end": v(-25.5, 29.84) * mm});
            skLineSegment(sketch, "E1515", {"start": v(-25.5, 29.84) * mm, "end": v(-25.26, 29.84) * mm});
            skLineSegment(sketch, "E1516", {"start": v(-25.26, 29.84) * mm, "end": v(-25.02, 29.84) * mm});
            skLineSegment(sketch, "E1517", {"start": v(-25.02, 29.84) * mm, "end": v(-24.79, 29.84) * mm});
            skLineSegment(sketch, "E1518", {"start": v(-24.79, 29.84) * mm, "end": v(-24.55, 29.84) * mm});
            skLineSegment(sketch, "E1519", {"start": v(-24.55, 29.84) * mm, "end": v(-24.32, 29.84) * mm});
            skLineSegment(sketch, "E1520", {"start": v(-24.32, 29.84) * mm, "end": v(-24.32, 30.02) * mm});
            skLineSegment(sketch, "E1521", {"start": v(-24.32, 30.02) * mm, "end": v(-24.32, 30.2) * mm});
            skLineSegment(sketch, "E1522", {"start": v(-24.32, 30.2) * mm, "end": v(-24.32, 30.4) * mm});
            skLineSegment(sketch, "E1523", {"start": v(-24.32, 30.4) * mm, "end": v(-24.32, 30.58) * mm});
            skLineSegment(sketch, "E1524", {"start": v(-24.32, 30.58) * mm, "end": v(-24.32, 30.76) * mm});
            skLineSegment(sketch, "E1525", {"start": v(-24.32, 30.76) * mm, "end": v(-24.32, 30.94) * mm});
            skLineSegment(sketch, "E1526", {"start": v(-24.32, 30.94) * mm, "end": v(-24.32, 31.13) * mm});
            skLineSegment(sketch, "E1527", {"start": v(-24.32, 31.13) * mm, "end": v(-24.32, 31.31) * mm});
            skLineSegment(sketch, "E1528", {"start": v(-24.32, 31.31) * mm, "end": v(-24.32, 31.5) * mm});
            skLineSegment(sketch, "E1529", {"start": v(-24.32, 31.5) * mm, "end": v(-24.32, 31.68) * mm});
            skLineSegment(sketch, "E1530", {"start": v(-24.32, 31.68) * mm, "end": v(-24.32, 31.86) * mm});
            skLineSegment(sketch, "E1531", {"start": v(-24.32, 31.86) * mm, "end": v(-24.32, 32.05) * mm});
            skLineSegment(sketch, "E1532", {"start": v(-24.32, 32.05) * mm, "end": v(-24.32, 32.23) * mm});
            skLineSegment(sketch, "E1533", {"start": v(-24.32, 32.23) * mm, "end": v(-24.32, 32.41) * mm});
            skLineSegment(sketch, "E1534", {"start": v(-24.32, 32.41) * mm, "end": v(-24.32, 32.6) * mm});
            skLineSegment(sketch, "E1535", {"start": v(-24.32, 32.6) * mm, "end": v(-24.32, 32.78) * mm});
            skLineSegment(sketch, "E1536", {"start": v(-24.32, 32.78) * mm, "end": v(-24.31, 32.85) * mm});
            skLineSegment(sketch, "E1537", {"start": v(-24.31, 32.85) * mm, "end": v(-24.3, 32.92) * mm});
            skLineSegment(sketch, "E1538", {"start": v(-24.3, 32.92) * mm, "end": v(-24.29, 32.98) * mm});
            skLineSegment(sketch, "E1539", {"start": v(-24.29, 32.98) * mm, "end": v(-24.27, 33.04) * mm});
            skLineSegment(sketch, "E1540", {"start": v(-24.27, 33.04) * mm, "end": v(-24.24, 33.1) * mm});
            skLineSegment(sketch, "E1541", {"start": v(-24.24, 33.1) * mm, "end": v(-24.2, 33.15) * mm});
            skLineSegment(sketch, "E1542", {"start": v(-24.2, 33.15) * mm, "end": v(-24.17, 33.2) * mm});
            skLineSegment(sketch, "E1543", {"start": v(-24.17, 33.2) * mm, "end": v(-24.13, 33.25) * mm});
            skLineSegment(sketch, "E1544", {"start": v(-24.13, 33.25) * mm, "end": v(-24.08, 33.29) * mm});
            skLineSegment(sketch, "E1545", {"start": v(-24.08, 33.29) * mm, "end": v(-24.04, 33.33) * mm});
            skLineSegment(sketch, "E1546", {"start": v(-24.04, 33.33) * mm, "end": v(-23.98, 33.36) * mm});
            skLineSegment(sketch, "E1547", {"start": v(-23.98, 33.36) * mm, "end": v(-23.93, 33.39) * mm});
            skLineSegment(sketch, "E1548", {"start": v(-23.93, 33.39) * mm, "end": v(-23.87, 33.4) * mm});
            skLineSegment(sketch, "E1549", {"start": v(-23.87, 33.4) * mm, "end": v(-23.81, 33.42) * mm});
            skLineSegment(sketch, "E1550", {"start": v(-23.81, 33.42) * mm, "end": v(-23.75, 33.43) * mm});
            skLineSegment(sketch, "E1551", {"start": v(-23.75, 33.43) * mm, "end": v(-23.69, 33.44) * mm});
            skLineSegment(sketch, "E1552", {"start": v(-23.69, 33.44) * mm, "end": v(-23.42, 33.44) * mm});
            skLineSegment(sketch, "E1553", {"start": v(-23.42, 33.44) * mm, "end": v(-23.15, 33.44) * mm});
            skLineSegment(sketch, "E1554", {"start": v(-23.15, 33.44) * mm, "end": v(-22.88, 33.44) * mm});
            skLineSegment(sketch, "E1555", {"start": v(-22.88, 33.44) * mm, "end": v(-22.6, 33.44) * mm});
            skLineSegment(sketch, "E1556", {"start": v(-22.6, 33.44) * mm, "end": v(-22.34, 33.44) * mm});
            skLineSegment(sketch, "E1557", {"start": v(-22.34, 33.44) * mm, "end": v(-22.07, 33.44) * mm});
            skLineSegment(sketch, "E1558", {"start": v(-22.07, 33.44) * mm, "end": v(-21.8, 33.44) * mm});
            skLineSegment(sketch, "E1559", {"start": v(-21.8, 33.44) * mm, "end": v(-21.53, 33.44) * mm});
            skLineSegment(sketch, "E1560", {"start": v(-21.53, 33.44) * mm, "end": v(-21.26, 33.44) * mm});
            skLineSegment(sketch, "E1561", {"start": v(-21.26, 33.44) * mm, "end": v(-20.99, 33.44) * mm});
            skLineSegment(sketch, "E1562", {"start": v(-20.99, 33.44) * mm, "end": v(-20.72, 33.44) * mm});
            skLineSegment(sketch, "E1563", {"start": v(-20.72, 33.44) * mm, "end": v(-20.45, 33.44) * mm});
            skLineSegment(sketch, "E1564", {"start": v(-20.45, 33.44) * mm, "end": v(-20.18, 33.44) * mm});
            skLineSegment(sketch, "E1565", {"start": v(-20.18, 33.44) * mm, "end": v(-19.91, 33.44) * mm});
            skLineSegment(sketch, "E1566", {"start": v(-19.91, 33.44) * mm, "end": v(-19.64, 33.44) * mm});
            skLineSegment(sketch, "E1567", {"start": v(-19.64, 33.44) * mm, "end": v(-19.37, 33.44) * mm});
            skLineSegment(sketch, "E1568", {"start": v(-19.37, 33.44) * mm, "end": v(-19.27, 33.43) * mm});
            skLineSegment(sketch, "E1569", {"start": v(-19.27, 33.43) * mm, "end": v(-19.17, 33.42) * mm});
            skLineSegment(sketch, "E1570", {"start": v(-19.17, 33.42) * mm, "end": v(-19.08, 33.4) * mm});
            skLineSegment(sketch, "E1571", {"start": v(-19.08, 33.4) * mm, "end": v(-19, 33.36) * mm});
            skLineSegment(sketch, "E1572", {"start": v(-19, 33.36) * mm, "end": v(-18.9, 33.32) * mm});
            skLineSegment(sketch, "E1573", {"start": v(-18.9, 33.32) * mm, "end": v(-18.83, 33.27) * mm});
            skLineSegment(sketch, "E1574", {"start": v(-18.83, 33.27) * mm, "end": v(-18.75, 33.22) * mm});
            skLineSegment(sketch, "E1575", {"start": v(-18.75, 33.22) * mm, "end": v(-18.68, 33.15) * mm});
            skLineSegment(sketch, "E1576", {"start": v(-18.68, 33.15) * mm, "end": v(-18.62, 33.09) * mm});
            skLineSegment(sketch, "E1577", {"start": v(-18.62, 33.09) * mm, "end": v(-18.56, 33.01) * mm});
            skLineSegment(sketch, "E1578", {"start": v(-18.56, 33.01) * mm, "end": v(-18.52, 32.93) * mm});
            skLineSegment(sketch, "E1579", {"start": v(-18.52, 32.93) * mm, "end": v(-18.48, 32.85) * mm});
            skLineSegment(sketch, "E1580", {"start": v(-18.48, 32.85) * mm, "end": v(-18.44, 32.76) * mm});
            skLineSegment(sketch, "E1581", {"start": v(-18.44, 32.76) * mm, "end": v(-18.42, 32.66) * mm});
            skLineSegment(sketch, "E1582", {"start": v(-18.42, 32.66) * mm, "end": v(-18.4, 32.57) * mm});
            skLineSegment(sketch, "E1583", {"start": v(-18.4, 32.57) * mm, "end": v(-18.4, 32.47) * mm});
            skLineSegment(sketch, "E1584", {"start": v(-18.4, 32.47) * mm, "end": v(-18.4, 32.33) * mm});
            skLineSegment(sketch, "E1585", {"start": v(-18.4, 32.33) * mm, "end": v(-18.4, 32.2) * mm});
            skLineSegment(sketch, "E1586", {"start": v(-18.4, 32.2) * mm, "end": v(-18.4, 32.06) * mm});
            skLineSegment(sketch, "E1587", {"start": v(-18.4, 32.06) * mm, "end": v(-18.4, 31.92) * mm});
            skLineSegment(sketch, "E1588", {"start": v(-18.4, 31.92) * mm, "end": v(-18.4, 31.79) * mm});
            skLineSegment(sketch, "E1589", {"start": v(-18.4, 31.79) * mm, "end": v(-18.4, 31.65) * mm});
            skLineSegment(sketch, "E1590", {"start": v(-18.4, 31.65) * mm, "end": v(-18.4, 31.52) * mm});
            skLineSegment(sketch, "E1591", {"start": v(-18.4, 31.52) * mm, "end": v(-18.4, 31.38) * mm});
            skLineSegment(sketch, "E1592", {"start": v(-18.4, 31.38) * mm, "end": v(-18.4, 31.25) * mm});
            skLineSegment(sketch, "E1593", {"start": v(-18.4, 31.25) * mm, "end": v(-18.4, 31.11) * mm});
            skLineSegment(sketch, "E1594", {"start": v(-18.4, 31.11) * mm, "end": v(-18.4, 30.97) * mm});
            skLineSegment(sketch, "E1595", {"start": v(-18.4, 30.97) * mm, "end": v(-18.4, 30.84) * mm});
            skLineSegment(sketch, "E1596", {"start": v(-18.4, 30.84) * mm, "end": v(-18.4, 30.7) * mm});
            skLineSegment(sketch, "E1597", {"start": v(-18.4, 30.7) * mm, "end": v(-18.4, 30.57) * mm});
            skLineSegment(sketch, "E1598", {"start": v(-18.4, 30.57) * mm, "end": v(-18.4, 30.43) * mm});
            skLineSegment(sketch, "E1599", {"start": v(-18.4, 30.43) * mm, "end": v(-18.4, 30.3) * mm});
            skLineSegment(sketch, "E1600", {"start": v(-18.4, 30.3) * mm, "end": v(-18.4, 30.25) * mm});
            skLineSegment(sketch, "E1601", {"start": v(-18.4, 30.25) * mm, "end": v(-18.4, 30.2) * mm});
            skLineSegment(sketch, "E1602", {"start": v(-18.4, 30.2) * mm, "end": v(-18.41, 30.15) * mm});
            skLineSegment(sketch, "E1603", {"start": v(-18.41, 30.15) * mm, "end": v(-18.42, 30.1) * mm});
            skLineSegment(sketch, "E1604", {"start": v(-18.42, 30.1) * mm, "end": v(-18.43, 30.05) * mm});
            skLineSegment(sketch, "E1605", {"start": v(-18.43, 30.05) * mm, "end": v(-18.45, 30) * mm});
            skLineSegment(sketch, "E1606", {"start": v(-18.45, 30) * mm, "end": v(-18.46, 29.96) * mm});
            skLineSegment(sketch, "E1607", {"start": v(-18.46, 29.96) * mm, "end": v(-18.48, 29.9) * mm});
            skLineSegment(sketch, "E1608", {"start": v(-18.48, 29.9) * mm, "end": v(-18.5, 29.86) * mm});
            skLineSegment(sketch, "E1609", {"start": v(-18.5, 29.86) * mm, "end": v(-18.53, 29.82) * mm});
            skLineSegment(sketch, "E1610", {"start": v(-18.53, 29.82) * mm, "end": v(-18.55, 29.77) * mm});
            skLineSegment(sketch, "E1611", {"start": v(-18.55, 29.77) * mm, "end": v(-18.58, 29.73) * mm});
            skLineSegment(sketch, "E1612", {"start": v(-18.58, 29.73) * mm, "end": v(-18.6, 29.7) * mm});
            skLineSegment(sketch, "E1613", {"start": v(-18.6, 29.7) * mm, "end": v(-18.64, 29.65) * mm});
            skLineSegment(sketch, "E1614", {"start": v(-18.64, 29.65) * mm, "end": v(-18.68, 29.62) * mm});
            skLineSegment(sketch, "E1615", {"start": v(-18.68, 29.62) * mm, "end": v(-18.71, 29.58) * mm});
            skLineSegment(sketch, "E1616", {"start": v(-18.71, 29.58) * mm, "end": v(-19.27, 29) * mm});
            skLineSegment(sketch, "E1617", {"start": v(-19.27, 29) * mm, "end": v(-19.83, 28.43) * mm});
            skLineSegment(sketch, "E1618", {"start": v(-19.83, 28.43) * mm, "end": v(-20.4, 27.86) * mm});
            skLineSegment(sketch, "E1619", {"start": v(-20.4, 27.86) * mm, "end": v(-20.95, 27.29) * mm});
            skLineSegment(sketch, "E1620", {"start": v(-20.95, 27.29) * mm, "end": v(-21.5, 26.71) * mm});
            skLineSegment(sketch, "E1621", {"start": v(-21.5, 26.71) * mm, "end": v(-22.07, 26.14) * mm});
            skLineSegment(sketch, "E1622", {"start": v(-22.07, 26.14) * mm, "end": v(-22.63, 25.56) * mm});
            skLineSegment(sketch, "E1623", {"start": v(-22.63, 25.56) * mm, "end": v(-23.19, 24.99) * mm});
            skLineSegment(sketch, "E1624", {"start": v(-23.19, 24.99) * mm, "end": v(-23.75, 24.41) * mm});
            skLineSegment(sketch, "E1625", {"start": v(-23.75, 24.41) * mm, "end": v(-24.3, 23.84) * mm});
            skLineSegment(sketch, "E1626", {"start": v(-24.3, 23.84) * mm, "end": v(-24.86, 23.26) * mm});
            skLineSegment(sketch, "E1627", {"start": v(-24.86, 23.26) * mm, "end": v(-25.42, 22.69) * mm});
            skLineSegment(sketch, "E1628", {"start": v(-25.42, 22.69) * mm, "end": v(-25.98, 22.12) * mm});
            skLineSegment(sketch, "E1629", {"start": v(-25.98, 22.12) * mm, "end": v(-26.54, 21.54) * mm});
            skLineSegment(sketch, "E1630", {"start": v(-26.54, 21.54) * mm, "end": v(-27.1, 20.97) * mm});
            skLineSegment(sketch, "E1631", {"start": v(-27.1, 20.97) * mm, "end": v(-27.66, 20.4) * mm});
            skLineSegment(sketch, "E1632", {"start": v(-27.66, 20.4) * mm, "end": v(-27.66, 20.2) * mm});
            skLineSegment(sketch, "E1633", {"start": v(-27.66, 20.2) * mm, "end": v(-27.66, 20) * mm});
            skLineSegment(sketch, "E1634", {"start": v(-27.66, 20) * mm, "end": v(-27.66, 19.8) * mm});
            skLineSegment(sketch, "E1635", {"start": v(-27.66, 19.8) * mm, "end": v(-27.66, 19.61) * mm});
            skLineSegment(sketch, "E1636", {"start": v(-27.66, 19.61) * mm, "end": v(-27.66, 19.42) * mm});
            skLineSegment(sketch, "E1637", {"start": v(-27.66, 19.42) * mm, "end": v(-27.66, 19.23) * mm});
            skLineSegment(sketch, "E1638", {"start": v(-27.66, 19.23) * mm, "end": v(-27.66, 19.03) * mm});
            skLineSegment(sketch, "E1639", {"start": v(-27.66, 19.03) * mm, "end": v(-27.66, 18.84) * mm});
            skLineSegment(sketch, "E1640", {"start": v(-27.66, 18.84) * mm, "end": v(-27.66, 18.64) * mm});
            skLineSegment(sketch, "E1641", {"start": v(-27.66, 18.64) * mm, "end": v(-27.66, 18.45) * mm});
            skLineSegment(sketch, "E1642", {"start": v(-27.66, 18.45) * mm, "end": v(-27.66, 18.25) * mm});
            skLineSegment(sketch, "E1643", {"start": v(-27.66, 18.25) * mm, "end": v(-27.66, 18.06) * mm});
            skLineSegment(sketch, "E1644", {"start": v(-27.66, 18.06) * mm, "end": v(-27.66, 17.86) * mm});
            skLineSegment(sketch, "E1645", {"start": v(-27.66, 17.86) * mm, "end": v(-27.66, 17.67) * mm});
            skLineSegment(sketch, "E1646", {"start": v(-27.66, 17.67) * mm, "end": v(-27.66, 17.48) * mm});
            skLineSegment(sketch, "E1647", {"start": v(-27.66, 17.48) * mm, "end": v(-27.66, 17.28) * mm});
            skLineSegment(sketch, "E1648", {"start": v(-27.66, 17.28) * mm, "end": v(-26.84, 17.28) * mm});
            skLineSegment(sketch, "E1649", {"start": v(-26.84, 17.28) * mm, "end": v(-26.03, 17.28) * mm});
            skLineSegment(sketch, "E1650", {"start": v(-26.03, 17.28) * mm, "end": v(-25.22, 17.28) * mm});
            skLineSegment(sketch, "E1651", {"start": v(-25.22, 17.28) * mm, "end": v(-24.4, 17.28) * mm});
            skLineSegment(sketch, "E1652", {"start": v(-24.4, 17.28) * mm, "end": v(-23.59, 17.28) * mm});
            skLineSegment(sketch, "E1653", {"start": v(-23.59, 17.28) * mm, "end": v(-22.77, 17.28) * mm});
            skLineSegment(sketch, "E1654", {"start": v(-22.77, 17.28) * mm, "end": v(-21.96, 17.28) * mm});
            skLineSegment(sketch, "E1655", {"start": v(-21.96, 17.28) * mm, "end": v(-21.14, 17.28) * mm});
            skLineSegment(sketch, "E1656", {"start": v(-21.14, 17.28) * mm, "end": v(-20.33, 17.28) * mm});
            skLineSegment(sketch, "E1657", {"start": v(-20.33, 17.28) * mm, "end": v(-19.51, 17.28) * mm});
            skLineSegment(sketch, "E1658", {"start": v(-19.51, 17.28) * mm, "end": v(-18.7, 17.28) * mm});
            skLineSegment(sketch, "E1659", {"start": v(-18.7, 17.28) * mm, "end": v(-17.88, 17.28) * mm});
            skLineSegment(sketch, "E1660", {"start": v(-17.88, 17.28) * mm, "end": v(-17.07, 17.28) * mm});
            skLineSegment(sketch, "E1661", {"start": v(-17.07, 17.28) * mm, "end": v(-16.26, 17.28) * mm});
            skLineSegment(sketch, "E1662", {"start": v(-16.26, 17.28) * mm, "end": v(-15.44, 17.28) * mm});
            skLineSegment(sketch, "E1663", {"start": v(-15.44, 17.28) * mm, "end": v(-14.63, 17.28) * mm});
            skLineSegment(sketch, "E1664", {"start": v(-14.63, 17.28) * mm, "end": v(-14.63, 17.49) * mm});
            skLineSegment(sketch, "E1665", {"start": v(-14.63, 17.49) * mm, "end": v(-14.63, 17.7) * mm});
            skLineSegment(sketch, "E1666", {"start": v(-14.63, 17.7) * mm, "end": v(-14.63, 17.9) * mm});
            skLineSegment(sketch, "E1667", {"start": v(-14.63, 17.9) * mm, "end": v(-14.63, 18.1) * mm});
            skLineSegment(sketch, "E1668", {"start": v(-14.63, 18.1) * mm, "end": v(-14.63, 18.32) * mm});
            skLineSegment(sketch, "E1669", {"start": v(-14.63, 18.32) * mm, "end": v(-14.63, 18.52) * mm});
            skLineSegment(sketch, "E1670", {"start": v(-14.63, 18.52) * mm, "end": v(-14.63, 18.73) * mm});
            skLineSegment(sketch, "E1671", {"start": v(-14.63, 18.73) * mm, "end": v(-14.63, 18.94) * mm});
            skLineSegment(sketch, "E1672", {"start": v(-14.63, 18.94) * mm, "end": v(-14.63, 19.14) * mm});
            skLineSegment(sketch, "E1673", {"start": v(-14.63, 19.14) * mm, "end": v(-14.63, 19.35) * mm});
            skLineSegment(sketch, "E1674", {"start": v(-14.63, 19.35) * mm, "end": v(-14.63, 19.56) * mm});
            skLineSegment(sketch, "E1675", {"start": v(-14.63, 19.56) * mm, "end": v(-14.63, 19.76) * mm});
            skLineSegment(sketch, "E1676", {"start": v(-14.63, 19.76) * mm, "end": v(-14.63, 19.97) * mm});
            skLineSegment(sketch, "E1677", {"start": v(-14.63, 19.97) * mm, "end": v(-14.63, 20.18) * mm});
            skLineSegment(sketch, "E1678", {"start": v(-14.63, 20.18) * mm, "end": v(-14.63, 20.39) * mm});
            skLineSegment(sketch, "E1679", {"start": v(-14.63, 20.39) * mm, "end": v(-14.63, 20.6) * mm});
            skLineSegment(sketch, "E1680", {"start": v(-14.63, 20.6) * mm, "end": v(-15.14, 20.6) * mm});
            skLineSegment(sketch, "E1681", {"start": v(-15.14, 20.6) * mm, "end": v(-15.64, 20.6) * mm});
            skLineSegment(sketch, "E1682", {"start": v(-15.64, 20.6) * mm, "end": v(-16.15, 20.6) * mm});
            skLineSegment(sketch, "E1683", {"start": v(-16.15, 20.6) * mm, "end": v(-16.66, 20.6) * mm});
            skLineSegment(sketch, "E1684", {"start": v(-16.66, 20.6) * mm, "end": v(-17.17, 20.6) * mm});
            skLineSegment(sketch, "E1685", {"start": v(-17.17, 20.6) * mm, "end": v(-17.68, 20.6) * mm});
            skLineSegment(sketch, "E1686", {"start": v(-17.68, 20.6) * mm, "end": v(-18.2, 20.6) * mm});
            skLineSegment(sketch, "E1687", {"start": v(-18.2, 20.6) * mm, "end": v(-18.7, 20.6) * mm});
            skLineSegment(sketch, "E1688", {"start": v(-18.7, 20.6) * mm, "end": v(-19.2, 20.6) * mm});
            skLineSegment(sketch, "E1689", {"start": v(-19.2, 20.6) * mm, "end": v(-19.72, 20.6) * mm});
            skLineSegment(sketch, "E1690", {"start": v(-19.72, 20.6) * mm, "end": v(-20.23, 20.6) * mm});
            skLineSegment(sketch, "E1691", {"start": v(-20.23, 20.6) * mm, "end": v(-20.74, 20.6) * mm});
            skLineSegment(sketch, "E1692", {"start": v(-20.74, 20.6) * mm, "end": v(-21.24, 20.6) * mm});
            skLineSegment(sketch, "E1693", {"start": v(-21.24, 20.6) * mm, "end": v(-21.75, 20.6) * mm});
            skLineSegment(sketch, "E1694", {"start": v(-21.75, 20.6) * mm, "end": v(-22.26, 20.6) * mm});
            skLineSegment(sketch, "E1695", {"start": v(-22.26, 20.6) * mm, "end": v(-22.77, 20.6) * mm});
            skLineSegment(sketch, "E1696", {"start": v(-22.77, 20.6) * mm, "end": v(-22.33, 21.04) * mm});
            skLineSegment(sketch, "E1697", {"start": v(-22.33, 21.04) * mm, "end": v(-21.9, 21.49) * mm});
            skLineSegment(sketch, "E1698", {"start": v(-21.9, 21.49) * mm, "end": v(-21.46, 21.94) * mm});
            skLineSegment(sketch, "E1699", {"start": v(-21.46, 21.94) * mm, "end": v(-21.02, 22.38) * mm});
            skLineSegment(sketch, "E1700", {"start": v(-21.02, 22.38) * mm, "end": v(-20.58, 22.83) * mm});
            skLineSegment(sketch, "E1701", {"start": v(-20.58, 22.83) * mm, "end": v(-20.15, 23.28) * mm});
            skLineSegment(sketch, "E1702", {"start": v(-20.15, 23.28) * mm, "end": v(-19.7, 23.73) * mm});
            skLineSegment(sketch, "E1703", {"start": v(-19.7, 23.73) * mm, "end": v(-19.27, 24.17) * mm});
            skLineSegment(sketch, "E1704", {"start": v(-19.27, 24.17) * mm, "end": v(-18.83, 24.62) * mm});
            skLineSegment(sketch, "E1705", {"start": v(-18.83, 24.62) * mm, "end": v(-18.4, 25.07) * mm});
            skLineSegment(sketch, "E1706", {"start": v(-18.4, 25.07) * mm, "end": v(-17.96, 25.52) * mm});
            skLineSegment(sketch, "E1707", {"start": v(-17.96, 25.52) * mm, "end": v(-17.52, 25.97) * mm});
            skLineSegment(sketch, "E1708", {"start": v(-17.52, 25.97) * mm, "end": v(-17.08, 26.41) * mm});
            skLineSegment(sketch, "E1709", {"start": v(-17.08, 26.41) * mm, "end": v(-16.64, 26.86) * mm});
            skLineSegment(sketch, "E1710", {"start": v(-16.64, 26.86) * mm, "end": v(-16.2, 27.3) * mm});
            skLineSegment(sketch, "E1711", {"start": v(-16.2, 27.3) * mm, "end": v(-15.77, 27.76) * mm});
            skLineSegment(sketch, "E1712", {"start": v(-15.77, 27.76) * mm, "end": v(-15.64, 27.88) * mm});
            skLineSegment(sketch, "E1713", {"start": v(-15.64, 27.88) * mm, "end": v(-15.52, 28.01) * mm});
            skLineSegment(sketch, "E1714", {"start": v(-15.52, 28.01) * mm, "end": v(-15.4, 28.15) * mm});
            skLineSegment(sketch, "E1715", {"start": v(-15.4, 28.15) * mm, "end": v(-15.3, 28.29) * mm});
            skLineSegment(sketch, "E1716", {"start": v(-15.3, 28.29) * mm, "end": v(-15.2, 28.43) * mm});
            skLineSegment(sketch, "E1717", {"start": v(-15.2, 28.43) * mm, "end": v(-15.1, 28.58) * mm});
            skLineSegment(sketch, "E1718", {"start": v(-15.1, 28.58) * mm, "end": v(-15.02, 28.73) * mm});
            skLineSegment(sketch, "E1719", {"start": v(-15.02, 28.73) * mm, "end": v(-14.94, 28.9) * mm});
            skLineSegment(sketch, "E1720", {"start": v(-14.94, 28.9) * mm, "end": v(-14.87, 29.05) * mm});
            skLineSegment(sketch, "E1721", {"start": v(-14.87, 29.05) * mm, "end": v(-14.8, 29.21) * mm});
            skLineSegment(sketch, "E1722", {"start": v(-14.8, 29.21) * mm, "end": v(-14.75, 29.38) * mm});
            skLineSegment(sketch, "E1723", {"start": v(-14.75, 29.38) * mm, "end": v(-14.7, 29.55) * mm});
            skLineSegment(sketch, "E1724", {"start": v(-14.7, 29.55) * mm, "end": v(-14.67, 29.72) * mm});
            skLineSegment(sketch, "E1725", {"start": v(-14.67, 29.72) * mm, "end": v(-14.65, 29.89) * mm});
            skLineSegment(sketch, "E1726", {"start": v(-14.65, 29.89) * mm, "end": v(-14.63, 30.06) * mm});
            skLineSegment(sketch, "E1727", {"start": v(-14.63, 30.06) * mm, "end": v(-14.63, 30.24) * mm});
            skLineSegment(sketch, "E1728", {"start": v(-14.63, 30.24) * mm, "end": v(-14.63, 30.44) * mm});
            skLineSegment(sketch, "E1729", {"start": v(-14.63, 30.44) * mm, "end": v(-14.63, 30.65) * mm});
            skLineSegment(sketch, "E1730", {"start": v(-14.63, 30.65) * mm, "end": v(-14.63, 30.85) * mm});
            skLineSegment(sketch, "E1731", {"start": v(-14.63, 30.85) * mm, "end": v(-14.63, 31.05) * mm});
            skLineSegment(sketch, "E1732", {"start": v(-14.63, 31.05) * mm, "end": v(-14.63, 31.26) * mm});
            skLineSegment(sketch, "E1733", {"start": v(-14.63, 31.26) * mm, "end": v(-14.63, 31.46) * mm});
            skLineSegment(sketch, "E1734", {"start": v(-14.63, 31.46) * mm, "end": v(-14.63, 31.66) * mm});
            skLineSegment(sketch, "E1735", {"start": v(-14.63, 31.66) * mm, "end": v(-14.63, 31.87) * mm});
            skLineSegment(sketch, "E1736", {"start": v(-14.63, 31.87) * mm, "end": v(-14.63, 32.07) * mm});
            skLineSegment(sketch, "E1737", {"start": v(-14.63, 32.07) * mm, "end": v(-14.63, 32.27) * mm});
            skLineSegment(sketch, "E1738", {"start": v(-14.63, 32.27) * mm, "end": v(-14.63, 32.48) * mm});
            skLineSegment(sketch, "E1739", {"start": v(-14.63, 32.48) * mm, "end": v(-14.63, 32.68) * mm});
            skLineSegment(sketch, "E1740", {"start": v(-14.63, 32.68) * mm, "end": v(-14.63, 32.88) * mm});
            skLineSegment(sketch, "E1741", {"start": v(-14.63, 32.88) * mm, "end": v(-14.63, 33.09) * mm});
            skLineSegment(sketch, "E1742", {"start": v(-14.63, 33.09) * mm, "end": v(-14.63, 33.3) * mm});
            skLineSegment(sketch, "E1743", {"start": v(-14.63, 33.3) * mm, "end": v(-14.63, 33.5) * mm});
            skLineSegment(sketch, "E1744", {"start": v(-14.63, 33.5) * mm, "end": v(-14.64, 33.83) * mm});
            skLineSegment(sketch, "E1745", {"start": v(-14.64, 33.83) * mm, "end": v(-14.7, 34.15) * mm});
            skLineSegment(sketch, "E1746", {"start": v(-14.7, 34.15) * mm, "end": v(-14.77, 34.46) * mm});
            skLineSegment(sketch, "E1747", {"start": v(-14.77, 34.46) * mm, "end": v(-14.88, 34.76) * mm});
            skLineSegment(sketch, "E1748", {"start": v(-14.88, 34.76) * mm, "end": v(-15.02, 35.05) * mm});
            skLineSegment(sketch, "E1749", {"start": v(-15.02, 35.05) * mm, "end": v(-15.18, 35.31) * mm});
            skLineSegment(sketch, "E1750", {"start": v(-15.18, 35.31) * mm, "end": v(-15.37, 35.56) * mm});
            skLineSegment(sketch, "E1751", {"start": v(-15.37, 35.56) * mm, "end": v(-15.58, 35.8) * mm});
            skLineSegment(sketch, "E1752", {"start": v(-15.58, 35.8) * mm, "end": v(-15.81, 36) * mm});
            skLineSegment(sketch, "E1753", {"start": v(-15.81, 36) * mm, "end": v(-16.06, 36.2) * mm});
            skLineSegment(sketch, "E1754", {"start": v(-16.06, 36.2) * mm, "end": v(-16.33, 36.36) * mm});
            skLineSegment(sketch, "E1755", {"start": v(-16.33, 36.36) * mm, "end": v(-16.62, 36.5) * mm});
            skLineSegment(sketch, "E1756", {"start": v(-16.62, 36.5) * mm, "end": v(-16.92, 36.6) * mm});
            skLineSegment(sketch, "E1757", {"start": v(-16.92, 36.6) * mm, "end": v(-17.23, 36.68) * mm});
            skLineSegment(sketch, "E1758", {"start": v(-17.23, 36.68) * mm, "end": v(-17.55, 36.73) * mm});
            skLineSegment(sketch, "E1759", {"start": v(-17.55, 36.73) * mm, "end": v(-17.88, 36.75) * mm});
            skLineSegment(sketch, "E1760", {"start": v(-17.88, 36.75) * mm, "end": v(-18.32, 36.75) * mm});
            skLineSegment(sketch, "E1761", {"start": v(-18.32, 36.75) * mm, "end": v(-18.75, 36.75) * mm});
            skLineSegment(sketch, "E1762", {"start": v(-18.75, 36.75) * mm, "end": v(-19.19, 36.75) * mm});
            skLineSegment(sketch, "E1763", {"start": v(-19.19, 36.75) * mm, "end": v(-19.62, 36.75) * mm});
            skLineSegment(sketch, "E1764", {"start": v(-19.62, 36.75) * mm, "end": v(-20.06, 36.75) * mm});
            skLineSegment(sketch, "E1765", {"start": v(-20.06, 36.75) * mm, "end": v(-20.49, 36.75) * mm});
            skLineSegment(sketch, "E1766", {"start": v(-20.49, 36.75) * mm, "end": v(-20.92, 36.75) * mm});
            skLineSegment(sketch, "E1767", {"start": v(-20.92, 36.75) * mm, "end": v(-21.36, 36.75) * mm});
            skLineSegment(sketch, "E1768", {"start": v(-21.36, 36.75) * mm, "end": v(-21.8, 36.75) * mm});
            skLineSegment(sketch, "E1769", {"start": v(-21.8, 36.75) * mm, "end": v(-22.23, 36.75) * mm});
            skLineSegment(sketch, "E1770", {"start": v(-22.23, 36.75) * mm, "end": v(-22.66, 36.75) * mm});
            skLineSegment(sketch, "E1771", {"start": v(-22.66, 36.75) * mm, "end": v(-23.1, 36.75) * mm});
            skLineSegment(sketch, "E1772", {"start": v(-23.1, 36.75) * mm, "end": v(-23.53, 36.75) * mm});
            skLineSegment(sketch, "E1773", {"start": v(-23.53, 36.75) * mm, "end": v(-23.96, 36.75) * mm});
            skLineSegment(sketch, "E1774", {"start": v(-23.96, 36.75) * mm, "end": v(-24.4, 36.75) * mm});
            skLineSegment(sketch, "E1775", {"start": v(-24.4, 36.75) * mm, "end": v(-24.83, 36.75) * mm});
            skLineSegment(sketch, "E1776", {"start": v(-7.7, 21.7) * mm, "end": v(-7.7, 22.37) * mm});
            skLineSegment(sketch, "E1777", {"start": v(-7.7, 22.37) * mm, "end": v(-7.7, 23.03) * mm});
            skLineSegment(sketch, "E1778", {"start": v(-7.7, 23.03) * mm, "end": v(-7.7, 23.7) * mm});
            skLineSegment(sketch, "E1779", {"start": v(-7.7, 23.7) * mm, "end": v(-7.7, 24.36) * mm});
            skLineSegment(sketch, "E1780", {"start": v(-7.7, 24.36) * mm, "end": v(-7.7, 25.02) * mm});
            skLineSegment(sketch, "E1781", {"start": v(-7.7, 25.02) * mm, "end": v(-7.7, 25.69) * mm});
            skLineSegment(sketch, "E1782", {"start": v(-7.7, 25.69) * mm, "end": v(-7.7, 26.35) * mm});
            skLineSegment(sketch, "E1783", {"start": v(-7.7, 26.35) * mm, "end": v(-7.7, 27.01) * mm});
            skLineSegment(sketch, "E1784", {"start": v(-7.7, 27.01) * mm, "end": v(-7.7, 27.68) * mm});
            skLineSegment(sketch, "E1785", {"start": v(-7.7, 27.68) * mm, "end": v(-7.7, 28.34) * mm});
            skLineSegment(sketch, "E1786", {"start": v(-7.7, 28.34) * mm, "end": v(-7.7, 29) * mm});
            skLineSegment(sketch, "E1787", {"start": v(-7.7, 29) * mm, "end": v(-7.7, 29.67) * mm});
            skLineSegment(sketch, "E1788", {"start": v(-7.7, 29.67) * mm, "end": v(-7.7, 30.33) * mm});
            skLineSegment(sketch, "E1789", {"start": v(-7.7, 30.33) * mm, "end": v(-7.7, 31) * mm});
            skLineSegment(sketch, "E1790", {"start": v(-7.7, 31) * mm, "end": v(-7.7, 31.66) * mm});
            skLineSegment(sketch, "E1791", {"start": v(-7.7, 31.66) * mm, "end": v(-7.7, 32.32) * mm});
            skLineSegment(sketch, "E1792", {"start": v(-7.7, 32.32) * mm, "end": v(-7.7, 32.42) * mm});
            skLineSegment(sketch, "E1793", {"start": v(-7.7, 32.42) * mm, "end": v(-7.68, 32.51) * mm});
            skLineSegment(sketch, "E1794", {"start": v(-7.68, 32.51) * mm, "end": v(-7.65, 32.6) * mm});
            skLineSegment(sketch, "E1795", {"start": v(-7.65, 32.6) * mm, "end": v(-7.62, 32.7) * mm});
            skLineSegment(sketch, "E1796", {"start": v(-7.62, 32.7) * mm, "end": v(-7.58, 32.78) * mm});
            skLineSegment(sketch, "E1797", {"start": v(-7.58, 32.78) * mm, "end": v(-7.53, 32.86) * mm});
            skLineSegment(sketch, "E1798", {"start": v(-7.53, 32.86) * mm, "end": v(-7.47, 32.93) * mm});
            skLineSegment(sketch, "E1799", {"start": v(-7.47, 32.93) * mm, "end": v(-7.4, 33) * mm});
            skLineSegment(sketch, "E1800", {"start": v(-7.4, 33) * mm, "end": v(-7.34, 33.07) * mm});
            skLineSegment(sketch, "E1801", {"start": v(-7.34, 33.07) * mm, "end": v(-7.26, 33.12) * mm});
            skLineSegment(sketch, "E1802", {"start": v(-7.26, 33.12) * mm, "end": v(-7.18, 33.17) * mm});
            skLineSegment(sketch, "E1803", {"start": v(-7.18, 33.17) * mm, "end": v(-7.1, 33.22) * mm});
            skLineSegment(sketch, "E1804", {"start": v(-7.1, 33.22) * mm, "end": v(-7, 33.25) * mm});
            skLineSegment(sketch, "E1805", {"start": v(-7, 33.25) * mm, "end": v(-6.92, 33.27) * mm});
            skLineSegment(sketch, "E1806", {"start": v(-6.92, 33.27) * mm, "end": v(-6.82, 33.29) * mm});
            skLineSegment(sketch, "E1807", {"start": v(-6.82, 33.29) * mm, "end": v(-6.73, 33.3) * mm});
            skLineSegment(sketch, "E1808", {"start": v(-6.73, 33.3) * mm, "end": v(-6.43, 33.3) * mm});
            skLineSegment(sketch, "E1809", {"start": v(-6.43, 33.3) * mm, "end": v(-6.14, 33.3) * mm});
            skLineSegment(sketch, "E1810", {"start": v(-6.14, 33.3) * mm, "end": v(-5.84, 33.3) * mm});
            skLineSegment(sketch, "E1811", {"start": v(-5.84, 33.3) * mm, "end": v(-5.55, 33.3) * mm});
            skLineSegment(sketch, "E1812", {"start": v(-5.55, 33.3) * mm, "end": v(-5.25, 33.3) * mm});
            skLineSegment(sketch, "E1813", {"start": v(-5.25, 33.3) * mm, "end": v(-4.96, 33.3) * mm});
            skLineSegment(sketch, "E1814", {"start": v(-4.96, 33.3) * mm, "end": v(-4.67, 33.3) * mm});
            skLineSegment(sketch, "E1815", {"start": v(-4.67, 33.3) * mm, "end": v(-4.37, 33.3) * mm});
            skLineSegment(sketch, "E1816", {"start": v(-4.37, 33.3) * mm, "end": v(-4.08, 33.3) * mm});
            skLineSegment(sketch, "E1817", {"start": v(-4.08, 33.3) * mm, "end": v(-3.78, 33.3) * mm});
            skLineSegment(sketch, "E1818", {"start": v(-3.78, 33.3) * mm, "end": v(-3.49, 33.3) * mm});
            skLineSegment(sketch, "E1819", {"start": v(-3.49, 33.3) * mm, "end": v(-3.2, 33.3) * mm});
            skLineSegment(sketch, "E1820", {"start": v(-3.2, 33.3) * mm, "end": v(-2.9, 33.3) * mm});
            skLineSegment(sketch, "E1821", {"start": v(-2.9, 33.3) * mm, "end": v(-2.6, 33.3) * mm});
            skLineSegment(sketch, "E1822", {"start": v(-2.6, 33.3) * mm, "end": v(-2.3, 33.3) * mm});
            skLineSegment(sketch, "E1823", {"start": v(-2.3, 33.3) * mm, "end": v(-2.01, 33.3) * mm});
            skLineSegment(sketch, "E1824", {"start": v(-2.01, 33.3) * mm, "end": v(-1.91, 33.29) * mm});
            skLineSegment(sketch, "E1825", {"start": v(-1.91, 33.29) * mm, "end": v(-1.81, 33.27) * mm});
            skLineSegment(sketch, "E1826", {"start": v(-1.81, 33.27) * mm, "end": v(-1.72, 33.25) * mm});
            skLineSegment(sketch, "E1827", {"start": v(-1.72, 33.25) * mm, "end": v(-1.63, 33.22) * mm});
            skLineSegment(sketch, "E1828", {"start": v(-1.63, 33.22) * mm, "end": v(-1.55, 33.17) * mm});
            skLineSegment(sketch, "E1829", {"start": v(-1.55, 33.17) * mm, "end": v(-1.47, 33.12) * mm});
            skLineSegment(sketch, "E1830", {"start": v(-1.47, 33.12) * mm, "end": v(-1.4, 33.07) * mm});
            skLineSegment(sketch, "E1831", {"start": v(-1.4, 33.07) * mm, "end": v(-1.32, 33) * mm});
            skLineSegment(sketch, "E1832", {"start": v(-1.32, 33) * mm, "end": v(-1.26, 32.93) * mm});
            skLineSegment(sketch, "E1833", {"start": v(-1.26, 32.93) * mm, "end": v(-1.2, 32.86) * mm});
            skLineSegment(sketch, "E1834", {"start": v(-1.2, 32.86) * mm, "end": v(-1.16, 32.78) * mm});
            skLineSegment(sketch, "E1835", {"start": v(-1.16, 32.78) * mm, "end": v(-1.12, 32.7) * mm});
            skLineSegment(sketch, "E1836", {"start": v(-1.12, 32.7) * mm, "end": v(-1.08, 32.6) * mm});
            skLineSegment(sketch, "E1837", {"start": v(-1.08, 32.6) * mm, "end": v(-1.06, 32.51) * mm});
            skLineSegment(sketch, "E1838", {"start": v(-1.06, 32.51) * mm, "end": v(-1.05, 32.42) * mm});
            skLineSegment(sketch, "E1839", {"start": v(-1.05, 32.42) * mm, "end": v(-1.04, 32.32) * mm});
            skLineSegment(sketch, "E1840", {"start": v(-1.04, 32.32) * mm, "end": v(-1.04, 31.66) * mm});
            skLineSegment(sketch, "E1841", {"start": v(-1.04, 31.66) * mm, "end": v(-1.04, 31) * mm});
            skLineSegment(sketch, "E1842", {"start": v(-1.04, 31) * mm, "end": v(-1.04, 30.33) * mm});
            skLineSegment(sketch, "E1843", {"start": v(-1.04, 30.33) * mm, "end": v(-1.04, 29.67) * mm});
            skLineSegment(sketch, "E1844", {"start": v(-1.04, 29.67) * mm, "end": v(-1.04, 29) * mm});
            skLineSegment(sketch, "E1845", {"start": v(-1.04, 29) * mm, "end": v(-1.04, 28.34) * mm});
            skLineSegment(sketch, "E1846", {"start": v(-1.04, 28.34) * mm, "end": v(-1.04, 27.68) * mm});
            skLineSegment(sketch, "E1847", {"start": v(-1.04, 27.68) * mm, "end": v(-1.04, 27.01) * mm});
            skLineSegment(sketch, "E1848", {"start": v(-1.04, 27.01) * mm, "end": v(-1.04, 26.35) * mm});
            skLineSegment(sketch, "E1849", {"start": v(-1.04, 26.35) * mm, "end": v(-1.04, 25.69) * mm});
            skLineSegment(sketch, "E1850", {"start": v(-1.04, 25.69) * mm, "end": v(-1.04, 25.02) * mm});
            skLineSegment(sketch, "E1851", {"start": v(-1.04, 25.02) * mm, "end": v(-1.04, 24.36) * mm});
            skLineSegment(sketch, "E1852", {"start": v(-1.04, 24.36) * mm, "end": v(-1.04, 23.7) * mm});
            skLineSegment(sketch, "E1853", {"start": v(-1.04, 23.7) * mm, "end": v(-1.04, 23.03) * mm});
            skLineSegment(sketch, "E1854", {"start": v(-1.04, 23.03) * mm, "end": v(-1.04, 22.37) * mm});
            skLineSegment(sketch, "E1855", {"start": v(-1.04, 22.37) * mm, "end": v(-1.04, 21.7) * mm});
            skLineSegment(sketch, "E1856", {"start": v(-1.04, 21.7) * mm, "end": v(-1.05, 21.6) * mm});
            skLineSegment(sketch, "E1857", {"start": v(-1.05, 21.6) * mm, "end": v(-1.06, 21.5) * mm});
            skLineSegment(sketch, "E1858", {"start": v(-1.06, 21.5) * mm, "end": v(-1.08, 21.41) * mm});
            skLineSegment(sketch, "E1859", {"start": v(-1.08, 21.41) * mm, "end": v(-1.12, 21.33) * mm});
            skLineSegment(sketch, "E1860", {"start": v(-1.12, 21.33) * mm, "end": v(-1.16, 21.24) * mm});
            skLineSegment(sketch, "E1861", {"start": v(-1.16, 21.24) * mm, "end": v(-1.2, 21.16) * mm});
            skLineSegment(sketch, "E1862", {"start": v(-1.2, 21.16) * mm, "end": v(-1.26, 21.09) * mm});
            skLineSegment(sketch, "E1863", {"start": v(-1.26, 21.09) * mm, "end": v(-1.32, 21.02) * mm});
            skLineSegment(sketch, "E1864", {"start": v(-1.32, 21.02) * mm, "end": v(-1.4, 20.95) * mm});
            skLineSegment(sketch, "E1865", {"start": v(-1.4, 20.95) * mm, "end": v(-1.47, 20.9) * mm});
            skLineSegment(sketch, "E1866", {"start": v(-1.47, 20.9) * mm, "end": v(-1.55, 20.85) * mm});
            skLineSegment(sketch, "E1867", {"start": v(-1.55, 20.85) * mm, "end": v(-1.63, 20.81) * mm});
            skLineSegment(sketch, "E1868", {"start": v(-1.63, 20.81) * mm, "end": v(-1.72, 20.78) * mm});
            skLineSegment(sketch, "E1869", {"start": v(-1.72, 20.78) * mm, "end": v(-1.81, 20.75) * mm});
            skLineSegment(sketch, "E1870", {"start": v(-1.81, 20.75) * mm, "end": v(-1.91, 20.74) * mm});
            skLineSegment(sketch, "E1871", {"start": v(-1.91, 20.74) * mm, "end": v(-2.01, 20.74) * mm});
            skLineSegment(sketch, "E1872", {"start": v(-2.01, 20.74) * mm, "end": v(-2.3, 20.74) * mm});
            skLineSegment(sketch, "E1873", {"start": v(-2.3, 20.74) * mm, "end": v(-2.6, 20.74) * mm});
            skLineSegment(sketch, "E1874", {"start": v(-2.6, 20.74) * mm, "end": v(-2.9, 20.74) * mm});
            skLineSegment(sketch, "E1875", {"start": v(-2.9, 20.74) * mm, "end": v(-3.2, 20.74) * mm});
            skLineSegment(sketch, "E1876", {"start": v(-3.2, 20.74) * mm, "end": v(-3.49, 20.74) * mm});
            skLineSegment(sketch, "E1877", {"start": v(-3.49, 20.74) * mm, "end": v(-3.78, 20.74) * mm});
            skLineSegment(sketch, "E1878", {"start": v(-3.78, 20.74) * mm, "end": v(-4.08, 20.74) * mm});
            skLineSegment(sketch, "E1879", {"start": v(-4.08, 20.74) * mm, "end": v(-4.37, 20.74) * mm});
            skLineSegment(sketch, "E1880", {"start": v(-4.37, 20.74) * mm, "end": v(-4.67, 20.74) * mm});
            skLineSegment(sketch, "E1881", {"start": v(-4.67, 20.74) * mm, "end": v(-4.96, 20.74) * mm});
            skLineSegment(sketch, "E1882", {"start": v(-4.96, 20.74) * mm, "end": v(-5.25, 20.74) * mm});
            skLineSegment(sketch, "E1883", {"start": v(-5.25, 20.74) * mm, "end": v(-5.55, 20.74) * mm});
            skLineSegment(sketch, "E1884", {"start": v(-5.55, 20.74) * mm, "end": v(-5.84, 20.74) * mm});
            skLineSegment(sketch, "E1885", {"start": v(-5.84, 20.74) * mm, "end": v(-6.14, 20.74) * mm});
            skLineSegment(sketch, "E1886", {"start": v(-6.14, 20.74) * mm, "end": v(-6.43, 20.74) * mm});
            skLineSegment(sketch, "E1887", {"start": v(-6.43, 20.74) * mm, "end": v(-6.73, 20.74) * mm});
            skLineSegment(sketch, "E1888", {"start": v(-6.73, 20.74) * mm, "end": v(-6.82, 20.74) * mm});
            skLineSegment(sketch, "E1889", {"start": v(-6.82, 20.74) * mm, "end": v(-6.92, 20.75) * mm});
            skLineSegment(sketch, "E1890", {"start": v(-6.92, 20.75) * mm, "end": v(-7, 20.78) * mm});
            skLineSegment(sketch, "E1891", {"start": v(-7, 20.78) * mm, "end": v(-7.1, 20.81) * mm});
            skLineSegment(sketch, "E1892", {"start": v(-7.1, 20.81) * mm, "end": v(-7.18, 20.85) * mm});
            skLineSegment(sketch, "E1893", {"start": v(-7.18, 20.85) * mm, "end": v(-7.26, 20.9) * mm});
            skLineSegment(sketch, "E1894", {"start": v(-7.26, 20.9) * mm, "end": v(-7.34, 20.95) * mm});
            skLineSegment(sketch, "E1895", {"start": v(-7.34, 20.95) * mm, "end": v(-7.4, 21.02) * mm});
            skLineSegment(sketch, "E1896", {"start": v(-7.4, 21.02) * mm, "end": v(-7.47, 21.09) * mm});
            skLineSegment(sketch, "E1897", {"start": v(-7.47, 21.09) * mm, "end": v(-7.53, 21.16) * mm});
            skLineSegment(sketch, "E1898", {"start": v(-7.53, 21.16) * mm, "end": v(-7.58, 21.24) * mm});
            skLineSegment(sketch, "E1899", {"start": v(-7.58, 21.24) * mm, "end": v(-7.62, 21.33) * mm});
            skLineSegment(sketch, "E1900", {"start": v(-7.62, 21.33) * mm, "end": v(-7.65, 21.41) * mm});
            skLineSegment(sketch, "E1901", {"start": v(-7.65, 21.41) * mm, "end": v(-7.68, 21.5) * mm});
            skLineSegment(sketch, "E1902", {"start": v(-7.68, 21.5) * mm, "end": v(-7.7, 21.6) * mm});
            skLineSegment(sketch, "E1903", {"start": v(-7.7, 21.6) * mm, "end": v(-7.7, 21.7) * mm});
            skLineSegment(sketch, "E1904", {"start": v(-8.22, 36.75) * mm, "end": v(-8.55, 36.73) * mm});
            skLineSegment(sketch, "E1905", {"start": v(-8.55, 36.73) * mm, "end": v(-8.87, 36.68) * mm});
            skLineSegment(sketch, "E1906", {"start": v(-8.87, 36.68) * mm, "end": v(-9.18, 36.6) * mm});
            skLineSegment(sketch, "E1907", {"start": v(-9.18, 36.6) * mm, "end": v(-9.48, 36.5) * mm});
            skLineSegment(sketch, "E1908", {"start": v(-9.48, 36.5) * mm, "end": v(-9.77, 36.36) * mm});
            skLineSegment(sketch, "E1909", {"start": v(-9.77, 36.36) * mm, "end": v(-10.04, 36.2) * mm});
            skLineSegment(sketch, "E1910", {"start": v(-10.04, 36.2) * mm, "end": v(-10.29, 36) * mm});
            skLineSegment(sketch, "E1911", {"start": v(-10.29, 36) * mm, "end": v(-10.52, 35.8) * mm});
            skLineSegment(sketch, "E1912", {"start": v(-10.52, 35.8) * mm, "end": v(-10.73, 35.56) * mm});
            skLineSegment(sketch, "E1913", {"start": v(-10.73, 35.56) * mm, "end": v(-10.92, 35.31) * mm});
            skLineSegment(sketch, "E1914", {"start": v(-10.92, 35.31) * mm, "end": v(-11.08, 35.05) * mm});
            skLineSegment(sketch, "E1915", {"start": v(-11.08, 35.05) * mm, "end": v(-11.22, 34.76) * mm});
            skLineSegment(sketch, "E1916", {"start": v(-11.22, 34.76) * mm, "end": v(-11.33, 34.46) * mm});
            skLineSegment(sketch, "E1917", {"start": v(-11.33, 34.46) * mm, "end": v(-11.4, 34.15) * mm});
            skLineSegment(sketch, "E1918", {"start": v(-11.4, 34.15) * mm, "end": v(-11.46, 33.83) * mm});
            skLineSegment(sketch, "E1919", {"start": v(-11.46, 33.83) * mm, "end": v(-11.47, 33.5) * mm});
            skLineSegment(sketch, "E1920", {"start": v(-11.47, 33.5) * mm, "end": v(-11.47, 32.68) * mm});
            skLineSegment(sketch, "E1921", {"start": v(-11.47, 32.68) * mm, "end": v(-11.47, 31.87) * mm});
            skLineSegment(sketch, "E1922", {"start": v(-11.47, 31.87) * mm, "end": v(-11.47, 31.06) * mm});
            skLineSegment(sketch, "E1923", {"start": v(-11.47, 31.06) * mm, "end": v(-11.47, 30.25) * mm});
            skLineSegment(sketch, "E1924", {"start": v(-11.47, 30.25) * mm, "end": v(-11.47, 29.44) * mm});
            skLineSegment(sketch, "E1925", {"start": v(-11.47, 29.44) * mm, "end": v(-11.47, 28.62) * mm});
            skLineSegment(sketch, "E1926", {"start": v(-11.47, 28.62) * mm, "end": v(-11.47, 27.81) * mm});
            skLineSegment(sketch, "E1927", {"start": v(-11.47, 27.81) * mm, "end": v(-11.47, 27) * mm});
            skLineSegment(sketch, "E1928", {"start": v(-11.47, 27) * mm, "end": v(-11.47, 26.19) * mm});
            skLineSegment(sketch, "E1929", {"start": v(-11.47, 26.19) * mm, "end": v(-11.47, 25.38) * mm});
            skLineSegment(sketch, "E1930", {"start": v(-11.47, 25.38) * mm, "end": v(-11.47, 24.57) * mm});
            skLineSegment(sketch, "E1931", {"start": v(-11.47, 24.57) * mm, "end": v(-11.47, 23.75) * mm});
            skLineSegment(sketch, "E1932", {"start": v(-11.47, 23.75) * mm, "end": v(-11.47, 22.94) * mm});
            skLineSegment(sketch, "E1933", {"start": v(-11.47, 22.94) * mm, "end": v(-11.47, 22.13) * mm});
            skLineSegment(sketch, "E1934", {"start": v(-11.47, 22.13) * mm, "end": v(-11.47, 21.32) * mm});
            skLineSegment(sketch, "E1935", {"start": v(-11.47, 21.32) * mm, "end": v(-11.47, 20.5) * mm});
            skLineSegment(sketch, "E1936", {"start": v(-11.47, 20.5) * mm, "end": v(-11.46, 20.17) * mm});
            skLineSegment(sketch, "E1937", {"start": v(-11.46, 20.17) * mm, "end": v(-11.4, 19.85) * mm});
            skLineSegment(sketch, "E1938", {"start": v(-11.4, 19.85) * mm, "end": v(-11.33, 19.54) * mm});
            skLineSegment(sketch, "E1939", {"start": v(-11.33, 19.54) * mm, "end": v(-11.22, 19.24) * mm});
            skLineSegment(sketch, "E1940", {"start": v(-11.22, 19.24) * mm, "end": v(-11.08, 18.96) * mm});
            skLineSegment(sketch, "E1941", {"start": v(-11.08, 18.96) * mm, "end": v(-10.92, 18.7) * mm});
            skLineSegment(sketch, "E1942", {"start": v(-10.92, 18.7) * mm, "end": v(-10.73, 18.45) * mm});
            skLineSegment(sketch, "E1943", {"start": v(-10.73, 18.45) * mm, "end": v(-10.52, 18.22) * mm});
            skLineSegment(sketch, "E1944", {"start": v(-10.52, 18.22) * mm, "end": v(-10.29, 18.01) * mm});
            skLineSegment(sketch, "E1945", {"start": v(-10.29, 18.01) * mm, "end": v(-10.04, 17.83) * mm});
            skLineSegment(sketch, "E1946", {"start": v(-10.04, 17.83) * mm, "end": v(-9.77, 17.67) * mm});
            skLineSegment(sketch, "E1947", {"start": v(-9.77, 17.67) * mm, "end": v(-9.48, 17.53) * mm});
            skLineSegment(sketch, "E1948", {"start": v(-9.48, 17.53) * mm, "end": v(-9.18, 17.42) * mm});
            skLineSegment(sketch, "E1949", {"start": v(-9.18, 17.42) * mm, "end": v(-8.87, 17.35) * mm});
            skLineSegment(sketch, "E1950", {"start": v(-8.87, 17.35) * mm, "end": v(-8.55, 17.3) * mm});
            skLineSegment(sketch, "E1951", {"start": v(-8.55, 17.3) * mm, "end": v(-8.22, 17.28) * mm});
            skLineSegment(sketch, "E1952", {"start": v(-8.22, 17.28) * mm, "end": v(-7.73, 17.28) * mm});
            skLineSegment(sketch, "E1953", {"start": v(-7.73, 17.28) * mm, "end": v(-7.25, 17.28) * mm});
            skLineSegment(sketch, "E1954", {"start": v(-7.25, 17.28) * mm, "end": v(-6.77, 17.28) * mm});
            skLineSegment(sketch, "E1955", {"start": v(-6.77, 17.28) * mm, "end": v(-6.29, 17.28) * mm});
            skLineSegment(sketch, "E1956", {"start": v(-6.29, 17.28) * mm, "end": v(-5.8, 17.28) * mm});
            skLineSegment(sketch, "E1957", {"start": v(-5.8, 17.28) * mm, "end": v(-5.32, 17.28) * mm});
            skLineSegment(sketch, "E1958", {"start": v(-5.32, 17.28) * mm, "end": v(-4.84, 17.28) * mm});
            skLineSegment(sketch, "E1959", {"start": v(-4.84, 17.28) * mm, "end": v(-4.36, 17.28) * mm});
            skLineSegment(sketch, "E1960", {"start": v(-4.36, 17.28) * mm, "end": v(-3.87, 17.28) * mm});
            skLineSegment(sketch, "E1961", {"start": v(-3.87, 17.28) * mm, "end": v(-3.4, 17.28) * mm});
            skLineSegment(sketch, "E1962", {"start": v(-3.4, 17.28) * mm, "end": v(-2.91, 17.28) * mm});
            skLineSegment(sketch, "E1963", {"start": v(-2.91, 17.28) * mm, "end": v(-2.43, 17.28) * mm});
            skLineSegment(sketch, "E1964", {"start": v(-2.43, 17.28) * mm, "end": v(-1.95, 17.28) * mm});
            skLineSegment(sketch, "E1965", {"start": v(-1.95, 17.28) * mm, "end": v(-1.46, 17.28) * mm});
            skLineSegment(sketch, "E1966", {"start": v(-1.46, 17.28) * mm, "end": v(-0.98, 17.28) * mm});
            skLineSegment(sketch, "E1967", {"start": v(-0.98, 17.28) * mm, "end": v(-0.5, 17.28) * mm});
            skLineSegment(sketch, "E1968", {"start": v(-0.5, 17.28) * mm, "end": v(-0.17, 17.3) * mm});
            skLineSegment(sketch, "E1969", {"start": v(-0.17, 17.3) * mm, "end": v(0.15, 17.35) * mm});
            skLineSegment(sketch, "E1970", {"start": v(0.15, 17.35) * mm, "end": v(0.46, 17.42) * mm});
            skLineSegment(sketch, "E1971", {"start": v(0.46, 17.42) * mm, "end": v(0.75, 17.53) * mm});
            skLineSegment(sketch, "E1972", {"start": v(0.75, 17.53) * mm, "end": v(1.04, 17.67) * mm});
            skLineSegment(sketch, "E1973", {"start": v(1.04, 17.67) * mm, "end": v(1.3, 17.83) * mm});
            skLineSegment(sketch, "E1974", {"start": v(1.3, 17.83) * mm, "end": v(1.55, 18.01) * mm});
            skLineSegment(sketch, "E1975", {"start": v(1.55, 18.01) * mm, "end": v(1.78, 18.22) * mm});
            skLineSegment(sketch, "E1976", {"start": v(1.78, 18.22) * mm, "end": v(2, 18.45) * mm});
            skLineSegment(sketch, "E1977", {"start": v(2, 18.45) * mm, "end": v(2.18, 18.7) * mm});
            skLineSegment(sketch, "E1978", {"start": v(2.18, 18.7) * mm, "end": v(2.34, 18.96) * mm});
            skLineSegment(sketch, "E1979", {"start": v(2.34, 18.96) * mm, "end": v(2.48, 19.24) * mm});
            skLineSegment(sketch, "E1980", {"start": v(2.48, 19.24) * mm, "end": v(2.58, 19.54) * mm});
            skLineSegment(sketch, "E1981", {"start": v(2.58, 19.54) * mm, "end": v(2.67, 19.85) * mm});
            skLineSegment(sketch, "E1982", {"start": v(2.67, 19.85) * mm, "end": v(2.71, 20.17) * mm});
            skLineSegment(sketch, "E1983", {"start": v(2.71, 20.17) * mm, "end": v(2.73, 20.5) * mm});
            skLineSegment(sketch, "E1984", {"start": v(2.73, 20.5) * mm, "end": v(2.73, 21.32) * mm});
            skLineSegment(sketch, "E1985", {"start": v(2.73, 21.32) * mm, "end": v(2.73, 22.13) * mm});
            skLineSegment(sketch, "E1986", {"start": v(2.73, 22.13) * mm, "end": v(2.73, 22.94) * mm});
            skLineSegment(sketch, "E1987", {"start": v(2.73, 22.94) * mm, "end": v(2.73, 23.75) * mm});
            skLineSegment(sketch, "E1988", {"start": v(2.73, 23.75) * mm, "end": v(2.73, 24.57) * mm});
            skLineSegment(sketch, "E1989", {"start": v(2.73, 24.57) * mm, "end": v(2.73, 25.38) * mm});
            skLineSegment(sketch, "E1990", {"start": v(2.73, 25.38) * mm, "end": v(2.73, 26.19) * mm});
            skLineSegment(sketch, "E1991", {"start": v(2.73, 26.19) * mm, "end": v(2.73, 27) * mm});
            skLineSegment(sketch, "E1992", {"start": v(2.73, 27) * mm, "end": v(2.73, 27.81) * mm});
            skLineSegment(sketch, "E1993", {"start": v(2.73, 27.81) * mm, "end": v(2.73, 28.62) * mm});
            skLineSegment(sketch, "E1994", {"start": v(2.73, 28.62) * mm, "end": v(2.73, 29.44) * mm});
            skLineSegment(sketch, "E1995", {"start": v(2.73, 29.44) * mm, "end": v(2.73, 30.25) * mm});
            skLineSegment(sketch, "E1996", {"start": v(2.73, 30.25) * mm, "end": v(2.73, 31.06) * mm});
            skLineSegment(sketch, "E1997", {"start": v(2.73, 31.06) * mm, "end": v(2.73, 31.87) * mm});
            skLineSegment(sketch, "E1998", {"start": v(2.73, 31.87) * mm, "end": v(2.73, 32.68) * mm});
            skLineSegment(sketch, "E1999", {"start": v(2.73, 32.68) * mm, "end": v(2.73, 33.5) * mm});
            skLineSegment(sketch, "E2000", {"start": v(2.73, 33.5) * mm, "end": v(2.71, 33.83) * mm});
            skLineSegment(sketch, "E2001", {"start": v(2.71, 33.83) * mm, "end": v(2.67, 34.15) * mm});
            skLineSegment(sketch, "E2002", {"start": v(2.67, 34.15) * mm, "end": v(2.58, 34.46) * mm});
            skLineSegment(sketch, "E2003", {"start": v(2.58, 34.46) * mm, "end": v(2.48, 34.76) * mm});
            skLineSegment(sketch, "E2004", {"start": v(2.48, 34.76) * mm, "end": v(2.34, 35.05) * mm});
            skLineSegment(sketch, "E2005", {"start": v(2.34, 35.05) * mm, "end": v(2.18, 35.31) * mm});
            skLineSegment(sketch, "E2006", {"start": v(2.18, 35.31) * mm, "end": v(2, 35.56) * mm});
            skLineSegment(sketch, "E2007", {"start": v(2, 35.56) * mm, "end": v(1.78, 35.8) * mm});
            skLineSegment(sketch, "E2008", {"start": v(1.78, 35.8) * mm, "end": v(1.55, 36) * mm});
            skLineSegment(sketch, "E2009", {"start": v(1.55, 36) * mm, "end": v(1.3, 36.2) * mm});
            skLineSegment(sketch, "E2010", {"start": v(1.3, 36.2) * mm, "end": v(1.04, 36.36) * mm});
            skLineSegment(sketch, "E2011", {"start": v(1.04, 36.36) * mm, "end": v(0.75, 36.5) * mm});
            skLineSegment(sketch, "E2012", {"start": v(0.75, 36.5) * mm, "end": v(0.46, 36.6) * mm});
            skLineSegment(sketch, "E2013", {"start": v(0.46, 36.6) * mm, "end": v(0.15, 36.68) * mm});
            skLineSegment(sketch, "E2014", {"start": v(0.15, 36.68) * mm, "end": v(-0.17, 36.73) * mm});
            skLineSegment(sketch, "E2015", {"start": v(-0.17, 36.73) * mm, "end": v(-0.5, 36.75) * mm});
            skLineSegment(sketch, "E2016", {"start": v(-0.5, 36.75) * mm, "end": v(-0.98, 36.75) * mm});
            skLineSegment(sketch, "E2017", {"start": v(-0.98, 36.75) * mm, "end": v(-1.46, 36.75) * mm});
            skLineSegment(sketch, "E2018", {"start": v(-1.46, 36.75) * mm, "end": v(-1.95, 36.75) * mm});
            skLineSegment(sketch, "E2019", {"start": v(-1.95, 36.75) * mm, "end": v(-2.43, 36.75) * mm});
            skLineSegment(sketch, "E2020", {"start": v(-2.43, 36.75) * mm, "end": v(-2.91, 36.75) * mm});
            skLineSegment(sketch, "E2021", {"start": v(-2.91, 36.75) * mm, "end": v(-3.4, 36.75) * mm});
            skLineSegment(sketch, "E2022", {"start": v(-3.4, 36.75) * mm, "end": v(-3.87, 36.75) * mm});
            skLineSegment(sketch, "E2023", {"start": v(-3.87, 36.75) * mm, "end": v(-4.36, 36.75) * mm});
            skLineSegment(sketch, "E2024", {"start": v(-4.36, 36.75) * mm, "end": v(-4.84, 36.75) * mm});
            skLineSegment(sketch, "E2025", {"start": v(-4.84, 36.75) * mm, "end": v(-5.32, 36.75) * mm});
            skLineSegment(sketch, "E2026", {"start": v(-5.32, 36.75) * mm, "end": v(-5.8, 36.75) * mm});
            skLineSegment(sketch, "E2027", {"start": v(-5.8, 36.75) * mm, "end": v(-6.29, 36.75) * mm});
            skLineSegment(sketch, "E2028", {"start": v(-6.29, 36.75) * mm, "end": v(-6.77, 36.75) * mm});
            skLineSegment(sketch, "E2029", {"start": v(-6.77, 36.75) * mm, "end": v(-7.25, 36.75) * mm});
            skLineSegment(sketch, "E2030", {"start": v(-7.25, 36.75) * mm, "end": v(-7.73, 36.75) * mm});
            skLineSegment(sketch, "E2031", {"start": v(-7.73, 36.75) * mm, "end": v(-8.22, 36.75) * mm});
            skLineSegment(sketch, "E2032", {"start": v(4.74, 36.75) * mm, "end": v(4.74, 36.53) * mm});
            skLineSegment(sketch, "E2033", {"start": v(4.74, 36.53) * mm, "end": v(4.74, 36.32) * mm});
            skLineSegment(sketch, "E2034", {"start": v(4.74, 36.32) * mm, "end": v(4.74, 36.1) * mm});
            skLineSegment(sketch, "E2035", {"start": v(4.74, 36.1) * mm, "end": v(4.74, 35.9) * mm});
            skLineSegment(sketch, "E2036", {"start": v(4.74, 35.9) * mm, "end": v(4.74, 35.68) * mm});
            skLineSegment(sketch, "E2037", {"start": v(4.74, 35.68) * mm, "end": v(4.74, 35.46) * mm});
            skLineSegment(sketch, "E2038", {"start": v(4.74, 35.46) * mm, "end": v(4.74, 35.25) * mm});
            skLineSegment(sketch, "E2039", {"start": v(4.74, 35.25) * mm, "end": v(4.74, 35.04) * mm});
            skLineSegment(sketch, "E2040", {"start": v(4.74, 35.04) * mm, "end": v(4.74, 34.82) * mm});
            skLineSegment(sketch, "E2041", {"start": v(4.74, 34.82) * mm, "end": v(4.74, 34.6) * mm});
            skLineSegment(sketch, "E2042", {"start": v(4.74, 34.6) * mm, "end": v(4.74, 34.4) * mm});
            skLineSegment(sketch, "E2043", {"start": v(4.74, 34.4) * mm, "end": v(4.74, 34.18) * mm});
            skLineSegment(sketch, "E2044", {"start": v(4.74, 34.18) * mm, "end": v(4.74, 33.96) * mm});
            skLineSegment(sketch, "E2045", {"start": v(4.74, 33.96) * mm, "end": v(4.74, 33.75) * mm});
            skLineSegment(sketch, "E2046", {"start": v(4.74, 33.75) * mm, "end": v(4.74, 33.54) * mm});
            skLineSegment(sketch, "E2047", {"start": v(4.74, 33.54) * mm, "end": v(4.74, 33.32) * mm});
            skLineSegment(sketch, "E2048", {"start": v(4.74, 33.32) * mm, "end": v(4.93, 33.32) * mm});
            skLineSegment(sketch, "E2049", {"start": v(4.93, 33.32) * mm, "end": v(5.12, 33.32) * mm});
            skLineSegment(sketch, "E2050", {"start": v(5.12, 33.32) * mm, "end": v(5.3, 33.32) * mm});
            skLineSegment(sketch, "E2051", {"start": v(5.3, 33.32) * mm, "end": v(5.5, 33.32) * mm});
            skLineSegment(sketch, "E2052", {"start": v(5.5, 33.32) * mm, "end": v(5.68, 33.32) * mm});
            skLineSegment(sketch, "E2053", {"start": v(5.68, 33.32) * mm, "end": v(5.87, 33.32) * mm});
            skLineSegment(sketch, "E2054", {"start": v(5.87, 33.32) * mm, "end": v(6.05, 33.32) * mm});
            skLineSegment(sketch, "E2055", {"start": v(6.05, 33.32) * mm, "end": v(6.24, 33.32) * mm});
            skLineSegment(sketch, "E2056", {"start": v(6.24, 33.32) * mm, "end": v(6.43, 33.32) * mm});
            skLineSegment(sketch, "E2057", {"start": v(6.43, 33.32) * mm, "end": v(6.62, 33.32) * mm});
            skLineSegment(sketch, "E2058", {"start": v(6.62, 33.32) * mm, "end": v(6.8, 33.32) * mm});
            skLineSegment(sketch, "E2059", {"start": v(6.8, 33.32) * mm, "end": v(7, 33.32) * mm});
            skLineSegment(sketch, "E2060", {"start": v(7, 33.32) * mm, "end": v(7.18, 33.32) * mm});
            skLineSegment(sketch, "E2061", {"start": v(7.18, 33.32) * mm, "end": v(7.37, 33.32) * mm});
            skLineSegment(sketch, "E2062", {"start": v(7.37, 33.32) * mm, "end": v(7.55, 33.32) * mm});
            skLineSegment(sketch, "E2063", {"start": v(7.55, 33.32) * mm, "end": v(7.74, 33.32) * mm});
            skLineSegment(sketch, "E2064", {"start": v(7.74, 33.32) * mm, "end": v(7.74, 32.32) * mm});
            skLineSegment(sketch, "E2065", {"start": v(7.74, 32.32) * mm, "end": v(7.74, 31.32) * mm});
            skLineSegment(sketch, "E2066", {"start": v(7.74, 31.32) * mm, "end": v(7.74, 30.31) * mm});
            skLineSegment(sketch, "E2067", {"start": v(7.74, 30.31) * mm, "end": v(7.74, 29.31) * mm});
            skLineSegment(sketch, "E2068", {"start": v(7.74, 29.31) * mm, "end": v(7.74, 28.3) * mm});
            skLineSegment(sketch, "E2069", {"start": v(7.74, 28.3) * mm, "end": v(7.74, 27.3) * mm});
            skLineSegment(sketch, "E2070", {"start": v(7.74, 27.3) * mm, "end": v(7.74, 26.3) * mm});
            skLineSegment(sketch, "E2071", {"start": v(7.74, 26.3) * mm, "end": v(7.74, 25.3) * mm});
            skLineSegment(sketch, "E2072", {"start": v(7.74, 25.3) * mm, "end": v(7.74, 24.3) * mm});
            skLineSegment(sketch, "E2073", {"start": v(7.74, 24.3) * mm, "end": v(7.74, 23.3) * mm});
            skLineSegment(sketch, "E2074", {"start": v(7.74, 23.3) * mm, "end": v(7.74, 22.3) * mm});
            skLineSegment(sketch, "E2075", {"start": v(7.74, 22.3) * mm, "end": v(7.74, 21.3) * mm});
            skLineSegment(sketch, "E2076", {"start": v(7.74, 21.3) * mm, "end": v(7.74, 20.29) * mm});
            skLineSegment(sketch, "E2077", {"start": v(7.74, 20.29) * mm, "end": v(7.74, 19.29) * mm});
            skLineSegment(sketch, "E2078", {"start": v(7.74, 19.29) * mm, "end": v(7.74, 18.28) * mm});
            skLineSegment(sketch, "E2079", {"start": v(7.74, 18.28) * mm, "end": v(7.74, 17.28) * mm});
            skLineSegment(sketch, "E2080", {"start": v(7.74, 17.28) * mm, "end": v(7.98, 17.28) * mm});
            skLineSegment(sketch, "E2081", {"start": v(7.98, 17.28) * mm, "end": v(8.21, 17.28) * mm});
            skLineSegment(sketch, "E2082", {"start": v(8.21, 17.28) * mm, "end": v(8.45, 17.28) * mm});
            skLineSegment(sketch, "E2083", {"start": v(8.45, 17.28) * mm, "end": v(8.69, 17.28) * mm});
            skLineSegment(sketch, "E2084", {"start": v(8.69, 17.28) * mm, "end": v(8.92, 17.28) * mm});
            skLineSegment(sketch, "E2085", {"start": v(8.92, 17.28) * mm, "end": v(9.16, 17.28) * mm});
            skLineSegment(sketch, "E2086", {"start": v(9.16, 17.28) * mm, "end": v(9.4, 17.28) * mm});
            skLineSegment(sketch, "E2087", {"start": v(9.4, 17.28) * mm, "end": v(9.63, 17.28) * mm});
            skLineSegment(sketch, "E2088", {"start": v(9.63, 17.28) * mm, "end": v(9.86, 17.28) * mm});
            skLineSegment(sketch, "E2089", {"start": v(9.86, 17.28) * mm, "end": v(10.1, 17.28) * mm});
            skLineSegment(sketch, "E2090", {"start": v(10.1, 17.28) * mm, "end": v(10.34, 17.28) * mm});
            skLineSegment(sketch, "E2091", {"start": v(10.34, 17.28) * mm, "end": v(10.57, 17.28) * mm});
            skLineSegment(sketch, "E2092", {"start": v(10.57, 17.28) * mm, "end": v(10.8, 17.28) * mm});
            skLineSegment(sketch, "E2093", {"start": v(10.8, 17.28) * mm, "end": v(11.04, 17.28) * mm});
            skLineSegment(sketch, "E2094", {"start": v(11.04, 17.28) * mm, "end": v(11.28, 17.28) * mm});
            skLineSegment(sketch, "E2095", {"start": v(11.28, 17.28) * mm, "end": v(11.52, 17.28) * mm});
            skLineSegment(sketch, "E2096", {"start": v(11.52, 17.28) * mm, "end": v(11.52, 18.5) * mm});
            skLineSegment(sketch, "E2097", {"start": v(11.52, 18.5) * mm, "end": v(11.52, 19.71) * mm});
            skLineSegment(sketch, "E2098", {"start": v(11.52, 19.71) * mm, "end": v(11.52, 20.93) * mm});
            skLineSegment(sketch, "E2099", {"start": v(11.52, 20.93) * mm, "end": v(11.52, 22.15) * mm});
            skLineSegment(sketch, "E2100", {"start": v(11.52, 22.15) * mm, "end": v(11.52, 23.36) * mm});
            skLineSegment(sketch, "E2101", {"start": v(11.52, 23.36) * mm, "end": v(11.52, 24.58) * mm});
            skLineSegment(sketch, "E2102", {"start": v(11.52, 24.58) * mm, "end": v(11.52, 25.8) * mm});
            skLineSegment(sketch, "E2103", {"start": v(11.52, 25.8) * mm, "end": v(11.52, 27.01) * mm});
            skLineSegment(sketch, "E2104", {"start": v(11.52, 27.01) * mm, "end": v(11.52, 28.23) * mm});
            skLineSegment(sketch, "E2105", {"start": v(11.52, 28.23) * mm, "end": v(11.52, 29.45) * mm});
            skLineSegment(sketch, "E2106", {"start": v(11.52, 29.45) * mm, "end": v(11.52, 30.66) * mm});
            skLineSegment(sketch, "E2107", {"start": v(11.52, 30.66) * mm, "end": v(11.52, 31.88) * mm});
            skLineSegment(sketch, "E2108", {"start": v(11.52, 31.88) * mm, "end": v(11.52, 33.1) * mm});
            skLineSegment(sketch, "E2109", {"start": v(11.52, 33.1) * mm, "end": v(11.52, 34.32) * mm});
            skLineSegment(sketch, "E2110", {"start": v(11.52, 34.32) * mm, "end": v(11.52, 35.53) * mm});
            skLineSegment(sketch, "E2111", {"start": v(11.52, 35.53) * mm, "end": v(11.52, 36.75) * mm});
            skLineSegment(sketch, "E2112", {"start": v(11.52, 36.75) * mm, "end": v(11.1, 36.75) * mm});
            skLineSegment(sketch, "E2113", {"start": v(11.1, 36.75) * mm, "end": v(10.67, 36.75) * mm});
            skLineSegment(sketch, "E2114", {"start": v(10.67, 36.75) * mm, "end": v(10.25, 36.75) * mm});
            skLineSegment(sketch, "E2115", {"start": v(10.25, 36.75) * mm, "end": v(9.82, 36.75) * mm});
            skLineSegment(sketch, "E2116", {"start": v(9.82, 36.75) * mm, "end": v(9.4, 36.75) * mm});
            skLineSegment(sketch, "E2117", {"start": v(9.4, 36.75) * mm, "end": v(8.98, 36.75) * mm});
            skLineSegment(sketch, "E2118", {"start": v(8.98, 36.75) * mm, "end": v(8.55, 36.75) * mm});
            skLineSegment(sketch, "E2119", {"start": v(8.55, 36.75) * mm, "end": v(8.13, 36.75) * mm});
            skLineSegment(sketch, "E2120", {"start": v(8.13, 36.75) * mm, "end": v(7.7, 36.75) * mm});
            skLineSegment(sketch, "E2121", {"start": v(7.7, 36.75) * mm, "end": v(7.28, 36.75) * mm});
            skLineSegment(sketch, "E2122", {"start": v(7.28, 36.75) * mm, "end": v(6.86, 36.75) * mm});
            skLineSegment(sketch, "E2123", {"start": v(6.86, 36.75) * mm, "end": v(6.44, 36.75) * mm});
            skLineSegment(sketch, "E2124", {"start": v(6.44, 36.75) * mm, "end": v(6.01, 36.75) * mm});
            skLineSegment(sketch, "E2125", {"start": v(6.01, 36.75) * mm, "end": v(5.59, 36.75) * mm});
            skLineSegment(sketch, "E2126", {"start": v(5.59, 36.75) * mm, "end": v(5.17, 36.75) * mm});
            skLineSegment(sketch, "E2127", {"start": v(5.17, 36.75) * mm, "end": v(4.74, 36.75) * mm});
            skLineSegment(sketch, "E2128", {"start": v(14.52, 36.75) * mm, "end": v(14.52, 36.53) * mm});
            skLineSegment(sketch, "E2129", {"start": v(14.52, 36.53) * mm, "end": v(14.52, 36.3) * mm});
            skLineSegment(sketch, "E2130", {"start": v(14.52, 36.3) * mm, "end": v(14.52, 36.08) * mm});
            skLineSegment(sketch, "E2131", {"start": v(14.52, 36.08) * mm, "end": v(14.52, 35.86) * mm});
            skLineSegment(sketch, "E2132", {"start": v(14.52, 35.86) * mm, "end": v(14.52, 35.63) * mm});
            skLineSegment(sketch, "E2133", {"start": v(14.52, 35.63) * mm, "end": v(14.52, 35.41) * mm});
            skLineSegment(sketch, "E2134", {"start": v(14.52, 35.41) * mm, "end": v(14.52, 35.19) * mm});
            skLineSegment(sketch, "E2135", {"start": v(14.52, 35.19) * mm, "end": v(14.52, 34.96) * mm});
            skLineSegment(sketch, "E2136", {"start": v(14.52, 34.96) * mm, "end": v(14.52, 34.74) * mm});
            skLineSegment(sketch, "E2137", {"start": v(14.52, 34.74) * mm, "end": v(14.52, 34.52) * mm});
            skLineSegment(sketch, "E2138", {"start": v(14.52, 34.52) * mm, "end": v(14.52, 34.3) * mm});
            skLineSegment(sketch, "E2139", {"start": v(14.52, 34.3) * mm, "end": v(14.52, 34.07) * mm});
            skLineSegment(sketch, "E2140", {"start": v(14.52, 34.07) * mm, "end": v(14.52, 33.85) * mm});
            skLineSegment(sketch, "E2141", {"start": v(14.52, 33.85) * mm, "end": v(14.52, 33.63) * mm});
            skLineSegment(sketch, "E2142", {"start": v(14.52, 33.63) * mm, "end": v(14.52, 33.4) * mm});
            skLineSegment(sketch, "E2143", {"start": v(14.52, 33.4) * mm, "end": v(14.52, 33.18) * mm});
            skLineSegment(sketch, "E2144", {"start": v(14.52, 33.18) * mm, "end": v(15.1, 33.18) * mm});
            skLineSegment(sketch, "E2145", {"start": v(15.1, 33.18) * mm, "end": v(15.67, 33.18) * mm});
            skLineSegment(sketch, "E2146", {"start": v(15.67, 33.18) * mm, "end": v(16.25, 33.18) * mm});
            skLineSegment(sketch, "E2147", {"start": v(16.25, 33.18) * mm, "end": v(16.82, 33.18) * mm});
            skLineSegment(sketch, "E2148", {"start": v(16.82, 33.18) * mm, "end": v(17.4, 33.18) * mm});
            skLineSegment(sketch, "E2149", {"start": v(17.4, 33.18) * mm, "end": v(17.97, 33.18) * mm});
            skLineSegment(sketch, "E2150", {"start": v(17.97, 33.18) * mm, "end": v(18.55, 33.18) * mm});
            skLineSegment(sketch, "E2151", {"start": v(18.55, 33.18) * mm, "end": v(19.12, 33.18) * mm});
            skLineSegment(sketch, "E2152", {"start": v(19.12, 33.18) * mm, "end": v(19.7, 33.18) * mm});
            skLineSegment(sketch, "E2153", {"start": v(19.7, 33.18) * mm, "end": v(20.27, 33.18) * mm});
            skLineSegment(sketch, "E2154", {"start": v(20.27, 33.18) * mm, "end": v(20.85, 33.18) * mm});
            skLineSegment(sketch, "E2155", {"start": v(20.85, 33.18) * mm, "end": v(21.42, 33.18) * mm});
            skLineSegment(sketch, "E2156", {"start": v(21.42, 33.18) * mm, "end": v(22, 33.18) * mm});
            skLineSegment(sketch, "E2157", {"start": v(22, 33.18) * mm, "end": v(22.57, 33.18) * mm});
            skLineSegment(sketch, "E2158", {"start": v(22.57, 33.18) * mm, "end": v(23.15, 33.18) * mm});
            skLineSegment(sketch, "E2159", {"start": v(23.15, 33.18) * mm, "end": v(23.72, 33.18) * mm});
            skLineSegment(sketch, "E2160", {"start": v(23.72, 33.18) * mm, "end": v(23.26, 32.19) * mm});
            skLineSegment(sketch, "E2161", {"start": v(23.26, 32.19) * mm, "end": v(22.8, 31.2) * mm});
            skLineSegment(sketch, "E2162", {"start": v(22.8, 31.2) * mm, "end": v(22.34, 30.2) * mm});
            skLineSegment(sketch, "E2163", {"start": v(22.34, 30.2) * mm, "end": v(21.88, 29.22) * mm});
            skLineSegment(sketch, "E2164", {"start": v(21.88, 29.22) * mm, "end": v(21.42, 28.23) * mm});
            skLineSegment(sketch, "E2165", {"start": v(21.42, 28.23) * mm, "end": v(20.96, 27.24) * mm});
            skLineSegment(sketch, "E2166", {"start": v(20.96, 27.24) * mm, "end": v(20.5, 26.25) * mm});
            skLineSegment(sketch, "E2167", {"start": v(20.5, 26.25) * mm, "end": v(20.04, 25.26) * mm});
            skLineSegment(sketch, "E2168", {"start": v(20.04, 25.26) * mm, "end": v(19.58, 24.27) * mm});
            skLineSegment(sketch, "E2169", {"start": v(19.58, 24.27) * mm, "end": v(19.12, 23.28) * mm});
            skLineSegment(sketch, "E2170", {"start": v(19.12, 23.28) * mm, "end": v(18.66, 22.29) * mm});
            skLineSegment(sketch, "E2171", {"start": v(18.66, 22.29) * mm, "end": v(18.2, 21.3) * mm});
            skLineSegment(sketch, "E2172", {"start": v(18.2, 21.3) * mm, "end": v(17.73, 20.3) * mm});
            skLineSegment(sketch, "E2173", {"start": v(17.73, 20.3) * mm, "end": v(17.27, 19.32) * mm});
            skLineSegment(sketch, "E2174", {"start": v(17.27, 19.32) * mm, "end": v(16.81, 18.33) * mm});
            skLineSegment(sketch, "E2175", {"start": v(16.81, 18.33) * mm, "end": v(16.35, 17.34) * mm});
            skLineSegment(sketch, "E2176", {"start": v(16.35, 17.34) * mm, "end": v(16.33, 17.33) * mm});
            skLineSegment(sketch, "E2177", {"start": v(16.33, 17.33) * mm, "end": v(16.31, 17.33) * mm});
            skLineSegment(sketch, "E2178", {"start": v(16.31, 17.33) * mm, "end": v(16.3, 17.33) * mm});
            skLineSegment(sketch, "E2179", {"start": v(16.3, 17.33) * mm, "end": v(16.28, 17.32) * mm});
            skLineSegment(sketch, "E2180", {"start": v(16.28, 17.32) * mm, "end": v(16.26, 17.32) * mm});
            skLineSegment(sketch, "E2181", {"start": v(16.26, 17.32) * mm, "end": v(16.24, 17.32) * mm});
            skLineSegment(sketch, "E2182", {"start": v(16.24, 17.32) * mm, "end": v(16.23, 17.31) * mm});
            skLineSegment(sketch, "E2183", {"start": v(16.23, 17.31) * mm, "end": v(16.2, 17.3) * mm});
            skLineSegment(sketch, "E2184", {"start": v(16.2, 17.3) * mm, "end": v(16.19, 17.3) * mm});
            skLineSegment(sketch, "E2185", {"start": v(16.19, 17.3) * mm, "end": v(16.17, 17.3) * mm});
            skLineSegment(sketch, "E2186", {"start": v(16.17, 17.3) * mm, "end": v(16.15, 17.3) * mm});
            skLineSegment(sketch, "E2187", {"start": v(16.15, 17.3) * mm, "end": v(16.14, 17.3) * mm});
            skLineSegment(sketch, "E2188", {"start": v(16.14, 17.3) * mm, "end": v(16.12, 17.3) * mm});
            skLineSegment(sketch, "E2189", {"start": v(16.12, 17.3) * mm, "end": v(16.1, 17.29) * mm});
            skLineSegment(sketch, "E2190", {"start": v(16.1, 17.29) * mm, "end": v(16.08, 17.28) * mm});
            skLineSegment(sketch, "E2191", {"start": v(16.08, 17.28) * mm, "end": v(16.06, 17.28) * mm});
            skLineSegment(sketch, "E2192", {"start": v(16.06, 17.28) * mm, "end": v(16.35, 17.28) * mm});
            skLineSegment(sketch, "E2193", {"start": v(16.35, 17.28) * mm, "end": v(16.63, 17.28) * mm});
            skLineSegment(sketch, "E2194", {"start": v(16.63, 17.28) * mm, "end": v(16.92, 17.28) * mm});
            skLineSegment(sketch, "E2195", {"start": v(16.92, 17.28) * mm, "end": v(17.2, 17.28) * mm});
            skLineSegment(sketch, "E2196", {"start": v(17.2, 17.28) * mm, "end": v(17.48, 17.28) * mm});
            skLineSegment(sketch, "E2197", {"start": v(17.48, 17.28) * mm, "end": v(17.77, 17.28) * mm});
            skLineSegment(sketch, "E2198", {"start": v(17.77, 17.28) * mm, "end": v(18.05, 17.28) * mm});
            skLineSegment(sketch, "E2199", {"start": v(18.05, 17.28) * mm, "end": v(18.34, 17.28) * mm});
            skLineSegment(sketch, "E2200", {"start": v(18.34, 17.28) * mm, "end": v(18.62, 17.28) * mm});
            skLineSegment(sketch, "E2201", {"start": v(18.62, 17.28) * mm, "end": v(18.9, 17.28) * mm});
            skLineSegment(sketch, "E2202", {"start": v(18.9, 17.28) * mm, "end": v(19.19, 17.28) * mm});
            skLineSegment(sketch, "E2203", {"start": v(19.19, 17.28) * mm, "end": v(19.47, 17.28) * mm});
            skLineSegment(sketch, "E2204", {"start": v(19.47, 17.28) * mm, "end": v(19.76, 17.28) * mm});
            skLineSegment(sketch, "E2205", {"start": v(19.76, 17.28) * mm, "end": v(20.04, 17.28) * mm});
            skLineSegment(sketch, "E2206", {"start": v(20.04, 17.28) * mm, "end": v(20.32, 17.28) * mm});
            skLineSegment(sketch, "E2207", {"start": v(20.32, 17.28) * mm, "end": v(20.6, 17.28) * mm});
            skLineSegment(sketch, "E2208", {"start": v(20.6, 17.28) * mm, "end": v(21.08, 18.31) * mm});
            skLineSegment(sketch, "E2209", {"start": v(21.08, 18.31) * mm, "end": v(21.55, 19.34) * mm});
            skLineSegment(sketch, "E2210", {"start": v(21.55, 19.34) * mm, "end": v(22.02, 20.37) * mm});
            skLineSegment(sketch, "E2211", {"start": v(22.02, 20.37) * mm, "end": v(22.5, 21.4) * mm});
            skLineSegment(sketch, "E2212", {"start": v(22.5, 21.4) * mm, "end": v(22.97, 22.43) * mm});
            skLineSegment(sketch, "E2213", {"start": v(22.97, 22.43) * mm, "end": v(23.44, 23.46) * mm});
            skLineSegment(sketch, "E2214", {"start": v(23.44, 23.46) * mm, "end": v(23.9, 24.49) * mm});
            skLineSegment(sketch, "E2215", {"start": v(23.9, 24.49) * mm, "end": v(24.38, 25.52) * mm});
            skLineSegment(sketch, "E2216", {"start": v(24.38, 25.52) * mm, "end": v(24.85, 26.55) * mm});
            skLineSegment(sketch, "E2217", {"start": v(24.85, 26.55) * mm, "end": v(25.32, 27.58) * mm});
            skLineSegment(sketch, "E2218", {"start": v(25.32, 27.58) * mm, "end": v(25.8, 28.6) * mm});
            skLineSegment(sketch, "E2219", {"start": v(25.8, 28.6) * mm, "end": v(26.27, 29.63) * mm});
            skLineSegment(sketch, "E2220", {"start": v(26.27, 29.63) * mm, "end": v(26.74, 30.66) * mm});
            skLineSegment(sketch, "E2221", {"start": v(26.74, 30.66) * mm, "end": v(27.21, 31.7) * mm});
            skLineSegment(sketch, "E2222", {"start": v(27.21, 31.7) * mm, "end": v(27.68, 32.72) * mm});
            skLineSegment(sketch, "E2223", {"start": v(27.68, 32.72) * mm, "end": v(28.15, 33.75) * mm});
            skLineSegment(sketch, "E2224", {"start": v(28.15, 33.75) * mm, "end": v(28.15, 33.94) * mm});
            skLineSegment(sketch, "E2225", {"start": v(28.15, 33.94) * mm, "end": v(28.15, 34.13) * mm});
            skLineSegment(sketch, "E2226", {"start": v(28.15, 34.13) * mm, "end": v(28.15, 34.31) * mm});
            skLineSegment(sketch, "E2227", {"start": v(28.15, 34.31) * mm, "end": v(28.15, 34.5) * mm});
            skLineSegment(sketch, "E2228", {"start": v(28.15, 34.5) * mm, "end": v(28.15, 34.69) * mm});
            skLineSegment(sketch, "E2229", {"start": v(28.15, 34.69) * mm, "end": v(28.15, 34.88) * mm});
            skLineSegment(sketch, "E2230", {"start": v(28.15, 34.88) * mm, "end": v(28.15, 35.06) * mm});
            skLineSegment(sketch, "E2231", {"start": v(28.15, 35.06) * mm, "end": v(28.15, 35.25) * mm});
            skLineSegment(sketch, "E2232", {"start": v(28.15, 35.25) * mm, "end": v(28.15, 35.44) * mm});
            skLineSegment(sketch, "E2233", {"start": v(28.15, 35.44) * mm, "end": v(28.15, 35.62) * mm});
            skLineSegment(sketch, "E2234", {"start": v(28.15, 35.62) * mm, "end": v(28.15, 35.81) * mm});
            skLineSegment(sketch, "E2235", {"start": v(28.15, 35.81) * mm, "end": v(28.15, 36) * mm});
            skLineSegment(sketch, "E2236", {"start": v(28.15, 36) * mm, "end": v(28.15, 36.19) * mm});
            skLineSegment(sketch, "E2237", {"start": v(28.15, 36.19) * mm, "end": v(28.15, 36.37) * mm});
            skLineSegment(sketch, "E2238", {"start": v(28.15, 36.37) * mm, "end": v(28.15, 36.56) * mm});
            skLineSegment(sketch, "E2239", {"start": v(28.15, 36.56) * mm, "end": v(28.15, 36.75) * mm});
            skLineSegment(sketch, "E2240", {"start": v(28.15, 36.75) * mm, "end": v(27.3, 36.75) * mm});
            skLineSegment(sketch, "E2241", {"start": v(27.3, 36.75) * mm, "end": v(26.45, 36.75) * mm});
            skLineSegment(sketch, "E2242", {"start": v(26.45, 36.75) * mm, "end": v(25.6, 36.75) * mm});
            skLineSegment(sketch, "E2243", {"start": v(25.6, 36.75) * mm, "end": v(24.75, 36.75) * mm});
            skLineSegment(sketch, "E2244", {"start": v(24.75, 36.75) * mm, "end": v(23.9, 36.75) * mm});
            skLineSegment(sketch, "E2245", {"start": v(23.9, 36.75) * mm, "end": v(23.04, 36.75) * mm});
            skLineSegment(sketch, "E2246", {"start": v(23.04, 36.75) * mm, "end": v(22.19, 36.75) * mm});
            skLineSegment(sketch, "E2247", {"start": v(22.19, 36.75) * mm, "end": v(21.34, 36.75) * mm});
            skLineSegment(sketch, "E2248", {"start": v(21.34, 36.75) * mm, "end": v(20.49, 36.75) * mm});
            skLineSegment(sketch, "E2249", {"start": v(20.49, 36.75) * mm, "end": v(19.63, 36.75) * mm});
            skLineSegment(sketch, "E2250", {"start": v(19.63, 36.75) * mm, "end": v(18.78, 36.75) * mm});
            skLineSegment(sketch, "E2251", {"start": v(18.78, 36.75) * mm, "end": v(17.93, 36.75) * mm});
            skLineSegment(sketch, "E2252", {"start": v(17.93, 36.75) * mm, "end": v(17.08, 36.75) * mm});
            skLineSegment(sketch, "E2253", {"start": v(17.08, 36.75) * mm, "end": v(16.23, 36.75) * mm});
            skLineSegment(sketch, "E2254", {"start": v(16.23, 36.75) * mm, "end": v(15.37, 36.75) * mm});
            skLineSegment(sketch, "E2255", {"start": v(15.37, 36.75) * mm, "end": v(14.52, 36.75) * mm});
            skLineSegment(sketch, "E2256", {"start": v(-64.83, -14.05) * mm, "end": v(-56.06, -14.05) * mm});
            skLineSegment(sketch, "E2257", {"start": v(-56.06, -14.05) * mm, "end": v(-47.28, -14.04) * mm});
            skLineSegment(sketch, "E2258", {"start": v(-47.28, -14.04) * mm, "end": v(-38.5, -14.04) * mm});
            skLineSegment(sketch, "E2259", {"start": v(-38.5, -14.04) * mm, "end": v(-29.72, -14.04) * mm});
            skLineSegment(sketch, "E2260", {"start": v(-29.72, -14.04) * mm, "end": v(-20.95, -14.04) * mm});
            skLineSegment(sketch, "E2261", {"start": v(-20.95, -14.04) * mm, "end": v(-12.17, -14.03) * mm});
            skLineSegment(sketch, "E2262", {"start": v(-12.17, -14.03) * mm, "end": v(-3.4, -14.03) * mm});
            skLineSegment(sketch, "E2263", {"start": v(-3.4, -14.03) * mm, "end": v(5.38, -14.03) * mm});
            skLineSegment(sketch, "E2264", {"start": v(5.38, -14.03) * mm, "end": v(14.16, -14.03) * mm});
            skLineSegment(sketch, "E2265", {"start": v(14.16, -14.03) * mm, "end": v(22.94, -14.03) * mm});
            skLineSegment(sketch, "E2266", {"start": v(22.94, -14.03) * mm, "end": v(31.71, -14.02) * mm});
            skLineSegment(sketch, "E2267", {"start": v(31.71, -14.02) * mm, "end": v(40.5, -14.02) * mm});
            skLineSegment(sketch, "E2268", {"start": v(40.5, -14.02) * mm, "end": v(49.27, -14.02) * mm});
            skLineSegment(sketch, "E2269", {"start": v(49.27, -14.02) * mm, "end": v(58.05, -14.02) * mm});
            skLineSegment(sketch, "E2270", {"start": v(58.05, -14.02) * mm, "end": v(66.82, -14.01) * mm});
            skLineSegment(sketch, "E2271", {"start": v(66.82, -14.01) * mm, "end": v(75.6, -14.01) * mm});
            skLineSegment(sketch, "E2272", {"start": v(-64.83, -36.75) * mm, "end": v(-56.06, -36.75) * mm});
            skLineSegment(sketch, "E2273", {"start": v(-56.06, -36.75) * mm, "end": v(-47.3, -36.74) * mm});
            skLineSegment(sketch, "E2274", {"start": v(-47.3, -36.74) * mm, "end": v(-38.53, -36.74) * mm});
            skLineSegment(sketch, "E2275", {"start": v(-38.53, -36.74) * mm, "end": v(-29.76, -36.74) * mm});
            skLineSegment(sketch, "E2276", {"start": v(-29.76, -36.74) * mm, "end": v(-20.99, -36.74) * mm});
            skLineSegment(sketch, "E2277", {"start": v(-20.99, -36.74) * mm, "end": v(-12.22, -36.74) * mm});
            skLineSegment(sketch, "E2278", {"start": v(-12.22, -36.74) * mm, "end": v(-3.45, -36.73) * mm});
            skLineSegment(sketch, "E2279", {"start": v(-3.45, -36.73) * mm, "end": v(5.32, -36.73) * mm});
            skLineSegment(sketch, "E2280", {"start": v(5.32, -36.73) * mm, "end": v(14.09, -36.73) * mm});
            skLineSegment(sketch, "E2281", {"start": v(14.09, -36.73) * mm, "end": v(22.85, -36.73) * mm});
            skLineSegment(sketch, "E2282", {"start": v(22.85, -36.73) * mm, "end": v(31.62, -36.73) * mm});
            skLineSegment(sketch, "E2283", {"start": v(31.62, -36.73) * mm, "end": v(40.4, -36.72) * mm});
            skLineSegment(sketch, "E2284", {"start": v(40.4, -36.72) * mm, "end": v(49.16, -36.72) * mm});
            skLineSegment(sketch, "E2285", {"start": v(49.16, -36.72) * mm, "end": v(57.93, -36.72) * mm});
            skLineSegment(sketch, "E2286", {"start": v(57.93, -36.72) * mm, "end": v(66.7, -36.72) * mm});
            skLineSegment(sketch, "E2287", {"start": v(66.7, -36.72) * mm, "end": v(75.47, -36.72) * mm});
            skLineSegment(sketch, "E2288", {"start": v(-17.88, 36.75) * mm, "end": v(-15.86, 36.75) * mm});
            skLineSegment(sketch, "E2289", {"start": v(-15.86, 36.75) * mm, "end": v(-13.83, 36.75) * mm});
            skLineSegment(sketch, "E2290", {"start": v(-13.83, 36.75) * mm, "end": v(-11.8, 36.75) * mm});
            skLineSegment(sketch, "E2291", {"start": v(-11.8, 36.75) * mm, "end": v(-9.78, 36.75) * mm});
            skLineSegment(sketch, "E2292", {"start": v(-9.78, 36.75) * mm, "end": v(-7.76, 36.75) * mm});
            skLineSegment(sketch, "E2293", {"start": v(-7.76, 36.75) * mm, "end": v(-5.73, 36.75) * mm});
            skLineSegment(sketch, "E2294", {"start": v(-5.73, 36.75) * mm, "end": v(-3.7, 36.75) * mm});
            skLineSegment(sketch, "E2295", {"start": v(-3.7, 36.75) * mm, "end": v(-1.68, 36.75) * mm});
            skLineSegment(sketch, "E2296", {"start": v(-1.68, 36.75) * mm, "end": v(0.34, 36.75) * mm});
            skLineSegment(sketch, "E2297", {"start": v(0.34, 36.75) * mm, "end": v(2.37, 36.75) * mm});
            skLineSegment(sketch, "E2298", {"start": v(2.37, 36.75) * mm, "end": v(4.4, 36.75) * mm});
            skLineSegment(sketch, "E2299", {"start": v(4.4, 36.75) * mm, "end": v(6.42, 36.75) * mm});
            skLineSegment(sketch, "E2300", {"start": v(6.42, 36.75) * mm, "end": v(8.44, 36.75) * mm});
            skLineSegment(sketch, "E2301", {"start": v(8.44, 36.75) * mm, "end": v(10.47, 36.75) * mm});
            skLineSegment(sketch, "E2302", {"start": v(10.47, 36.75) * mm, "end": v(12.5, 36.75) * mm});
            skLineSegment(sketch, "E2303", {"start": v(12.5, 36.75) * mm, "end": v(14.52, 36.75) * mm});
            skLineSegment(sketch, "E2304", {"start": v(-14.63, 17.28) * mm, "end": v(-12.7, 17.28) * mm});
            skLineSegment(sketch, "E2305", {"start": v(-12.7, 17.28) * mm, "end": v(-10.75, 17.28) * mm});
            skLineSegment(sketch, "E2306", {"start": v(-10.75, 17.28) * mm, "end": v(-8.82, 17.28) * mm});
            skLineSegment(sketch, "E2307", {"start": v(-8.82, 17.28) * mm, "end": v(-6.88, 17.28) * mm});
            skLineSegment(sketch, "E2308", {"start": v(-6.88, 17.28) * mm, "end": v(-4.95, 17.28) * mm});
            skLineSegment(sketch, "E2309", {"start": v(-4.95, 17.28) * mm, "end": v(-3, 17.28) * mm});
            skLineSegment(sketch, "E2310", {"start": v(-3, 17.28) * mm, "end": v(-1.07, 17.28) * mm});
            skLineSegment(sketch, "E2311", {"start": v(-1.07, 17.28) * mm, "end": v(0.86, 17.28) * mm});
            skLineSegment(sketch, "E2312", {"start": v(0.86, 17.28) * mm, "end": v(2.8, 17.28) * mm});
            skLineSegment(sketch, "E2313", {"start": v(2.8, 17.28) * mm, "end": v(4.73, 17.28) * mm});
            skLineSegment(sketch, "E2314", {"start": v(4.73, 17.28) * mm, "end": v(6.67, 17.28) * mm});
            skLineSegment(sketch, "E2315", {"start": v(6.67, 17.28) * mm, "end": v(8.6, 17.28) * mm});
            skLineSegment(sketch, "E2316", {"start": v(8.6, 17.28) * mm, "end": v(10.54, 17.28) * mm});
            skLineSegment(sketch, "E2317", {"start": v(10.54, 17.28) * mm, "end": v(12.48, 17.28) * mm});
            skLineSegment(sketch, "E2318", {"start": v(12.48, 17.28) * mm, "end": v(14.41, 17.28) * mm});
            skLineSegment(sketch, "E2319", {"start": v(14.41, 17.28) * mm, "end": v(16.35, 17.28) * mm});
            skSolve(sketch);
        }
        {
            var Q0;
            Q0=makeQuery(id+"F0.imprint","IMPRINT",FACE,{"disambiguationData":[TD([[makeQuery(id+"F0.imprint","IMPRINT",EDGE,{"derivedFrom":sQuery(id+"F0.wireOp",EDGE,"E0")}),1.0]])]});
            var Q1;
            Q1=makeQuery(id+"F0.imprint","IMPRINT",FACE,{"disambiguationData":[TD([[makeQuery(id+"F0.imprint","IMPRINT",EDGE,{"derivedFrom":sQuery(id+"F0.wireOp",EDGE,"E192")}),1.0]])]});
            var Q2;
            Q2=makeQuery(id+"F0.imprint","IMPRINT",FACE,{"disambiguationData":[TD([[makeQuery(id+"F0.imprint","IMPRINT",EDGE,{"derivedFrom":sQuery(id+"F0.wireOp",EDGE,"E1136")}),1.0]])]});
            var Q3;
            Q3=makeQuery(id+"F0.imprint","IMPRINT",FACE,{"disambiguationData":[TD([[makeQuery(id+"F0.imprint","IMPRINT",EDGE,{"derivedFrom":sQuery(id+"F0.wireOp",EDGE,"E384")}),1.0]])]});
            var Q4;
            Q4=makeQuery(id+"F0.imprint","IMPRINT",FACE,{"disambiguationData":[TD([[makeQuery(id+"F0.imprint","IMPRINT",EDGE,{"derivedFrom":sQuery(id+"F0.wireOp",EDGE,"E592")}),1.0]])]});
            var Q5;
            {var subQ0=sQuery(id+"F0.wireOp",EDGE,"E833");Q5=makeQuery(id+"F0.imprint","IMPRINT",FACE,{"disambiguationData":[TD([[makeQuery(id+"F0.imprint","IMPRINT",EDGE,{"derivedFrom":subQ0}),1.0]])]});}
            var Q6;
            Q6=makeQuery(id+"F0.imprint","IMPRINT",FACE,{"disambiguationData":[TD([[makeQuery(id+"F0.imprint","IMPRINT",EDGE,{"derivedFrom":sQuery(id+"F0.wireOp",EDGE,"E880")}),1.0]])]});
            var Q7;
            Q7=makeQuery(id+"F0.imprint","IMPRINT",FACE,{"disambiguationData":[TD([[makeQuery(id+"F0.imprint","IMPRINT",EDGE,{"derivedFrom":sQuery(id+"F0.wireOp",EDGE,"E1312")}),1.0]])]});
            var Q8;
            Q8=makeQuery(id+"F0.imprint","IMPRINT",FACE,{"disambiguationData":[TD([[makeQuery(id+"F0.imprint","IMPRINT",EDGE,{"derivedFrom":sQuery(id+"F0.wireOp",EDGE,"E2128")}),1.0]])]});
            var Q9;
            {var subQ0=sQuery(id+"F0.wireOp",EDGE,"E2032");Q9=makeQuery(id+"F0.imprint","IMPRINT",FACE,{"disambiguationData":[TD([[makeQuery(id+"F0.imprint","IMPRINT",EDGE,{"derivedFrom":subQ0}),1.0]])]});}
            var Q10;
            Q10=makeQuery(id+"F0.imprint","IMPRINT",FACE,{"disambiguationData":[TD([[makeQuery(id+"F0.imprint","IMPRINT",EDGE,{"derivedFrom":sQuery(id+"F0.wireOp",EDGE,"E1776")}),1.0]])]});
            var Q11;
            Q11=makeQuery(id+"F0.imprint","IMPRINT",FACE,{"disambiguationData":[TD([[makeQuery(id+"F0.imprint","IMPRINT",EDGE,{"derivedFrom":sQuery(id+"F0.wireOp",EDGE,"E1472")}),1.0]])]});
            extrude(context, id + "F1", {"entities" : qUnion([Q0, Q1, Q2, Q3, Q4, Q5, Q6, Q7, Q8, Q9, Q10, Q11]), "depth" : 3 * mm, "offsetDistance" : 25 * mm});
        }
        {
            var Q0;
            Q0=makeQuery(id+"F0.imprint","IMPRINT",FACE,{"disambiguationData":[TD([[makeQuery(id+"F0.imprint","IMPRINT",EDGE,{"derivedFrom":sQuery(id+"F0.wireOp",EDGE,"E0")}),1.0]])]});
            var Q1;
            {var subQ13=sQuery(id+"F0.wireOp",EDGE,"E64");Q1=makeQuery(id+"F0.imprint","IMPRINT",FACE,{"disambiguationData":[TD([[makeQuery(id+"F0.imprint","IMPRINT",EDGE,{"derivedFrom":subQ13}),-1.0]])]});}
            var Q2;
            Q2=makeQuery(id+"F0.imprint","IMPRINT",FACE,{"disambiguationData":[TD([[makeQuery(id+"F0.imprint","IMPRINT",EDGE,{"derivedFrom":sQuery(id+"F0.wireOp",EDGE,"E192")}),1.0]])]});
            var Q3;
            Q3=makeQuery(id+"F0.imprint","IMPRINT",FACE,{"disambiguationData":[TD([[makeQuery(id+"F0.imprint","IMPRINT",EDGE,{"derivedFrom":sQuery(id+"F0.wireOp",EDGE,"E1136")}),1.0]])]});
            var Q4;
            Q4=makeQuery(id+"F0.imprint","IMPRINT",FACE,{"disambiguationData":[TD([[makeQuery(id+"F0.imprint","IMPRINT",EDGE,{"derivedFrom":sQuery(id+"F0.wireOp",EDGE,"E1136")}),-1.0]])]});
            var Q5;
            {var subQ7=sQuery(id+"F0.wireOp",EDGE,"E1217");Q5=makeQuery(id+"F0.imprint","IMPRINT",FACE,{"disambiguationData":[TD([[makeQuery(id+"F0.imprint","IMPRINT",EDGE,{"derivedFrom":subQ7}),-1.0]])]});}
            var Q6;
            {var subQ7=sQuery(id+"F0.wireOp",EDGE,"E289");Q6=makeQuery(id+"F0.imprint","IMPRINT",FACE,{"disambiguationData":[TD([[makeQuery(id+"F0.imprint","IMPRINT",EDGE,{"derivedFrom":subQ7}),-1.0]])]});}
            var Q7;
            Q7=makeQuery(id+"F0.imprint","IMPRINT",FACE,{"disambiguationData":[TD([[makeQuery(id+"F0.imprint","IMPRINT",EDGE,{"derivedFrom":sQuery(id+"F0.wireOp",EDGE,"E384")}),-1.0]])]});
            var Q8;
            Q8=makeQuery(id+"F0.imprint","IMPRINT",FACE,{"disambiguationData":[TD([[makeQuery(id+"F0.imprint","IMPRINT",EDGE,{"derivedFrom":sQuery(id+"F0.wireOp",EDGE,"E384")}),1.0]])]});
            var Q9;
            {var subQ7=sQuery(id+"F0.wireOp",EDGE,"E465");Q9=makeQuery(id+"F0.imprint","IMPRINT",FACE,{"disambiguationData":[TD([[makeQuery(id+"F0.imprint","IMPRINT",EDGE,{"derivedFrom":subQ7}),-1.0]])]});}
            var Q10;
            Q10=makeQuery(id+"F0.imprint","IMPRINT",FACE,{"disambiguationData":[TD([[makeQuery(id+"F0.imprint","IMPRINT",EDGE,{"derivedFrom":sQuery(id+"F0.wireOp",EDGE,"E592")}),-1.0]])]});
            var Q11;
            Q11=makeQuery(id+"F0.imprint","IMPRINT",FACE,{"disambiguationData":[TD([[makeQuery(id+"F0.imprint","IMPRINT",EDGE,{"derivedFrom":sQuery(id+"F0.wireOp",EDGE,"E592")}),1.0]])]});
            var Q12;
            {var subQ0=sQuery(id+"F0.wireOp",EDGE,"E833");Q12=makeQuery(id+"F0.imprint","IMPRINT",FACE,{"disambiguationData":[TD([[makeQuery(id+"F0.imprint","IMPRINT",EDGE,{"derivedFrom":subQ0}),1.0]])]});}
            var Q13;
            Q13=makeQuery(id+"F0.imprint","IMPRINT",FACE,{"disambiguationData":[TD([[makeQuery(id+"F0.imprint","IMPRINT",EDGE,{"derivedFrom":sQuery(id+"F0.wireOp",EDGE,"E880")}),1.0]])]});
            var Q14;
            Q14=makeQuery(id+"F0.imprint","IMPRINT",FACE,{"disambiguationData":[TD([[makeQuery(id+"F0.imprint","IMPRINT",EDGE,{"derivedFrom":sQuery(id+"F0.wireOp",EDGE,"E880")}),-1.0]])]});
            var Q15;
            Q15=makeQuery(id+"F0.imprint","IMPRINT",FACE,{"disambiguationData":[TD([[makeQuery(id+"F0.imprint","IMPRINT",EDGE,{"derivedFrom":sQuery(id+"F0.wireOp",EDGE,"E1312")}),1.0]])]});
            var Q16;
            Q16=makeQuery(id+"F0.imprint","IMPRINT",FACE,{"disambiguationData":[TD([[makeQuery(id+"F0.imprint","IMPRINT",EDGE,{"derivedFrom":sQuery(id+"F0.wireOp",EDGE,"E1312")}),-1.0]])]});
            var Q17;
            Q17=makeQuery(id+"F0.imprint","IMPRINT",FACE,{"disambiguationData":[TD([[makeQuery(id+"F0.imprint","IMPRINT",EDGE,{"derivedFrom":sQuery(id+"F0.wireOp",EDGE,"E2128")}),1.0]])]});
            var Q18;
            {var subQ4=sQuery(id+"F0.wireOp",EDGE,"E2096");Q18=makeQuery(id+"F0.imprint","IMPRINT",FACE,{"disambiguationData":[TD([[makeQuery(id+"F0.imprint","IMPRINT",EDGE,{"derivedFrom":subQ4}),-1.0]])]});}
            var Q19;
            {var subQ0=sQuery(id+"F0.wireOp",EDGE,"E2032");Q19=makeQuery(id+"F0.imprint","IMPRINT",FACE,{"disambiguationData":[TD([[makeQuery(id+"F0.imprint","IMPRINT",EDGE,{"derivedFrom":subQ0}),1.0]])]});}
            var Q20;
            {var subQ3=sQuery(id+"F0.wireOp",EDGE,"E1968");Q20=makeQuery(id+"F0.imprint","IMPRINT",FACE,{"disambiguationData":[TD([[makeQuery(id+"F0.imprint","IMPRINT",EDGE,{"derivedFrom":subQ3}),-1.0]])]});}
            var Q21;
            Q21=makeQuery(id+"F0.imprint","IMPRINT",FACE,{"disambiguationData":[TD([[makeQuery(id+"F0.imprint","IMPRINT",EDGE,{"derivedFrom":sQuery(id+"F0.wireOp",EDGE,"E1776")}),1.0]])]});
            var Q22;
            Q22=makeQuery(id+"F0.imprint","IMPRINT",FACE,{"disambiguationData":[TD([[makeQuery(id+"F0.imprint","IMPRINT",EDGE,{"derivedFrom":sQuery(id+"F0.wireOp",EDGE,"E1776")}),-1.0]])]});
            var Q23;
            Q23=makeQuery(id+"F0.imprint","IMPRINT",FACE,{"disambiguationData":[TD([[makeQuery(id+"F0.imprint","IMPRINT",EDGE,{"derivedFrom":sQuery(id+"F0.wireOp",EDGE,"E1664")}),-1.0]])]});
            var Q24;
            Q24=makeQuery(id+"F0.imprint","IMPRINT",FACE,{"disambiguationData":[TD([[makeQuery(id+"F0.imprint","IMPRINT",EDGE,{"derivedFrom":sQuery(id+"F0.wireOp",EDGE,"E1472")}),1.0]])]});
            extrude(context, id + "F2", {"entities" : qUnion([Q0, Q1, Q2, Q3, Q4, Q5, Q6, Q7, Q8, Q9, Q10, Q11, Q12, Q13, Q14, Q15, Q16, Q17, Q18, Q19, Q20, Q21, Q22, Q23, Q24]), "oppositeDirection" : true, "depth" : 0.5 * mm, "offsetDistance" : 25 * mm});
        }
    });
